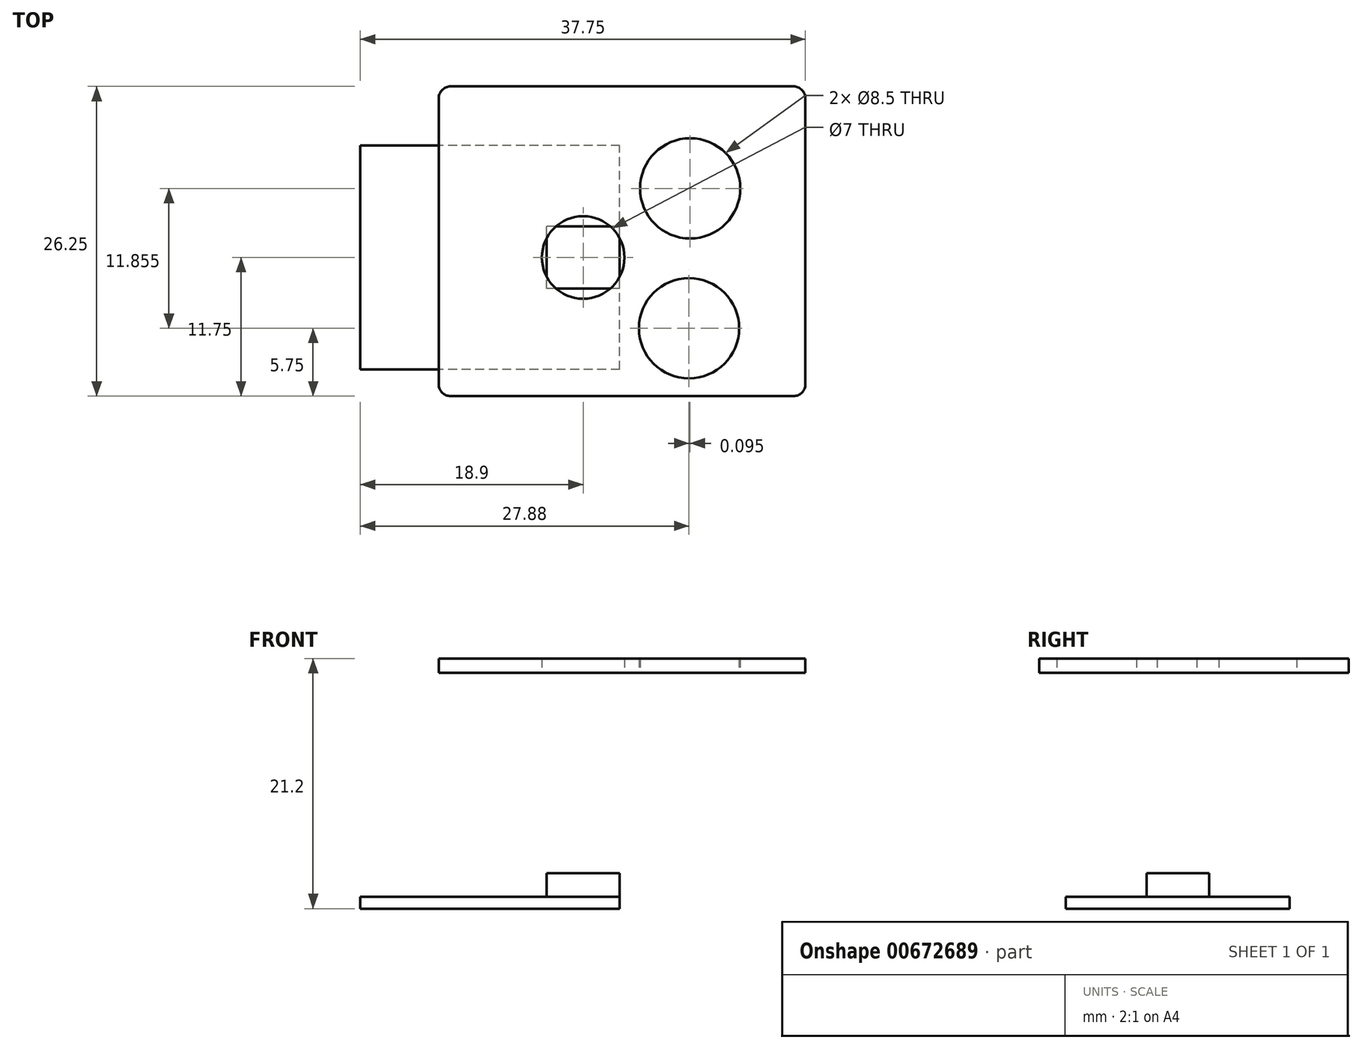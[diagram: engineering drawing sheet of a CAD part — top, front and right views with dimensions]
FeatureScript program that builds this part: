
annotation { "Feature Type Name" : "Feature", "Feature Type Description" : "" }
export const myFeature = defineFeature(function(context is Context, id is Id, definition is map)
    precondition{}
    {
        {
            var Q0;
            Q0=qCreatedBy(makeId("Top.planeOp"),FACE);
            var sketch = newSketch(context, id + "F0", { "sketchPlane" : qUnion([Q0])});
            skCircle(sketch, "E0", {"center": v(0, 0) * mm, "radius": 12.25 * mm});
            skCircle(sketch, "E1", {"center": v(0, 0) * mm, "radius": 10 * mm});
            skCircle(sketch, "E2", {"center": v(0, 0) * mm, "radius": 9 * mm});
            skCircle(sketch, "E3", {"center": v(0, 0) * mm, "radius": 3.5 * mm});
            skSolve(sketch);
        }
        {
            var Q0;
            Q0=qCreatedBy(makeId("Top.planeOp"),FACE);
            var sketch = newSketch(context, id + "F1", { "sketchPlane" : qUnion([Q0])});
            skLineSegment(sketch, "E4.bottom", {"start": v(3.1, -2.65) * mm, "end": v(-3.1, -2.65) * mm});
            skLineSegment(sketch, "E4.top", {"start": v(3.1, 2.65) * mm, "end": v(-3.1, 2.65) * mm});
            skLineSegment(sketch, "E4.right", {"start": v(-3.1, -2.65) * mm, "end": v(-3.1, 2.65) * mm});
            skPoint(sketch, "E4.middle", {"position": v(0, 0) * mm});
            skLineSegment(sketch, "E5.bottom", {"start": v(3.1, -9.5) * mm, "end": v(-18.9, -9.5) * mm});
            skLineSegment(sketch, "E5.top", {"start": v(3.1, 9.5) * mm, "end": v(-18.9, 9.5) * mm});
            skLineSegment(sketch, "E5.left", {"start": v(3.1, -9.5) * mm, "end": v(3.1, 9.5) * mm});
            skLineSegment(sketch, "E5.right", {"start": v(-18.9, -9.5) * mm, "end": v(-18.9, 9.5) * mm});
            skLineSegment(sketch, "E6.bottom", {"start": v(18.78, 13) * mm, "end": v(-13.22, 13) * mm});
            skLineSegment(sketch, "E6.top", {"start": v(18.78, 14.1) * mm, "end": v(-13.22, 14.1) * mm});
            skLineSegment(sketch, "E6.left", {"start": v(18.78, 13) * mm, "end": v(18.78, 14.1) * mm});
            skLineSegment(sketch, "E6.right", {"start": v(-13.22, 13) * mm, "end": v(-13.22, 14.1) * mm});
            skPoint(sketch, "E6.middle", {"position": v(2.78, 13.54) * mm});
            skLineSegment(sketch, "E7.bottom", {"start": v(12.25, -12.25) * mm, "end": v(-12.25, -12.25) * mm});
            skLineSegment(sketch, "E7.top", {"start": v(12.25, 12.25) * mm, "end": v(-12.25, 12.25) * mm});
            skLineSegment(sketch, "E7.left", {"start": v(12.25, -12.25) * mm, "end": v(12.25, 12.25) * mm});
            skLineSegment(sketch, "E7.right", {"start": v(-12.25, -12.25) * mm, "end": v(-12.25, 12.25) * mm});
            skSolve(sketch);
        }
        {
            var Q0;
            Q0=qCreatedBy(makeId("Top.planeOp"),FACE);
            var sketch = newSketch(context, id + "F2", { "sketchPlane" : qUnion([Q0])});
            skCircle(sketch, "E8", {"center": v(8.98, -6) * mm, "radius": 4.25 * mm});
            skCircle(sketch, "E9", {"center": v(8.98, -6) * mm, "radius": 1.8 * mm});
            skLineSegment(sketch, "E10", {"start": v(-13.47, -10.25) * mm, "end": v(15.3, -10.25) * mm});
            skLineSegment(sketch, "E11", {"start": v(-13.52, -6) * mm, "end": v(15.26, -6) * mm});
            skCircle(sketch, "E12", {"center": v(9.07, 5.86) * mm, "radius": 1.8 * mm});
            skCircle(sketch, "E13", {"center": v(9.07, 5.86) * mm, "radius": 4.25 * mm});
            skLineSegment(sketch, "E14", {"start": v(-12.37, 10.1) * mm, "end": v(16.41, 10.1) * mm});
            skLineSegment(sketch, "E15", {"start": v(-12.37, 5.86) * mm, "end": v(16.4, 5.86) * mm});
            skLineSegment(sketch, "E16", {"start": v(8.98, -6) * mm, "end": v(3.1, 0) * mm});
            skPoint(sketch, "E17", {"position": v(3.1, 0) * mm});
            skLineSegment(sketch, "E18", {"start": v(3.1, 0) * mm, "end": v(9.07, 5.86) * mm});
            skLineSegment(sketch, "E19.bottom", {"start": v(22.5, -11.75) * mm, "end": v(-22.5, -11.75) * mm});
            skPoint(sketch, "E19.middle", {"position": v(0, 0) * mm});
            skLineSegment(sketch, "E20.0", {"start": v(22.5, -12.25) * mm, "end": v(-22.5, -12.25) * mm});
            skLineSegment(sketch, "E21", {"start": v(0, -12.25) * mm, "end": v(-22.5, -11.75) * mm});
            skLineSegment(sketch, "E22", {"start": v(22.5, -11.75) * mm, "end": v(0, -12.25) * mm});
            skSolve(sketch);
        }
        {
            var Q0;
            Q0=qCreatedBy(makeId("Top.planeOp"),FACE);
            var sketch = newSketch(context, id + "F3", { "sketchPlane" : qUnion([Q0])});
            skPoint(sketch, "E23.middle", {"position": v(0, 0.27) * mm});
            skPoint(sketch, "E24.7.0.0", {"position": v(-11.9, 11.25) * mm});
            skLineSegment(sketch, "E24.7.0.1", {"start": v(-11.55, 10.25) * mm, "end": v(-12.25, 10.25) * mm});
            skLineSegment(sketch, "E24.7.0.2", {"start": v(-11.55, 10.25) * mm, "end": v(-11.55, 12.25) * mm});
            skLineSegment(sketch, "E24.7.0.3", {"start": v(-12.25, 10.25) * mm, "end": v(-12.25, 12.25) * mm});
            skLineSegment(sketch, "E24.7.0.4", {"start": v(-11.55, 12.25) * mm, "end": v(-12.25, 12.25) * mm});
            skPoint(sketch, "E24.8.0.0", {"position": v(-10.95, 11.25) * mm});
            skLineSegment(sketch, "E24.8.0.1", {"start": v(-10.6, 10.25) * mm, "end": v(-11.3, 10.25) * mm});
            skLineSegment(sketch, "E24.8.0.2", {"start": v(-10.6, 10.25) * mm, "end": v(-10.6, 12.25) * mm});
            skLineSegment(sketch, "E24.8.0.3", {"start": v(-11.3, 10.25) * mm, "end": v(-11.3, 12.25) * mm});
            skLineSegment(sketch, "E24.8.0.4", {"start": v(-10.6, 12.25) * mm, "end": v(-11.3, 12.25) * mm});
            skPoint(sketch, "E24.9.0.0", {"position": v(-10, 11.25) * mm});
            skLineSegment(sketch, "E24.9.0.1", {"start": v(-9.65, 10.25) * mm, "end": v(-10.35, 10.25) * mm});
            skLineSegment(sketch, "E24.9.0.2", {"start": v(-9.65, 10.25) * mm, "end": v(-9.65, 12.25) * mm});
            skLineSegment(sketch, "E24.9.0.3", {"start": v(-10.35, 10.25) * mm, "end": v(-10.35, 12.25) * mm});
            skLineSegment(sketch, "E24.9.0.4", {"start": v(-9.65, 12.25) * mm, "end": v(-10.35, 12.25) * mm});
            skPoint(sketch, "E24.10.0.0", {"position": v(-9.05, 11.25) * mm});
            skLineSegment(sketch, "E24.10.0.1", {"start": v(-8.7, 10.25) * mm, "end": v(-9.4, 10.25) * mm});
            skLineSegment(sketch, "E24.10.0.2", {"start": v(-8.7, 10.25) * mm, "end": v(-8.7, 12.25) * mm});
            skLineSegment(sketch, "E24.10.0.3", {"start": v(-9.4, 10.25) * mm, "end": v(-9.4, 12.25) * mm});
            skLineSegment(sketch, "E24.10.0.4", {"start": v(-8.7, 12.25) * mm, "end": v(-9.4, 12.25) * mm});
            skPoint(sketch, "E24.11.0.0", {"position": v(-8.1, 11.25) * mm});
            skLineSegment(sketch, "E24.11.0.1", {"start": v(-7.75, 10.25) * mm, "end": v(-8.45, 10.25) * mm});
            skLineSegment(sketch, "E24.11.0.2", {"start": v(-7.75, 10.25) * mm, "end": v(-7.75, 12.25) * mm});
            skLineSegment(sketch, "E24.11.0.3", {"start": v(-8.45, 10.25) * mm, "end": v(-8.45, 12.25) * mm});
            skLineSegment(sketch, "E24.11.0.4", {"start": v(-7.75, 12.25) * mm, "end": v(-8.45, 12.25) * mm});
            skPoint(sketch, "E24.12.0.0", {"position": v(-7.15, 11.25) * mm});
            skLineSegment(sketch, "E24.12.0.1", {"start": v(-6.8, 10.25) * mm, "end": v(-7.5, 10.25) * mm});
            skLineSegment(sketch, "E24.12.0.2", {"start": v(-6.8, 10.25) * mm, "end": v(-6.8, 12.25) * mm});
            skLineSegment(sketch, "E24.12.0.3", {"start": v(-7.5, 10.25) * mm, "end": v(-7.5, 12.25) * mm});
            skLineSegment(sketch, "E24.12.0.4", {"start": v(-6.8, 12.25) * mm, "end": v(-7.5, 12.25) * mm});
            skPoint(sketch, "E24.13.0.0", {"position": v(-6.2, 11.25) * mm});
            skLineSegment(sketch, "E24.13.0.1", {"start": v(-5.85, 10.25) * mm, "end": v(-6.55, 10.25) * mm});
            skLineSegment(sketch, "E24.13.0.2", {"start": v(-5.85, 10.25) * mm, "end": v(-5.85, 12.25) * mm});
            skLineSegment(sketch, "E24.13.0.3", {"start": v(-6.55, 10.25) * mm, "end": v(-6.55, 12.25) * mm});
            skLineSegment(sketch, "E24.13.0.4", {"start": v(-5.85, 12.25) * mm, "end": v(-6.55, 12.25) * mm});
            skPoint(sketch, "E24.14.0.0", {"position": v(-5.25, 11.25) * mm});
            skLineSegment(sketch, "E24.14.0.1", {"start": v(-4.9, 10.25) * mm, "end": v(-5.6, 10.25) * mm});
            skLineSegment(sketch, "E24.14.0.2", {"start": v(-4.9, 10.25) * mm, "end": v(-4.9, 12.25) * mm});
            skLineSegment(sketch, "E24.14.0.3", {"start": v(-5.6, 10.25) * mm, "end": v(-5.6, 12.25) * mm});
            skLineSegment(sketch, "E24.14.0.4", {"start": v(-4.9, 12.25) * mm, "end": v(-5.6, 12.25) * mm});
            skPoint(sketch, "E24.15.0.0", {"position": v(-4.3, 11.25) * mm});
            skLineSegment(sketch, "E24.15.0.1", {"start": v(-3.95, 10.25) * mm, "end": v(-4.65, 10.25) * mm});
            skLineSegment(sketch, "E24.15.0.2", {"start": v(-3.95, 10.25) * mm, "end": v(-3.95, 12.25) * mm});
            skLineSegment(sketch, "E24.15.0.3", {"start": v(-4.65, 10.25) * mm, "end": v(-4.65, 12.25) * mm});
            skLineSegment(sketch, "E24.15.0.4", {"start": v(-3.95, 12.25) * mm, "end": v(-4.65, 12.25) * mm});
            skPoint(sketch, "E24.16.0.0", {"position": v(-3.35, 11.25) * mm});
            skLineSegment(sketch, "E24.16.0.1", {"start": v(-3, 10.25) * mm, "end": v(-3.7, 10.25) * mm});
            skLineSegment(sketch, "E24.16.0.2", {"start": v(-3, 10.25) * mm, "end": v(-3, 12.25) * mm});
            skLineSegment(sketch, "E24.16.0.3", {"start": v(-3.7, 10.25) * mm, "end": v(-3.7, 12.25) * mm});
            skLineSegment(sketch, "E24.16.0.4", {"start": v(-3, 12.25) * mm, "end": v(-3.7, 12.25) * mm});
            skPoint(sketch, "E24.17.0.0", {"position": v(-2.4, 11.25) * mm});
            skLineSegment(sketch, "E24.17.0.1", {"start": v(-2.05, 10.25) * mm, "end": v(-2.75, 10.25) * mm});
            skLineSegment(sketch, "E24.17.0.2", {"start": v(-2.05, 10.25) * mm, "end": v(-2.05, 12.25) * mm});
            skLineSegment(sketch, "E24.17.0.3", {"start": v(-2.75, 10.25) * mm, "end": v(-2.75, 12.25) * mm});
            skLineSegment(sketch, "E24.17.0.4", {"start": v(-2.05, 12.25) * mm, "end": v(-2.75, 12.25) * mm});
            skPoint(sketch, "E24.18.0.0", {"position": v(-1.45, 11.25) * mm});
            skLineSegment(sketch, "E24.18.0.1", {"start": v(-1.1, 10.25) * mm, "end": v(-1.8, 10.25) * mm});
            skLineSegment(sketch, "E24.18.0.2", {"start": v(-1.1, 10.25) * mm, "end": v(-1.1, 12.25) * mm});
            skLineSegment(sketch, "E24.18.0.3", {"start": v(-1.8, 10.25) * mm, "end": v(-1.8, 12.25) * mm});
            skLineSegment(sketch, "E24.18.0.4", {"start": v(-1.1, 12.25) * mm, "end": v(-1.8, 12.25) * mm});
            skPoint(sketch, "E24.19.0.0", {"position": v(-0.5, 11.25) * mm});
            skLineSegment(sketch, "E24.19.0.1", {"start": v(-0.15, 10.25) * mm, "end": v(-0.85, 10.25) * mm});
            skLineSegment(sketch, "E24.19.0.2", {"start": v(-0.15, 10.25) * mm, "end": v(-0.15, 12.25) * mm});
            skLineSegment(sketch, "E24.19.0.3", {"start": v(-0.85, 10.25) * mm, "end": v(-0.85, 12.25) * mm});
            skLineSegment(sketch, "E24.19.0.4", {"start": v(-0.15, 12.25) * mm, "end": v(-0.85, 12.25) * mm});
            skPoint(sketch, "E24.20.0.0", {"position": v(0.45, 11.25) * mm});
            skLineSegment(sketch, "E24.20.0.1", {"start": v(0.8, 10.25) * mm, "end": v(0.1, 10.25) * mm});
            skLineSegment(sketch, "E24.20.0.2", {"start": v(0.8, 10.25) * mm, "end": v(0.8, 12.25) * mm});
            skLineSegment(sketch, "E24.20.0.3", {"start": v(0.1, 10.25) * mm, "end": v(0.1, 12.25) * mm});
            skLineSegment(sketch, "E24.20.0.4", {"start": v(0.8, 12.25) * mm, "end": v(0.1, 12.25) * mm});
            skPoint(sketch, "E24.21.0.0", {"position": v(1.4, 11.25) * mm});
            skLineSegment(sketch, "E24.21.0.1", {"start": v(1.75, 10.25) * mm, "end": v(1.05, 10.25) * mm});
            skLineSegment(sketch, "E24.21.0.2", {"start": v(1.75, 10.25) * mm, "end": v(1.75, 12.25) * mm});
            skLineSegment(sketch, "E24.21.0.3", {"start": v(1.05, 10.25) * mm, "end": v(1.05, 12.25) * mm});
            skLineSegment(sketch, "E24.21.0.4", {"start": v(1.75, 12.25) * mm, "end": v(1.05, 12.25) * mm});
            skPoint(sketch, "E24.22.0.0", {"position": v(2.35, 11.25) * mm});
            skLineSegment(sketch, "E24.22.0.1", {"start": v(2.7, 10.25) * mm, "end": v(2, 10.25) * mm});
            skLineSegment(sketch, "E24.22.0.2", {"start": v(2.7, 10.25) * mm, "end": v(2.7, 12.25) * mm});
            skLineSegment(sketch, "E24.22.0.3", {"start": v(2, 10.25) * mm, "end": v(2, 12.25) * mm});
            skLineSegment(sketch, "E24.22.0.4", {"start": v(2.7, 12.25) * mm, "end": v(2, 12.25) * mm});
            skPoint(sketch, "E24.23.0.0", {"position": v(3.3, 11.25) * mm});
            skLineSegment(sketch, "E24.23.0.1", {"start": v(3.65, 10.25) * mm, "end": v(2.95, 10.25) * mm});
            skLineSegment(sketch, "E24.23.0.2", {"start": v(3.65, 10.25) * mm, "end": v(3.65, 12.25) * mm});
            skLineSegment(sketch, "E24.23.0.3", {"start": v(2.95, 10.25) * mm, "end": v(2.95, 12.25) * mm});
            skLineSegment(sketch, "E24.23.0.4", {"start": v(3.65, 12.25) * mm, "end": v(2.95, 12.25) * mm});
            skPoint(sketch, "E24.24.0.0", {"position": v(4.25, 11.25) * mm});
            skLineSegment(sketch, "E24.24.0.1", {"start": v(4.6, 10.25) * mm, "end": v(3.9, 10.25) * mm});
            skLineSegment(sketch, "E24.24.0.2", {"start": v(4.6, 10.25) * mm, "end": v(4.6, 12.25) * mm});
            skLineSegment(sketch, "E24.24.0.3", {"start": v(3.9, 10.25) * mm, "end": v(3.9, 12.25) * mm});
            skLineSegment(sketch, "E24.24.0.4", {"start": v(4.6, 12.25) * mm, "end": v(3.9, 12.25) * mm});
            skPoint(sketch, "E24.25.0.0", {"position": v(5.2, 11.25) * mm});
            skLineSegment(sketch, "E24.25.0.1", {"start": v(5.55, 10.25) * mm, "end": v(4.85, 10.25) * mm});
            skLineSegment(sketch, "E24.25.0.2", {"start": v(5.55, 10.25) * mm, "end": v(5.55, 12.25) * mm});
            skLineSegment(sketch, "E24.25.0.3", {"start": v(4.85, 10.25) * mm, "end": v(4.85, 12.25) * mm});
            skLineSegment(sketch, "E24.25.0.4", {"start": v(5.55, 12.25) * mm, "end": v(4.85, 12.25) * mm});
            skPoint(sketch, "E24.26.0.0", {"position": v(6.15, 11.25) * mm});
            skLineSegment(sketch, "E24.26.0.1", {"start": v(6.5, 10.25) * mm, "end": v(5.8, 10.25) * mm});
            skLineSegment(sketch, "E24.26.0.2", {"start": v(6.5, 10.25) * mm, "end": v(6.5, 12.25) * mm});
            skLineSegment(sketch, "E24.26.0.3", {"start": v(5.8, 10.25) * mm, "end": v(5.8, 12.25) * mm});
            skLineSegment(sketch, "E24.26.0.4", {"start": v(6.5, 12.25) * mm, "end": v(5.8, 12.25) * mm});
            skPoint(sketch, "E24.27.0.0", {"position": v(7.1, 11.25) * mm});
            skLineSegment(sketch, "E24.27.0.1", {"start": v(7.45, 10.25) * mm, "end": v(6.75, 10.25) * mm});
            skLineSegment(sketch, "E24.27.0.2", {"start": v(7.45, 10.25) * mm, "end": v(7.45, 12.25) * mm});
            skLineSegment(sketch, "E24.27.0.3", {"start": v(6.75, 10.25) * mm, "end": v(6.75, 12.25) * mm});
            skLineSegment(sketch, "E24.27.0.4", {"start": v(7.45, 12.25) * mm, "end": v(6.75, 12.25) * mm});
            skPoint(sketch, "E24.28.0.0", {"position": v(8.05, 11.25) * mm});
            skLineSegment(sketch, "E24.28.0.1", {"start": v(8.4, 10.25) * mm, "end": v(7.7, 10.25) * mm});
            skLineSegment(sketch, "E24.28.0.2", {"start": v(8.4, 10.25) * mm, "end": v(8.4, 12.25) * mm});
            skLineSegment(sketch, "E24.28.0.3", {"start": v(7.7, 10.25) * mm, "end": v(7.7, 12.25) * mm});
            skLineSegment(sketch, "E24.28.0.4", {"start": v(8.4, 12.25) * mm, "end": v(7.7, 12.25) * mm});
            skPoint(sketch, "E24.29.0.0", {"position": v(9, 11.25) * mm});
            skLineSegment(sketch, "E24.29.0.1", {"start": v(9.35, 10.25) * mm, "end": v(8.65, 10.25) * mm});
            skLineSegment(sketch, "E24.29.0.2", {"start": v(9.35, 10.25) * mm, "end": v(9.35, 12.25) * mm});
            skLineSegment(sketch, "E24.29.0.3", {"start": v(8.65, 10.25) * mm, "end": v(8.65, 12.25) * mm});
            skLineSegment(sketch, "E24.29.0.4", {"start": v(9.35, 12.25) * mm, "end": v(8.65, 12.25) * mm});
            skPoint(sketch, "E24.30.0.0", {"position": v(9.95, 11.25) * mm});
            skLineSegment(sketch, "E24.30.0.1", {"start": v(10.3, 10.25) * mm, "end": v(9.6, 10.25) * mm});
            skLineSegment(sketch, "E24.30.0.2", {"start": v(10.3, 10.25) * mm, "end": v(10.3, 12.25) * mm});
            skLineSegment(sketch, "E24.30.0.3", {"start": v(9.6, 10.25) * mm, "end": v(9.6, 12.25) * mm});
            skLineSegment(sketch, "E24.30.0.4", {"start": v(10.3, 12.25) * mm, "end": v(9.6, 12.25) * mm});
            skPoint(sketch, "E24.31.0.0", {"position": v(10.9, 11.25) * mm});
            skLineSegment(sketch, "E24.31.0.1", {"start": v(11.25, 10.25) * mm, "end": v(10.55, 10.25) * mm});
            skLineSegment(sketch, "E24.31.0.2", {"start": v(11.25, 10.25) * mm, "end": v(11.25, 12.25) * mm});
            skLineSegment(sketch, "E24.31.0.3", {"start": v(10.55, 10.25) * mm, "end": v(10.55, 12.25) * mm});
            skLineSegment(sketch, "E24.31.0.4", {"start": v(11.25, 12.25) * mm, "end": v(10.55, 12.25) * mm});
            skPoint(sketch, "E24.32.0.0", {"position": v(11.85, 11.25) * mm});
            skLineSegment(sketch, "E24.32.0.1", {"start": v(12.2, 10.25) * mm, "end": v(11.5, 10.25) * mm});
            skLineSegment(sketch, "E24.32.0.2", {"start": v(12.2, 10.25) * mm, "end": v(12.2, 12.25) * mm});
            skLineSegment(sketch, "E24.32.0.3", {"start": v(11.5, 10.25) * mm, "end": v(11.5, 12.25) * mm});
            skLineSegment(sketch, "E24.32.0.4", {"start": v(12.2, 12.25) * mm, "end": v(11.5, 12.25) * mm});
            skPoint(sketch, "E24.33.0.0", {"position": v(12.8, 11.25) * mm});
            skLineSegment(sketch, "E24.33.0.1", {"start": v(13.15, 10.25) * mm, "end": v(12.45, 10.25) * mm});
            skLineSegment(sketch, "E24.33.0.2", {"start": v(13.15, 10.25) * mm, "end": v(13.15, 12.25) * mm});
            skLineSegment(sketch, "E24.33.0.3", {"start": v(12.45, 10.25) * mm, "end": v(12.45, 12.25) * mm});
            skLineSegment(sketch, "E24.33.0.4", {"start": v(13.15, 12.25) * mm, "end": v(12.45, 12.25) * mm});
            skPoint(sketch, "E24.34.0.0", {"position": v(13.75, 11.25) * mm});
            skLineSegment(sketch, "E24.34.0.1", {"start": v(14.1, 10.25) * mm, "end": v(13.4, 10.25) * mm});
            skLineSegment(sketch, "E24.34.0.2", {"start": v(14.1, 10.25) * mm, "end": v(14.1, 12.25) * mm});
            skLineSegment(sketch, "E24.34.0.3", {"start": v(13.4, 10.25) * mm, "end": v(13.4, 12.25) * mm});
            skLineSegment(sketch, "E24.34.0.4", {"start": v(14.1, 12.25) * mm, "end": v(13.4, 12.25) * mm});
            skPoint(sketch, "E24.35.0.0", {"position": v(14.7, 11.25) * mm});
            skLineSegment(sketch, "E24.35.0.1", {"start": v(15.05, 10.25) * mm, "end": v(14.35, 10.25) * mm});
            skLineSegment(sketch, "E24.35.0.2", {"start": v(15.05, 10.25) * mm, "end": v(15.05, 12.25) * mm});
            skLineSegment(sketch, "E24.35.0.3", {"start": v(14.35, 10.25) * mm, "end": v(14.35, 12.25) * mm});
            skLineSegment(sketch, "E24.35.0.4", {"start": v(15.05, 12.25) * mm, "end": v(14.35, 12.25) * mm});
            skPoint(sketch, "E24.36.0.0", {"position": v(15.65, 11.25) * mm});
            skLineSegment(sketch, "E24.36.0.1", {"start": v(16, 10.25) * mm, "end": v(15.3, 10.25) * mm});
            skLineSegment(sketch, "E24.36.0.2", {"start": v(16, 10.25) * mm, "end": v(16, 12.25) * mm});
            skLineSegment(sketch, "E24.36.0.3", {"start": v(15.3, 10.25) * mm, "end": v(15.3, 12.25) * mm});
            skLineSegment(sketch, "E24.36.0.4", {"start": v(16, 12.25) * mm, "end": v(15.3, 12.25) * mm});
            skPoint(sketch, "E24.37.0.0", {"position": v(16.6, 11.25) * mm});
            skLineSegment(sketch, "E24.37.0.1", {"start": v(16.95, 10.25) * mm, "end": v(16.25, 10.25) * mm});
            skLineSegment(sketch, "E24.37.0.2", {"start": v(16.95, 10.25) * mm, "end": v(16.95, 12.25) * mm});
            skLineSegment(sketch, "E24.37.0.3", {"start": v(16.25, 10.25) * mm, "end": v(16.25, 12.25) * mm});
            skLineSegment(sketch, "E24.37.0.4", {"start": v(16.95, 12.25) * mm, "end": v(16.25, 12.25) * mm});
            skPoint(sketch, "E24.38.0.0", {"position": v(17.55, 11.25) * mm});
            skLineSegment(sketch, "E24.38.0.1", {"start": v(17.9, 10.25) * mm, "end": v(17.2, 10.25) * mm});
            skLineSegment(sketch, "E24.38.0.2", {"start": v(17.9, 10.25) * mm, "end": v(17.9, 12.25) * mm});
            skLineSegment(sketch, "E24.38.0.3", {"start": v(17.2, 10.25) * mm, "end": v(17.2, 12.25) * mm});
            skLineSegment(sketch, "E24.38.0.4", {"start": v(17.9, 12.25) * mm, "end": v(17.2, 12.25) * mm});
            skPoint(sketch, "E24.39.0.0", {"position": v(18.5, 11.25) * mm});
            skLineSegment(sketch, "E24.39.0.1", {"start": v(18.85, 10.25) * mm, "end": v(18.15, 10.25) * mm});
            skLineSegment(sketch, "E24.39.0.2", {"start": v(18.85, 10.25) * mm, "end": v(18.85, 12.25) * mm});
            skLineSegment(sketch, "E24.39.0.3", {"start": v(18.15, 10.25) * mm, "end": v(18.15, 12.25) * mm});
            skLineSegment(sketch, "E24.39.0.4", {"start": v(18.85, 12.25) * mm, "end": v(18.15, 12.25) * mm});
            skPoint(sketch, "E25.0.1.0", {"position": v(-4.3, 9) * mm});
            skPoint(sketch, "E25.0.1.1", {"position": v(10.9, 9) * mm});
            skPoint(sketch, "E25.0.1.2", {"position": v(11.85, 9) * mm});
            skPoint(sketch, "E25.0.1.3", {"position": v(-3.35, 9) * mm});
            skPoint(sketch, "E25.0.1.4", {"position": v(12.8, 9) * mm});
            skPoint(sketch, "E25.0.1.5", {"position": v(-2.4, 9) * mm});
            skPoint(sketch, "E25.0.1.6", {"position": v(13.75, 9) * mm});
            skPoint(sketch, "E25.0.1.7", {"position": v(-1.45, 9) * mm});
            skPoint(sketch, "E25.0.1.8", {"position": v(14.7, 9) * mm});
            skPoint(sketch, "E25.0.1.9", {"position": v(-0.5, 9) * mm});
            skPoint(sketch, "E25.0.1.11", {"position": v(15.65, 9) * mm});
            skPoint(sketch, "E25.0.1.12", {"position": v(0.45, 9) * mm});
            skPoint(sketch, "E25.0.1.14", {"position": v(16.6, 9) * mm});
            skPoint(sketch, "E25.0.1.15", {"position": v(1.4, 9) * mm});
            skPoint(sketch, "E25.0.1.17", {"position": v(17.55, 9) * mm});
            skPoint(sketch, "E25.0.1.18", {"position": v(2.35, 9) * mm});
            skPoint(sketch, "E25.0.1.19", {"position": v(-11.9, 9) * mm});
            skPoint(sketch, "E25.0.1.20", {"position": v(18.5, 9) * mm});
            skPoint(sketch, "E25.0.1.21", {"position": v(3.3, 9) * mm});
            skPoint(sketch, "E25.0.1.23", {"position": v(-10.95, 9) * mm});
            skPoint(sketch, "E25.0.1.25", {"position": v(4.25, 9) * mm});
            skPoint(sketch, "E25.0.1.26", {"position": v(9.95, 9) * mm});
            skPoint(sketch, "E25.0.1.27", {"position": v(6.15, 9) * mm});
            skPoint(sketch, "E25.0.1.28", {"position": v(-9.05, 9) * mm});
            skPoint(sketch, "E25.0.1.30", {"position": v(-5.25, 9) * mm});
            skPoint(sketch, "E25.0.1.31", {"position": v(-6.2, 9) * mm});
            skPoint(sketch, "E25.0.1.32", {"position": v(9, 9) * mm});
            skPoint(sketch, "E25.0.1.38", {"position": v(8.05, 9) * mm});
            skPoint(sketch, "E25.0.1.39", {"position": v(-7.15, 9) * mm});
            skPoint(sketch, "E25.0.1.40", {"position": v(5.2, 9) * mm});
            skPoint(sketch, "E25.0.1.41", {"position": v(-10, 9) * mm});
            skPoint(sketch, "E25.0.1.44", {"position": v(7.1, 9) * mm});
            skPoint(sketch, "E25.0.1.45", {"position": v(-8.1, 9) * mm});
            skLineSegment(sketch, "E25.0.1.54", {"start": v(18.85, 8) * mm, "end": v(18.15, 8) * mm});
            skLineSegment(sketch, "E25.0.1.55", {"start": v(18.85, 8) * mm, "end": v(18.85, 10) * mm});
            skLineSegment(sketch, "E25.0.1.56", {"start": v(18.15, 8) * mm, "end": v(18.15, 10) * mm});
            skLineSegment(sketch, "E25.0.1.67", {"start": v(17.9, 8) * mm, "end": v(17.2, 8) * mm});
            skLineSegment(sketch, "E25.0.1.69", {"start": v(17.9, 8) * mm, "end": v(17.9, 10) * mm});
            skLineSegment(sketch, "E25.0.1.71", {"start": v(17.2, 8) * mm, "end": v(17.2, 10) * mm});
            skLineSegment(sketch, "E25.0.1.72", {"start": v(16.95, 8) * mm, "end": v(16.25, 8) * mm});
            skLineSegment(sketch, "E25.0.1.74", {"start": v(16.95, 8) * mm, "end": v(16.95, 10) * mm});
            skLineSegment(sketch, "E25.0.1.79", {"start": v(16.25, 8) * mm, "end": v(16.25, 10) * mm});
            skLineSegment(sketch, "E25.0.1.80", {"start": v(16, 10) * mm, "end": v(15.3, 10) * mm});
            skLineSegment(sketch, "E25.0.1.81", {"start": v(12.2, 10) * mm, "end": v(11.5, 10) * mm});
            skLineSegment(sketch, "E25.0.1.83", {"start": v(16.95, 10) * mm, "end": v(16.25, 10) * mm});
            skLineSegment(sketch, "E25.0.1.84", {"start": v(13.15, 10) * mm, "end": v(12.45, 10) * mm});
            skLineSegment(sketch, "E25.0.1.85", {"start": v(9.35, 10) * mm, "end": v(8.65, 10) * mm});
            skLineSegment(sketch, "E25.0.1.86", {"start": v(5.55, 10) * mm, "end": v(4.85, 10) * mm});
            skLineSegment(sketch, "E25.0.1.87", {"start": v(8.4, 10) * mm, "end": v(7.7, 10) * mm});
            skLineSegment(sketch, "E25.0.1.90", {"start": v(13.4, 8) * mm, "end": v(13.4, 10) * mm});
            skLineSegment(sketch, "E25.0.1.91", {"start": v(9.6, 8) * mm, "end": v(9.6, 10) * mm});
            skLineSegment(sketch, "E25.0.1.92", {"start": v(5.8, 8) * mm, "end": v(5.8, 10) * mm});
            skLineSegment(sketch, "E25.0.1.94", {"start": v(10.3, 10) * mm, "end": v(9.6, 10) * mm});
            skLineSegment(sketch, "E25.0.1.95", {"start": v(6.5, 10) * mm, "end": v(5.8, 10) * mm});
            skLineSegment(sketch, "E25.0.1.96", {"start": v(17.9, 10) * mm, "end": v(17.2, 10) * mm});
            skLineSegment(sketch, "E25.0.1.97", {"start": v(14.1, 10) * mm, "end": v(13.4, 10) * mm});
            skLineSegment(sketch, "E25.0.1.99", {"start": v(15.05, 8) * mm, "end": v(14.35, 8) * mm});
            skLineSegment(sketch, "E25.0.1.100", {"start": v(11.25, 8) * mm, "end": v(11.25, 10) * mm});
            skLineSegment(sketch, "E25.0.1.101", {"start": v(7.45, 8) * mm, "end": v(7.45, 10) * mm});
            skLineSegment(sketch, "E25.0.1.102", {"start": v(15.05, 8) * mm, "end": v(15.05, 10) * mm});
            skLineSegment(sketch, "E25.0.1.104", {"start": v(10.55, 8) * mm, "end": v(10.55, 10) * mm});
            skLineSegment(sketch, "E25.0.1.105", {"start": v(6.75, 8) * mm, "end": v(6.75, 10) * mm});
            skLineSegment(sketch, "E25.0.1.106", {"start": v(14.35, 8) * mm, "end": v(14.35, 10) * mm});
            skLineSegment(sketch, "E25.0.1.108", {"start": v(11.25, 10) * mm, "end": v(10.55, 10) * mm});
            skLineSegment(sketch, "E25.0.1.109", {"start": v(7.45, 10) * mm, "end": v(6.75, 10) * mm});
            skLineSegment(sketch, "E25.0.1.110", {"start": v(18.85, 10) * mm, "end": v(18.15, 10) * mm});
            skLineSegment(sketch, "E25.0.1.111", {"start": v(15.05, 10) * mm, "end": v(14.35, 10) * mm});
            skLineSegment(sketch, "E25.0.1.113", {"start": v(16, 8) * mm, "end": v(16, 10) * mm});
            skLineSegment(sketch, "E25.0.1.114", {"start": v(12.2, 8) * mm, "end": v(12.2, 10) * mm});
            skLineSegment(sketch, "E25.0.1.115", {"start": v(8.4, 8) * mm, "end": v(8.4, 10) * mm});
            skLineSegment(sketch, "E25.0.1.116", {"start": v(4.6, 8) * mm, "end": v(4.6, 10) * mm});
            skLineSegment(sketch, "E25.0.1.117", {"start": v(13.15, 8) * mm, "end": v(13.15, 10) * mm});
            skLineSegment(sketch, "E25.0.1.118", {"start": v(9.35, 8) * mm, "end": v(9.35, 10) * mm});
            skLineSegment(sketch, "E25.0.1.119", {"start": v(16, 8) * mm, "end": v(15.3, 8) * mm});
            skLineSegment(sketch, "E25.0.1.121", {"start": v(15.3, 8) * mm, "end": v(15.3, 10) * mm});
            skLineSegment(sketch, "E25.0.1.122", {"start": v(11.5, 8) * mm, "end": v(11.5, 10) * mm});
            skLineSegment(sketch, "E25.0.1.123", {"start": v(7.7, 8) * mm, "end": v(7.7, 10) * mm});
            skLineSegment(sketch, "E25.0.1.127", {"start": v(4.85, 8) * mm, "end": v(4.85, 10) * mm});
            skLineSegment(sketch, "E25.0.1.128", {"start": v(12.45, 8) * mm, "end": v(12.45, 10) * mm});
            skLineSegment(sketch, "E25.0.1.129", {"start": v(-10.6, 10) * mm, "end": v(-11.3, 10) * mm});
            skLineSegment(sketch, "E25.0.1.130", {"start": v(-6.8, 10) * mm, "end": v(-7.5, 10) * mm});
            skLineSegment(sketch, "E25.0.1.131", {"start": v(1.75, 10) * mm, "end": v(1.05, 10) * mm});
            skLineSegment(sketch, "E25.0.1.132", {"start": v(-2.05, 10) * mm, "end": v(-2.75, 10) * mm});
            skLineSegment(sketch, "E25.0.1.133", {"start": v(-5.85, 10) * mm, "end": v(-6.55, 10) * mm});
            skLineSegment(sketch, "E25.0.1.134", {"start": v(0.8, 10) * mm, "end": v(0.1, 10) * mm});
            skLineSegment(sketch, "E25.0.1.135", {"start": v(-9.65, 10) * mm, "end": v(-10.35, 10) * mm});
            skLineSegment(sketch, "E25.0.1.136", {"start": v(-3, 10) * mm, "end": v(-3.7, 10) * mm});
            skLineSegment(sketch, "E25.0.1.139", {"start": v(2.7, 8) * mm, "end": v(2, 8) * mm});
            skLineSegment(sketch, "E25.0.1.140", {"start": v(-4.9, 8) * mm, "end": v(-5.6, 8) * mm});
            skLineSegment(sketch, "E25.0.1.141", {"start": v(-1.1, 8) * mm, "end": v(-1.8, 8) * mm});
            skLineSegment(sketch, "E25.0.1.142", {"start": v(-8.7, 8) * mm, "end": v(-9.4, 8) * mm});
            skLineSegment(sketch, "E25.0.1.143", {"start": v(14.1, 8) * mm, "end": v(13.4, 8) * mm});
            skLineSegment(sketch, "E25.0.1.144", {"start": v(10.3, 8) * mm, "end": v(9.6, 8) * mm});
            skLineSegment(sketch, "E25.0.1.145", {"start": v(6.5, 8) * mm, "end": v(5.8, 8) * mm});
            skLineSegment(sketch, "E25.0.1.147", {"start": v(4.6, 10) * mm, "end": v(3.9, 10) * mm});
            skLineSegment(sketch, "E25.0.1.148", {"start": v(2.7, 8) * mm, "end": v(2.7, 10) * mm});
            skLineSegment(sketch, "E25.0.1.149", {"start": v(-1.1, 8) * mm, "end": v(-1.1, 10) * mm});
            skLineSegment(sketch, "E25.0.1.150", {"start": v(-4.9, 8) * mm, "end": v(-4.9, 10) * mm});
            skLineSegment(sketch, "E25.0.1.151", {"start": v(-8.7, 8) * mm, "end": v(-8.7, 10) * mm});
            skLineSegment(sketch, "E25.0.1.152", {"start": v(14.1, 8) * mm, "end": v(14.1, 10) * mm});
            skLineSegment(sketch, "E25.0.1.153", {"start": v(10.3, 8) * mm, "end": v(10.3, 10) * mm});
            skLineSegment(sketch, "E25.0.1.154", {"start": v(6.5, 8) * mm, "end": v(6.5, 10) * mm});
            skLineSegment(sketch, "E25.0.1.157", {"start": v(2, 8) * mm, "end": v(2, 10) * mm});
            skLineSegment(sketch, "E25.0.1.158", {"start": v(-1.8, 8) * mm, "end": v(-1.8, 10) * mm});
            skLineSegment(sketch, "E25.0.1.159", {"start": v(-5.6, 8) * mm, "end": v(-5.6, 10) * mm});
            skLineSegment(sketch, "E25.0.1.160", {"start": v(-9.4, 8) * mm, "end": v(-9.4, 10) * mm});
            skLineSegment(sketch, "E25.0.1.161", {"start": v(1.75, 8) * mm, "end": v(1.05, 8) * mm});
            skLineSegment(sketch, "E25.0.1.162", {"start": v(-2.05, 8) * mm, "end": v(-2.75, 8) * mm});
            skLineSegment(sketch, "E25.0.1.163", {"start": v(-5.85, 8) * mm, "end": v(-6.55, 8) * mm});
            skLineSegment(sketch, "E25.0.1.164", {"start": v(-9.65, 8) * mm, "end": v(-10.35, 8) * mm});
            skLineSegment(sketch, "E25.0.1.165", {"start": v(-4.9, 10) * mm, "end": v(-5.6, 10) * mm});
            skLineSegment(sketch, "E25.0.1.166", {"start": v(-8.7, 10) * mm, "end": v(-9.4, 10) * mm});
            skLineSegment(sketch, "E25.0.1.167", {"start": v(2.7, 10) * mm, "end": v(2, 10) * mm});
            skLineSegment(sketch, "E25.0.1.168", {"start": v(13.15, 8) * mm, "end": v(12.45, 8) * mm});
            skLineSegment(sketch, "E25.0.1.169", {"start": v(9.35, 8) * mm, "end": v(8.65, 8) * mm});
            skLineSegment(sketch, "E25.0.1.170", {"start": v(-1.1, 10) * mm, "end": v(-1.8, 10) * mm});
            skLineSegment(sketch, "E25.0.1.171", {"start": v(5.55, 8) * mm, "end": v(4.85, 8) * mm});
            skLineSegment(sketch, "E25.0.1.172", {"start": v(-3.95, 8) * mm, "end": v(-4.65, 8) * mm});
            skLineSegment(sketch, "E25.0.1.173", {"start": v(-7.75, 8) * mm, "end": v(-8.45, 8) * mm});
            skLineSegment(sketch, "E25.0.1.174", {"start": v(-11.55, 8) * mm, "end": v(-12.25, 8) * mm});
            skLineSegment(sketch, "E25.0.1.176", {"start": v(11.25, 8) * mm, "end": v(10.55, 8) * mm});
            skLineSegment(sketch, "E25.0.1.177", {"start": v(7.45, 8) * mm, "end": v(6.75, 8) * mm});
            skLineSegment(sketch, "E25.0.1.178", {"start": v(3.65, 8) * mm, "end": v(2.95, 8) * mm});
            skLineSegment(sketch, "E25.0.1.179", {"start": v(-0.15, 8) * mm, "end": v(-0.85, 8) * mm});
            skLineSegment(sketch, "E25.0.1.180", {"start": v(-3.95, 8) * mm, "end": v(-3.95, 10) * mm});
            skLineSegment(sketch, "E25.0.1.181", {"start": v(-7.75, 8) * mm, "end": v(-7.75, 10) * mm});
            skLineSegment(sketch, "E25.0.1.182", {"start": v(-11.55, 8) * mm, "end": v(-11.55, 10) * mm});
            skLineSegment(sketch, "E25.0.1.184", {"start": v(3.65, 8) * mm, "end": v(3.65, 10) * mm});
            skLineSegment(sketch, "E25.0.1.185", {"start": v(-0.15, 8) * mm, "end": v(-0.15, 10) * mm});
            skLineSegment(sketch, "E25.0.1.186", {"start": v(-4.65, 8) * mm, "end": v(-4.65, 10) * mm});
            skLineSegment(sketch, "E25.0.1.187", {"start": v(-8.45, 8) * mm, "end": v(-8.45, 10) * mm});
            skLineSegment(sketch, "E25.0.1.188", {"start": v(-12.25, 8) * mm, "end": v(-12.25, 10) * mm});
            skLineSegment(sketch, "E25.0.1.189", {"start": v(2.95, 8) * mm, "end": v(2.95, 10) * mm});
            skLineSegment(sketch, "E25.0.1.190", {"start": v(-0.85, 8) * mm, "end": v(-0.85, 10) * mm});
            skLineSegment(sketch, "E25.0.1.191", {"start": v(-3.95, 10) * mm, "end": v(-4.65, 10) * mm});
            skLineSegment(sketch, "E25.0.1.192", {"start": v(-7.75, 10) * mm, "end": v(-8.45, 10) * mm});
            skLineSegment(sketch, "E25.0.1.193", {"start": v(-11.55, 10) * mm, "end": v(-12.25, 10) * mm});
            skLineSegment(sketch, "E25.0.1.194", {"start": v(3.65, 10) * mm, "end": v(2.95, 10) * mm});
            skLineSegment(sketch, "E25.0.1.195", {"start": v(-0.15, 10) * mm, "end": v(-0.85, 10) * mm});
            skLineSegment(sketch, "E25.0.1.196", {"start": v(0.8, 8) * mm, "end": v(0.8, 10) * mm});
            skLineSegment(sketch, "E25.0.1.197", {"start": v(-3, 8) * mm, "end": v(-3, 10) * mm});
            skLineSegment(sketch, "E25.0.1.198", {"start": v(-6.8, 8) * mm, "end": v(-6.8, 10) * mm});
            skLineSegment(sketch, "E25.0.1.199", {"start": v(-10.6, 8) * mm, "end": v(-10.6, 10) * mm});
            skLineSegment(sketch, "E25.0.1.200", {"start": v(1.75, 8) * mm, "end": v(1.75, 10) * mm});
            skLineSegment(sketch, "E25.0.1.201", {"start": v(-2.05, 8) * mm, "end": v(-2.05, 10) * mm});
            skLineSegment(sketch, "E25.0.1.202", {"start": v(-5.85, 8) * mm, "end": v(-5.85, 10) * mm});
            skLineSegment(sketch, "E25.0.1.204", {"start": v(5.55, 8) * mm, "end": v(5.55, 10) * mm});
            skLineSegment(sketch, "E25.0.1.206", {"start": v(-3, 8) * mm, "end": v(-3.7, 8) * mm});
            skLineSegment(sketch, "E25.0.1.207", {"start": v(-6.8, 8) * mm, "end": v(-7.5, 8) * mm});
            skLineSegment(sketch, "E25.0.1.208", {"start": v(-10.6, 8) * mm, "end": v(-11.3, 8) * mm});
            skLineSegment(sketch, "E25.0.1.210", {"start": v(12.2, 8) * mm, "end": v(11.5, 8) * mm});
            skLineSegment(sketch, "E25.0.1.211", {"start": v(8.4, 8) * mm, "end": v(7.7, 8) * mm});
            skLineSegment(sketch, "E25.0.1.212", {"start": v(4.6, 8) * mm, "end": v(3.9, 8) * mm});
            skLineSegment(sketch, "E25.0.1.213", {"start": v(0.8, 8) * mm, "end": v(0.1, 8) * mm});
            skLineSegment(sketch, "E25.0.1.214", {"start": v(0.1, 8) * mm, "end": v(0.1, 10) * mm});
            skLineSegment(sketch, "E25.0.1.215", {"start": v(-3.7, 8) * mm, "end": v(-3.7, 10) * mm});
            skLineSegment(sketch, "E25.0.1.216", {"start": v(-7.5, 8) * mm, "end": v(-7.5, 10) * mm});
            skLineSegment(sketch, "E25.0.1.217", {"start": v(-11.3, 8) * mm, "end": v(-11.3, 10) * mm});
            skLineSegment(sketch, "E25.0.1.218", {"start": v(3.9, 8) * mm, "end": v(3.9, 10) * mm});
            skLineSegment(sketch, "E25.0.1.219", {"start": v(1.05, 8) * mm, "end": v(1.05, 10) * mm});
            skLineSegment(sketch, "E25.0.1.220", {"start": v(-2.75, 8) * mm, "end": v(-2.75, 10) * mm});
            skLineSegment(sketch, "E25.0.1.221", {"start": v(-6.55, 8) * mm, "end": v(-6.55, 10) * mm});
            skLineSegment(sketch, "E25.0.1.222", {"start": v(-10.35, 8) * mm, "end": v(-10.35, 10) * mm});
            skLineSegment(sketch, "E25.0.1.224", {"start": v(8.65, 8) * mm, "end": v(8.65, 10) * mm});
            skLineSegment(sketch, "E25.0.1.225", {"start": v(-9.65, 8) * mm, "end": v(-9.65, 10) * mm});
            skPoint(sketch, "E25.0.2.0", {"position": v(-4.3, 6.75) * mm});
            skPoint(sketch, "E25.0.2.1", {"position": v(10.9, 6.75) * mm});
            skPoint(sketch, "E25.0.2.2", {"position": v(11.85, 6.75) * mm});
            skPoint(sketch, "E25.0.2.3", {"position": v(-3.35, 6.75) * mm});
            skPoint(sketch, "E25.0.2.4", {"position": v(12.8, 6.75) * mm});
            skPoint(sketch, "E25.0.2.5", {"position": v(-2.4, 6.75) * mm});
            skPoint(sketch, "E25.0.2.6", {"position": v(13.75, 6.75) * mm});
            skPoint(sketch, "E25.0.2.7", {"position": v(-1.45, 6.75) * mm});
            skPoint(sketch, "E25.0.2.8", {"position": v(14.7, 6.75) * mm});
            skPoint(sketch, "E25.0.2.9", {"position": v(-0.5, 6.75) * mm});
            skPoint(sketch, "E25.0.2.11", {"position": v(15.65, 6.75) * mm});
            skPoint(sketch, "E25.0.2.12", {"position": v(0.45, 6.75) * mm});
            skPoint(sketch, "E25.0.2.14", {"position": v(16.6, 6.75) * mm});
            skPoint(sketch, "E25.0.2.15", {"position": v(1.4, 6.75) * mm});
            skPoint(sketch, "E25.0.2.17", {"position": v(17.55, 6.75) * mm});
            skPoint(sketch, "E25.0.2.18", {"position": v(2.35, 6.75) * mm});
            skPoint(sketch, "E25.0.2.19", {"position": v(-11.9, 6.75) * mm});
            skPoint(sketch, "E25.0.2.20", {"position": v(18.5, 6.75) * mm});
            skPoint(sketch, "E25.0.2.21", {"position": v(3.3, 6.75) * mm});
            skPoint(sketch, "E25.0.2.23", {"position": v(-10.95, 6.75) * mm});
            skPoint(sketch, "E25.0.2.25", {"position": v(4.25, 6.75) * mm});
            skPoint(sketch, "E25.0.2.26", {"position": v(9.95, 6.75) * mm});
            skPoint(sketch, "E25.0.2.27", {"position": v(6.15, 6.75) * mm});
            skPoint(sketch, "E25.0.2.28", {"position": v(-9.05, 6.75) * mm});
            skPoint(sketch, "E25.0.2.30", {"position": v(-5.25, 6.75) * mm});
            skPoint(sketch, "E25.0.2.31", {"position": v(-6.2, 6.75) * mm});
            skPoint(sketch, "E25.0.2.32", {"position": v(9, 6.75) * mm});
            skPoint(sketch, "E25.0.2.38", {"position": v(8.05, 6.75) * mm});
            skPoint(sketch, "E25.0.2.39", {"position": v(-7.15, 6.75) * mm});
            skPoint(sketch, "E25.0.2.40", {"position": v(5.2, 6.75) * mm});
            skPoint(sketch, "E25.0.2.41", {"position": v(-10, 6.75) * mm});
            skPoint(sketch, "E25.0.2.44", {"position": v(7.1, 6.75) * mm});
            skPoint(sketch, "E25.0.2.45", {"position": v(-8.1, 6.75) * mm});
            skLineSegment(sketch, "E25.0.2.54", {"start": v(18.85, 5.75) * mm, "end": v(18.15, 5.75) * mm});
            skLineSegment(sketch, "E25.0.2.55", {"start": v(18.85, 5.75) * mm, "end": v(18.85, 7.75) * mm});
            skLineSegment(sketch, "E25.0.2.56", {"start": v(18.15, 5.75) * mm, "end": v(18.15, 7.75) * mm});
            skLineSegment(sketch, "E25.0.2.67", {"start": v(17.9, 5.75) * mm, "end": v(17.2, 5.75) * mm});
            skLineSegment(sketch, "E25.0.2.69", {"start": v(17.9, 5.75) * mm, "end": v(17.9, 7.75) * mm});
            skLineSegment(sketch, "E25.0.2.71", {"start": v(17.2, 5.75) * mm, "end": v(17.2, 7.75) * mm});
            skLineSegment(sketch, "E25.0.2.72", {"start": v(16.95, 5.75) * mm, "end": v(16.25, 5.75) * mm});
            skLineSegment(sketch, "E25.0.2.74", {"start": v(16.95, 5.75) * mm, "end": v(16.95, 7.75) * mm});
            skLineSegment(sketch, "E25.0.2.79", {"start": v(16.25, 5.75) * mm, "end": v(16.25, 7.75) * mm});
            skLineSegment(sketch, "E25.0.2.80", {"start": v(16, 7.75) * mm, "end": v(15.3, 7.75) * mm});
            skLineSegment(sketch, "E25.0.2.81", {"start": v(12.2, 7.75) * mm, "end": v(11.5, 7.75) * mm});
            skLineSegment(sketch, "E25.0.2.83", {"start": v(16.95, 7.75) * mm, "end": v(16.25, 7.75) * mm});
            skLineSegment(sketch, "E25.0.2.84", {"start": v(13.15, 7.75) * mm, "end": v(12.45, 7.75) * mm});
            skLineSegment(sketch, "E25.0.2.85", {"start": v(9.35, 7.75) * mm, "end": v(8.65, 7.75) * mm});
            skLineSegment(sketch, "E25.0.2.86", {"start": v(5.55, 7.75) * mm, "end": v(4.85, 7.75) * mm});
            skLineSegment(sketch, "E25.0.2.87", {"start": v(8.4, 7.75) * mm, "end": v(7.7, 7.75) * mm});
            skLineSegment(sketch, "E25.0.2.90", {"start": v(13.4, 5.75) * mm, "end": v(13.4, 7.75) * mm});
            skLineSegment(sketch, "E25.0.2.91", {"start": v(9.6, 5.75) * mm, "end": v(9.6, 7.75) * mm});
            skLineSegment(sketch, "E25.0.2.92", {"start": v(5.8, 5.75) * mm, "end": v(5.8, 7.75) * mm});
            skLineSegment(sketch, "E25.0.2.94", {"start": v(10.3, 7.75) * mm, "end": v(9.6, 7.75) * mm});
            skLineSegment(sketch, "E25.0.2.95", {"start": v(6.5, 7.75) * mm, "end": v(5.8, 7.75) * mm});
            skLineSegment(sketch, "E25.0.2.96", {"start": v(17.9, 7.75) * mm, "end": v(17.2, 7.75) * mm});
            skLineSegment(sketch, "E25.0.2.97", {"start": v(14.1, 7.75) * mm, "end": v(13.4, 7.75) * mm});
            skLineSegment(sketch, "E25.0.2.99", {"start": v(15.05, 5.75) * mm, "end": v(14.35, 5.75) * mm});
            skLineSegment(sketch, "E25.0.2.100", {"start": v(11.25, 5.75) * mm, "end": v(11.25, 7.75) * mm});
            skLineSegment(sketch, "E25.0.2.101", {"start": v(7.45, 5.75) * mm, "end": v(7.45, 7.75) * mm});
            skLineSegment(sketch, "E25.0.2.102", {"start": v(15.05, 5.75) * mm, "end": v(15.05, 7.75) * mm});
            skLineSegment(sketch, "E25.0.2.104", {"start": v(10.55, 5.75) * mm, "end": v(10.55, 7.75) * mm});
            skLineSegment(sketch, "E25.0.2.105", {"start": v(6.75, 5.75) * mm, "end": v(6.75, 7.75) * mm});
            skLineSegment(sketch, "E25.0.2.106", {"start": v(14.35, 5.75) * mm, "end": v(14.35, 7.75) * mm});
            skLineSegment(sketch, "E25.0.2.108", {"start": v(11.25, 7.75) * mm, "end": v(10.55, 7.75) * mm});
            skLineSegment(sketch, "E25.0.2.109", {"start": v(7.45, 7.75) * mm, "end": v(6.75, 7.75) * mm});
            skLineSegment(sketch, "E25.0.2.110", {"start": v(18.85, 7.75) * mm, "end": v(18.15, 7.75) * mm});
            skLineSegment(sketch, "E25.0.2.111", {"start": v(15.05, 7.75) * mm, "end": v(14.35, 7.75) * mm});
            skLineSegment(sketch, "E25.0.2.113", {"start": v(16, 5.75) * mm, "end": v(16, 7.75) * mm});
            skLineSegment(sketch, "E25.0.2.114", {"start": v(12.2, 5.75) * mm, "end": v(12.2, 7.75) * mm});
            skLineSegment(sketch, "E25.0.2.115", {"start": v(8.4, 5.75) * mm, "end": v(8.4, 7.75) * mm});
            skLineSegment(sketch, "E25.0.2.116", {"start": v(4.6, 5.75) * mm, "end": v(4.6, 7.75) * mm});
            skLineSegment(sketch, "E25.0.2.117", {"start": v(13.15, 5.75) * mm, "end": v(13.15, 7.75) * mm});
            skLineSegment(sketch, "E25.0.2.118", {"start": v(9.35, 5.75) * mm, "end": v(9.35, 7.75) * mm});
            skLineSegment(sketch, "E25.0.2.119", {"start": v(16, 5.75) * mm, "end": v(15.3, 5.75) * mm});
            skLineSegment(sketch, "E25.0.2.121", {"start": v(15.3, 5.75) * mm, "end": v(15.3, 7.75) * mm});
            skLineSegment(sketch, "E25.0.2.122", {"start": v(11.5, 5.75) * mm, "end": v(11.5, 7.75) * mm});
            skLineSegment(sketch, "E25.0.2.123", {"start": v(7.7, 5.75) * mm, "end": v(7.7, 7.75) * mm});
            skLineSegment(sketch, "E25.0.2.127", {"start": v(4.85, 5.75) * mm, "end": v(4.85, 7.75) * mm});
            skLineSegment(sketch, "E25.0.2.128", {"start": v(12.45, 5.75) * mm, "end": v(12.45, 7.75) * mm});
            skLineSegment(sketch, "E25.0.2.129", {"start": v(-10.6, 7.75) * mm, "end": v(-11.3, 7.75) * mm});
            skLineSegment(sketch, "E25.0.2.130", {"start": v(-6.8, 7.75) * mm, "end": v(-7.5, 7.75) * mm});
            skLineSegment(sketch, "E25.0.2.131", {"start": v(1.75, 7.75) * mm, "end": v(1.05, 7.75) * mm});
            skLineSegment(sketch, "E25.0.2.132", {"start": v(-2.05, 7.75) * mm, "end": v(-2.75, 7.75) * mm});
            skLineSegment(sketch, "E25.0.2.133", {"start": v(-5.85, 7.75) * mm, "end": v(-6.55, 7.75) * mm});
            skLineSegment(sketch, "E25.0.2.134", {"start": v(0.8, 7.75) * mm, "end": v(0.1, 7.75) * mm});
            skLineSegment(sketch, "E25.0.2.135", {"start": v(-9.65, 7.75) * mm, "end": v(-10.35, 7.75) * mm});
            skLineSegment(sketch, "E25.0.2.136", {"start": v(-3, 7.75) * mm, "end": v(-3.7, 7.75) * mm});
            skLineSegment(sketch, "E25.0.2.139", {"start": v(2.7, 5.75) * mm, "end": v(2, 5.75) * mm});
            skLineSegment(sketch, "E25.0.2.140", {"start": v(-4.9, 5.75) * mm, "end": v(-5.6, 5.75) * mm});
            skLineSegment(sketch, "E25.0.2.141", {"start": v(-1.1, 5.75) * mm, "end": v(-1.8, 5.75) * mm});
            skLineSegment(sketch, "E25.0.2.142", {"start": v(-8.7, 5.75) * mm, "end": v(-9.4, 5.75) * mm});
            skLineSegment(sketch, "E25.0.2.143", {"start": v(14.1, 5.75) * mm, "end": v(13.4, 5.75) * mm});
            skLineSegment(sketch, "E25.0.2.144", {"start": v(10.3, 5.75) * mm, "end": v(9.6, 5.75) * mm});
            skLineSegment(sketch, "E25.0.2.145", {"start": v(6.5, 5.75) * mm, "end": v(5.8, 5.75) * mm});
            skLineSegment(sketch, "E25.0.2.147", {"start": v(4.6, 7.75) * mm, "end": v(3.9, 7.75) * mm});
            skLineSegment(sketch, "E25.0.2.148", {"start": v(2.7, 5.75) * mm, "end": v(2.7, 7.75) * mm});
            skLineSegment(sketch, "E25.0.2.149", {"start": v(-1.1, 5.75) * mm, "end": v(-1.1, 7.75) * mm});
            skLineSegment(sketch, "E25.0.2.150", {"start": v(-4.9, 5.75) * mm, "end": v(-4.9, 7.75) * mm});
            skLineSegment(sketch, "E25.0.2.151", {"start": v(-8.7, 5.75) * mm, "end": v(-8.7, 7.75) * mm});
            skLineSegment(sketch, "E25.0.2.152", {"start": v(14.1, 5.75) * mm, "end": v(14.1, 7.75) * mm});
            skLineSegment(sketch, "E25.0.2.153", {"start": v(10.3, 5.75) * mm, "end": v(10.3, 7.75) * mm});
            skLineSegment(sketch, "E25.0.2.154", {"start": v(6.5, 5.75) * mm, "end": v(6.5, 7.75) * mm});
            skLineSegment(sketch, "E25.0.2.157", {"start": v(2, 5.75) * mm, "end": v(2, 7.75) * mm});
            skLineSegment(sketch, "E25.0.2.158", {"start": v(-1.8, 5.75) * mm, "end": v(-1.8, 7.75) * mm});
            skLineSegment(sketch, "E25.0.2.159", {"start": v(-5.6, 5.75) * mm, "end": v(-5.6, 7.75) * mm});
            skLineSegment(sketch, "E25.0.2.160", {"start": v(-9.4, 5.75) * mm, "end": v(-9.4, 7.75) * mm});
            skLineSegment(sketch, "E25.0.2.161", {"start": v(1.75, 5.75) * mm, "end": v(1.05, 5.75) * mm});
            skLineSegment(sketch, "E25.0.2.162", {"start": v(-2.05, 5.75) * mm, "end": v(-2.75, 5.75) * mm});
            skLineSegment(sketch, "E25.0.2.163", {"start": v(-5.85, 5.75) * mm, "end": v(-6.55, 5.75) * mm});
            skLineSegment(sketch, "E25.0.2.164", {"start": v(-9.65, 5.75) * mm, "end": v(-10.35, 5.75) * mm});
            skLineSegment(sketch, "E25.0.2.165", {"start": v(-4.9, 7.75) * mm, "end": v(-5.6, 7.75) * mm});
            skLineSegment(sketch, "E25.0.2.166", {"start": v(-8.7, 7.75) * mm, "end": v(-9.4, 7.75) * mm});
            skLineSegment(sketch, "E25.0.2.167", {"start": v(2.7, 7.75) * mm, "end": v(2, 7.75) * mm});
            skLineSegment(sketch, "E25.0.2.168", {"start": v(13.15, 5.75) * mm, "end": v(12.45, 5.75) * mm});
            skLineSegment(sketch, "E25.0.2.169", {"start": v(9.35, 5.75) * mm, "end": v(8.65, 5.75) * mm});
            skLineSegment(sketch, "E25.0.2.170", {"start": v(-1.1, 7.75) * mm, "end": v(-1.8, 7.75) * mm});
            skLineSegment(sketch, "E25.0.2.171", {"start": v(5.55, 5.75) * mm, "end": v(4.85, 5.75) * mm});
            skLineSegment(sketch, "E25.0.2.172", {"start": v(-3.95, 5.75) * mm, "end": v(-4.65, 5.75) * mm});
            skLineSegment(sketch, "E25.0.2.173", {"start": v(-7.75, 5.75) * mm, "end": v(-8.45, 5.75) * mm});
            skLineSegment(sketch, "E25.0.2.174", {"start": v(-11.55, 5.75) * mm, "end": v(-12.25, 5.75) * mm});
            skLineSegment(sketch, "E25.0.2.176", {"start": v(11.25, 5.75) * mm, "end": v(10.55, 5.75) * mm});
            skLineSegment(sketch, "E25.0.2.177", {"start": v(7.45, 5.75) * mm, "end": v(6.75, 5.75) * mm});
            skLineSegment(sketch, "E25.0.2.178", {"start": v(3.65, 5.75) * mm, "end": v(2.95, 5.75) * mm});
            skLineSegment(sketch, "E25.0.2.179", {"start": v(-0.15, 5.75) * mm, "end": v(-0.85, 5.75) * mm});
            skLineSegment(sketch, "E25.0.2.180", {"start": v(-3.95, 5.75) * mm, "end": v(-3.95, 7.75) * mm});
            skLineSegment(sketch, "E25.0.2.181", {"start": v(-7.75, 5.75) * mm, "end": v(-7.75, 7.75) * mm});
            skLineSegment(sketch, "E25.0.2.182", {"start": v(-11.55, 5.75) * mm, "end": v(-11.55, 7.75) * mm});
            skLineSegment(sketch, "E25.0.2.184", {"start": v(3.65, 5.75) * mm, "end": v(3.65, 7.75) * mm});
            skLineSegment(sketch, "E25.0.2.185", {"start": v(-0.15, 5.75) * mm, "end": v(-0.15, 7.75) * mm});
            skLineSegment(sketch, "E25.0.2.186", {"start": v(-4.65, 5.75) * mm, "end": v(-4.65, 7.75) * mm});
            skLineSegment(sketch, "E25.0.2.187", {"start": v(-8.45, 5.75) * mm, "end": v(-8.45, 7.75) * mm});
            skLineSegment(sketch, "E25.0.2.188", {"start": v(-12.25, 5.75) * mm, "end": v(-12.25, 7.75) * mm});
            skLineSegment(sketch, "E25.0.2.189", {"start": v(2.95, 5.75) * mm, "end": v(2.95, 7.75) * mm});
            skLineSegment(sketch, "E25.0.2.190", {"start": v(-0.85, 5.75) * mm, "end": v(-0.85, 7.75) * mm});
            skLineSegment(sketch, "E25.0.2.191", {"start": v(-3.95, 7.75) * mm, "end": v(-4.65, 7.75) * mm});
            skLineSegment(sketch, "E25.0.2.192", {"start": v(-7.75, 7.75) * mm, "end": v(-8.45, 7.75) * mm});
            skLineSegment(sketch, "E25.0.2.193", {"start": v(-11.55, 7.75) * mm, "end": v(-12.25, 7.75) * mm});
            skLineSegment(sketch, "E25.0.2.194", {"start": v(3.65, 7.75) * mm, "end": v(2.95, 7.75) * mm});
            skLineSegment(sketch, "E25.0.2.195", {"start": v(-0.15, 7.75) * mm, "end": v(-0.85, 7.75) * mm});
            skLineSegment(sketch, "E25.0.2.196", {"start": v(0.8, 5.75) * mm, "end": v(0.8, 7.75) * mm});
            skLineSegment(sketch, "E25.0.2.197", {"start": v(-3, 5.75) * mm, "end": v(-3, 7.75) * mm});
            skLineSegment(sketch, "E25.0.2.198", {"start": v(-6.8, 5.75) * mm, "end": v(-6.8, 7.75) * mm});
            skLineSegment(sketch, "E25.0.2.199", {"start": v(-10.6, 5.75) * mm, "end": v(-10.6, 7.75) * mm});
            skLineSegment(sketch, "E25.0.2.200", {"start": v(1.75, 5.75) * mm, "end": v(1.75, 7.75) * mm});
            skLineSegment(sketch, "E25.0.2.201", {"start": v(-2.05, 5.75) * mm, "end": v(-2.05, 7.75) * mm});
            skLineSegment(sketch, "E25.0.2.202", {"start": v(-5.85, 5.75) * mm, "end": v(-5.85, 7.75) * mm});
            skLineSegment(sketch, "E25.0.2.204", {"start": v(5.55, 5.75) * mm, "end": v(5.55, 7.75) * mm});
            skLineSegment(sketch, "E25.0.2.206", {"start": v(-3, 5.75) * mm, "end": v(-3.7, 5.75) * mm});
            skLineSegment(sketch, "E25.0.2.207", {"start": v(-6.8, 5.75) * mm, "end": v(-7.5, 5.75) * mm});
            skLineSegment(sketch, "E25.0.2.208", {"start": v(-10.6, 5.75) * mm, "end": v(-11.3, 5.75) * mm});
            skLineSegment(sketch, "E25.0.2.210", {"start": v(12.2, 5.75) * mm, "end": v(11.5, 5.75) * mm});
            skLineSegment(sketch, "E25.0.2.211", {"start": v(8.4, 5.75) * mm, "end": v(7.7, 5.75) * mm});
            skLineSegment(sketch, "E25.0.2.212", {"start": v(4.6, 5.75) * mm, "end": v(3.9, 5.75) * mm});
            skLineSegment(sketch, "E25.0.2.213", {"start": v(0.8, 5.75) * mm, "end": v(0.1, 5.75) * mm});
            skLineSegment(sketch, "E25.0.2.214", {"start": v(0.1, 5.75) * mm, "end": v(0.1, 7.75) * mm});
            skLineSegment(sketch, "E25.0.2.215", {"start": v(-3.7, 5.75) * mm, "end": v(-3.7, 7.75) * mm});
            skLineSegment(sketch, "E25.0.2.216", {"start": v(-7.5, 5.75) * mm, "end": v(-7.5, 7.75) * mm});
            skLineSegment(sketch, "E25.0.2.217", {"start": v(-11.3, 5.75) * mm, "end": v(-11.3, 7.75) * mm});
            skLineSegment(sketch, "E25.0.2.218", {"start": v(3.9, 5.75) * mm, "end": v(3.9, 7.75) * mm});
            skLineSegment(sketch, "E25.0.2.219", {"start": v(1.05, 5.75) * mm, "end": v(1.05, 7.75) * mm});
            skLineSegment(sketch, "E25.0.2.220", {"start": v(-2.75, 5.75) * mm, "end": v(-2.75, 7.75) * mm});
            skLineSegment(sketch, "E25.0.2.221", {"start": v(-6.55, 5.75) * mm, "end": v(-6.55, 7.75) * mm});
            skLineSegment(sketch, "E25.0.2.222", {"start": v(-10.35, 5.75) * mm, "end": v(-10.35, 7.75) * mm});
            skLineSegment(sketch, "E25.0.2.224", {"start": v(8.65, 5.75) * mm, "end": v(8.65, 7.75) * mm});
            skLineSegment(sketch, "E25.0.2.225", {"start": v(-9.65, 5.75) * mm, "end": v(-9.65, 7.75) * mm});
            skPoint(sketch, "E25.0.3.0", {"position": v(-4.3, 4.5) * mm});
            skPoint(sketch, "E25.0.3.1", {"position": v(10.9, 4.5) * mm});
            skPoint(sketch, "E25.0.3.2", {"position": v(11.85, 4.5) * mm});
            skPoint(sketch, "E25.0.3.3", {"position": v(-3.35, 4.5) * mm});
            skPoint(sketch, "E25.0.3.4", {"position": v(12.8, 4.5) * mm});
            skPoint(sketch, "E25.0.3.5", {"position": v(-2.4, 4.5) * mm});
            skPoint(sketch, "E25.0.3.6", {"position": v(13.75, 4.5) * mm});
            skPoint(sketch, "E25.0.3.7", {"position": v(-1.45, 4.5) * mm});
            skPoint(sketch, "E25.0.3.8", {"position": v(14.7, 4.5) * mm});
            skPoint(sketch, "E25.0.3.9", {"position": v(-0.5, 4.5) * mm});
            skPoint(sketch, "E25.0.3.11", {"position": v(15.65, 4.5) * mm});
            skPoint(sketch, "E25.0.3.12", {"position": v(0.45, 4.5) * mm});
            skPoint(sketch, "E25.0.3.14", {"position": v(16.6, 4.5) * mm});
            skPoint(sketch, "E25.0.3.15", {"position": v(1.4, 4.5) * mm});
            skPoint(sketch, "E25.0.3.17", {"position": v(17.55, 4.5) * mm});
            skPoint(sketch, "E25.0.3.18", {"position": v(2.35, 4.5) * mm});
            skPoint(sketch, "E25.0.3.19", {"position": v(-11.9, 4.5) * mm});
            skPoint(sketch, "E25.0.3.20", {"position": v(18.5, 4.5) * mm});
            skPoint(sketch, "E25.0.3.21", {"position": v(3.3, 4.5) * mm});
            skPoint(sketch, "E25.0.3.23", {"position": v(-10.95, 4.5) * mm});
            skPoint(sketch, "E25.0.3.25", {"position": v(4.25, 4.5) * mm});
            skPoint(sketch, "E25.0.3.26", {"position": v(9.95, 4.5) * mm});
            skPoint(sketch, "E25.0.3.27", {"position": v(6.15, 4.5) * mm});
            skPoint(sketch, "E25.0.3.28", {"position": v(-9.05, 4.5) * mm});
            skPoint(sketch, "E25.0.3.30", {"position": v(-5.25, 4.5) * mm});
            skPoint(sketch, "E25.0.3.31", {"position": v(-6.2, 4.5) * mm});
            skPoint(sketch, "E25.0.3.32", {"position": v(9, 4.5) * mm});
            skPoint(sketch, "E25.0.3.38", {"position": v(8.05, 4.5) * mm});
            skPoint(sketch, "E25.0.3.39", {"position": v(-7.15, 4.5) * mm});
            skPoint(sketch, "E25.0.3.40", {"position": v(5.2, 4.5) * mm});
            skPoint(sketch, "E25.0.3.41", {"position": v(-10, 4.5) * mm});
            skPoint(sketch, "E25.0.3.44", {"position": v(7.1, 4.5) * mm});
            skPoint(sketch, "E25.0.3.45", {"position": v(-8.1, 4.5) * mm});
            skLineSegment(sketch, "E25.0.3.54", {"start": v(18.85, 3.5) * mm, "end": v(18.15, 3.5) * mm});
            skLineSegment(sketch, "E25.0.3.55", {"start": v(18.85, 3.5) * mm, "end": v(18.85, 5.5) * mm});
            skLineSegment(sketch, "E25.0.3.56", {"start": v(18.15, 3.5) * mm, "end": v(18.15, 5.5) * mm});
            skLineSegment(sketch, "E25.0.3.67", {"start": v(17.9, 3.5) * mm, "end": v(17.2, 3.5) * mm});
            skLineSegment(sketch, "E25.0.3.69", {"start": v(17.9, 3.5) * mm, "end": v(17.9, 5.5) * mm});
            skLineSegment(sketch, "E25.0.3.71", {"start": v(17.2, 3.5) * mm, "end": v(17.2, 5.5) * mm});
            skLineSegment(sketch, "E25.0.3.72", {"start": v(16.95, 3.5) * mm, "end": v(16.25, 3.5) * mm});
            skLineSegment(sketch, "E25.0.3.74", {"start": v(16.95, 3.5) * mm, "end": v(16.95, 5.5) * mm});
            skLineSegment(sketch, "E25.0.3.79", {"start": v(16.25, 3.5) * mm, "end": v(16.25, 5.5) * mm});
            skLineSegment(sketch, "E25.0.3.80", {"start": v(16, 5.5) * mm, "end": v(15.3, 5.5) * mm});
            skLineSegment(sketch, "E25.0.3.81", {"start": v(12.2, 5.5) * mm, "end": v(11.5, 5.5) * mm});
            skLineSegment(sketch, "E25.0.3.83", {"start": v(16.95, 5.5) * mm, "end": v(16.25, 5.5) * mm});
            skLineSegment(sketch, "E25.0.3.84", {"start": v(13.15, 5.5) * mm, "end": v(12.45, 5.5) * mm});
            skLineSegment(sketch, "E25.0.3.85", {"start": v(9.35, 5.5) * mm, "end": v(8.65, 5.5) * mm});
            skLineSegment(sketch, "E25.0.3.86", {"start": v(5.55, 5.5) * mm, "end": v(4.85, 5.5) * mm});
            skLineSegment(sketch, "E25.0.3.87", {"start": v(8.4, 5.5) * mm, "end": v(7.7, 5.5) * mm});
            skLineSegment(sketch, "E25.0.3.90", {"start": v(13.4, 3.5) * mm, "end": v(13.4, 5.5) * mm});
            skLineSegment(sketch, "E25.0.3.91", {"start": v(9.6, 3.5) * mm, "end": v(9.6, 5.5) * mm});
            skLineSegment(sketch, "E25.0.3.92", {"start": v(5.8, 3.5) * mm, "end": v(5.8, 5.5) * mm});
            skLineSegment(sketch, "E25.0.3.94", {"start": v(10.3, 5.5) * mm, "end": v(9.6, 5.5) * mm});
            skLineSegment(sketch, "E25.0.3.95", {"start": v(6.5, 5.5) * mm, "end": v(5.8, 5.5) * mm});
            skLineSegment(sketch, "E25.0.3.96", {"start": v(17.9, 5.5) * mm, "end": v(17.2, 5.5) * mm});
            skLineSegment(sketch, "E25.0.3.97", {"start": v(14.1, 5.5) * mm, "end": v(13.4, 5.5) * mm});
            skLineSegment(sketch, "E25.0.3.99", {"start": v(15.05, 3.5) * mm, "end": v(14.35, 3.5) * mm});
            skLineSegment(sketch, "E25.0.3.100", {"start": v(11.25, 3.5) * mm, "end": v(11.25, 5.5) * mm});
            skLineSegment(sketch, "E25.0.3.101", {"start": v(7.45, 3.5) * mm, "end": v(7.45, 5.5) * mm});
            skLineSegment(sketch, "E25.0.3.102", {"start": v(15.05, 3.5) * mm, "end": v(15.05, 5.5) * mm});
            skLineSegment(sketch, "E25.0.3.104", {"start": v(10.55, 3.5) * mm, "end": v(10.55, 5.5) * mm});
            skLineSegment(sketch, "E25.0.3.105", {"start": v(6.75, 3.5) * mm, "end": v(6.75, 5.5) * mm});
            skLineSegment(sketch, "E25.0.3.106", {"start": v(14.35, 3.5) * mm, "end": v(14.35, 5.5) * mm});
            skLineSegment(sketch, "E25.0.3.108", {"start": v(11.25, 5.5) * mm, "end": v(10.55, 5.5) * mm});
            skLineSegment(sketch, "E25.0.3.109", {"start": v(7.45, 5.5) * mm, "end": v(6.75, 5.5) * mm});
            skLineSegment(sketch, "E25.0.3.110", {"start": v(18.85, 5.5) * mm, "end": v(18.15, 5.5) * mm});
            skLineSegment(sketch, "E25.0.3.111", {"start": v(15.05, 5.5) * mm, "end": v(14.35, 5.5) * mm});
            skLineSegment(sketch, "E25.0.3.113", {"start": v(16, 3.5) * mm, "end": v(16, 5.5) * mm});
            skLineSegment(sketch, "E25.0.3.114", {"start": v(12.2, 3.5) * mm, "end": v(12.2, 5.5) * mm});
            skLineSegment(sketch, "E25.0.3.115", {"start": v(8.4, 3.5) * mm, "end": v(8.4, 5.5) * mm});
            skLineSegment(sketch, "E25.0.3.116", {"start": v(4.6, 3.5) * mm, "end": v(4.6, 5.5) * mm});
            skLineSegment(sketch, "E25.0.3.117", {"start": v(13.15, 3.5) * mm, "end": v(13.15, 5.5) * mm});
            skLineSegment(sketch, "E25.0.3.118", {"start": v(9.35, 3.5) * mm, "end": v(9.35, 5.5) * mm});
            skLineSegment(sketch, "E25.0.3.119", {"start": v(16, 3.5) * mm, "end": v(15.3, 3.5) * mm});
            skLineSegment(sketch, "E25.0.3.121", {"start": v(15.3, 3.5) * mm, "end": v(15.3, 5.5) * mm});
            skLineSegment(sketch, "E25.0.3.122", {"start": v(11.5, 3.5) * mm, "end": v(11.5, 5.5) * mm});
            skLineSegment(sketch, "E25.0.3.123", {"start": v(7.7, 3.5) * mm, "end": v(7.7, 5.5) * mm});
            skLineSegment(sketch, "E25.0.3.127", {"start": v(4.85, 3.5) * mm, "end": v(4.85, 5.5) * mm});
            skLineSegment(sketch, "E25.0.3.128", {"start": v(12.45, 3.5) * mm, "end": v(12.45, 5.5) * mm});
            skLineSegment(sketch, "E25.0.3.129", {"start": v(-10.6, 5.5) * mm, "end": v(-11.3, 5.5) * mm});
            skLineSegment(sketch, "E25.0.3.130", {"start": v(-6.8, 5.5) * mm, "end": v(-7.5, 5.5) * mm});
            skLineSegment(sketch, "E25.0.3.131", {"start": v(1.75, 5.5) * mm, "end": v(1.05, 5.5) * mm});
            skLineSegment(sketch, "E25.0.3.132", {"start": v(-2.05, 5.5) * mm, "end": v(-2.75, 5.5) * mm});
            skLineSegment(sketch, "E25.0.3.133", {"start": v(-5.85, 5.5) * mm, "end": v(-6.55, 5.5) * mm});
            skLineSegment(sketch, "E25.0.3.134", {"start": v(0.8, 5.5) * mm, "end": v(0.1, 5.5) * mm});
            skLineSegment(sketch, "E25.0.3.135", {"start": v(-9.65, 5.5) * mm, "end": v(-10.35, 5.5) * mm});
            skLineSegment(sketch, "E25.0.3.136", {"start": v(-3, 5.5) * mm, "end": v(-3.7, 5.5) * mm});
            skLineSegment(sketch, "E25.0.3.139", {"start": v(2.7, 3.5) * mm, "end": v(2, 3.5) * mm});
            skLineSegment(sketch, "E25.0.3.140", {"start": v(-4.9, 3.5) * mm, "end": v(-5.6, 3.5) * mm});
            skLineSegment(sketch, "E25.0.3.141", {"start": v(-1.1, 3.5) * mm, "end": v(-1.8, 3.5) * mm});
            skLineSegment(sketch, "E25.0.3.142", {"start": v(-8.7, 3.5) * mm, "end": v(-9.4, 3.5) * mm});
            skLineSegment(sketch, "E25.0.3.143", {"start": v(14.1, 3.5) * mm, "end": v(13.4, 3.5) * mm});
            skLineSegment(sketch, "E25.0.3.144", {"start": v(10.3, 3.5) * mm, "end": v(9.6, 3.5) * mm});
            skLineSegment(sketch, "E25.0.3.145", {"start": v(6.5, 3.5) * mm, "end": v(5.8, 3.5) * mm});
            skLineSegment(sketch, "E25.0.3.147", {"start": v(4.6, 5.5) * mm, "end": v(3.9, 5.5) * mm});
            skLineSegment(sketch, "E25.0.3.148", {"start": v(2.7, 3.5) * mm, "end": v(2.7, 5.5) * mm});
            skLineSegment(sketch, "E25.0.3.149", {"start": v(-1.1, 3.5) * mm, "end": v(-1.1, 5.5) * mm});
            skLineSegment(sketch, "E25.0.3.150", {"start": v(-4.9, 3.5) * mm, "end": v(-4.9, 5.5) * mm});
            skLineSegment(sketch, "E25.0.3.151", {"start": v(-8.7, 3.5) * mm, "end": v(-8.7, 5.5) * mm});
            skLineSegment(sketch, "E25.0.3.152", {"start": v(14.1, 3.5) * mm, "end": v(14.1, 5.5) * mm});
            skLineSegment(sketch, "E25.0.3.153", {"start": v(10.3, 3.5) * mm, "end": v(10.3, 5.5) * mm});
            skLineSegment(sketch, "E25.0.3.154", {"start": v(6.5, 3.5) * mm, "end": v(6.5, 5.5) * mm});
            skLineSegment(sketch, "E25.0.3.157", {"start": v(2, 3.5) * mm, "end": v(2, 5.5) * mm});
            skLineSegment(sketch, "E25.0.3.158", {"start": v(-1.8, 3.5) * mm, "end": v(-1.8, 5.5) * mm});
            skLineSegment(sketch, "E25.0.3.159", {"start": v(-5.6, 3.5) * mm, "end": v(-5.6, 5.5) * mm});
            skLineSegment(sketch, "E25.0.3.160", {"start": v(-9.4, 3.5) * mm, "end": v(-9.4, 5.5) * mm});
            skLineSegment(sketch, "E25.0.3.161", {"start": v(1.75, 3.5) * mm, "end": v(1.05, 3.5) * mm});
            skLineSegment(sketch, "E25.0.3.162", {"start": v(-2.05, 3.5) * mm, "end": v(-2.75, 3.5) * mm});
            skLineSegment(sketch, "E25.0.3.163", {"start": v(-5.85, 3.5) * mm, "end": v(-6.55, 3.5) * mm});
            skLineSegment(sketch, "E25.0.3.164", {"start": v(-9.65, 3.5) * mm, "end": v(-10.35, 3.5) * mm});
            skLineSegment(sketch, "E25.0.3.165", {"start": v(-4.9, 5.5) * mm, "end": v(-5.6, 5.5) * mm});
            skLineSegment(sketch, "E25.0.3.166", {"start": v(-8.7, 5.5) * mm, "end": v(-9.4, 5.5) * mm});
            skLineSegment(sketch, "E25.0.3.167", {"start": v(2.7, 5.5) * mm, "end": v(2, 5.5) * mm});
            skLineSegment(sketch, "E25.0.3.168", {"start": v(13.15, 3.5) * mm, "end": v(12.45, 3.5) * mm});
            skLineSegment(sketch, "E25.0.3.169", {"start": v(9.35, 3.5) * mm, "end": v(8.65, 3.5) * mm});
            skLineSegment(sketch, "E25.0.3.170", {"start": v(-1.1, 5.5) * mm, "end": v(-1.8, 5.5) * mm});
            skLineSegment(sketch, "E25.0.3.171", {"start": v(5.55, 3.5) * mm, "end": v(4.85, 3.5) * mm});
            skLineSegment(sketch, "E25.0.3.172", {"start": v(-3.95, 3.5) * mm, "end": v(-4.65, 3.5) * mm});
            skLineSegment(sketch, "E25.0.3.173", {"start": v(-7.75, 3.5) * mm, "end": v(-8.45, 3.5) * mm});
            skLineSegment(sketch, "E25.0.3.174", {"start": v(-11.55, 3.5) * mm, "end": v(-12.25, 3.5) * mm});
            skLineSegment(sketch, "E25.0.3.176", {"start": v(11.25, 3.5) * mm, "end": v(10.55, 3.5) * mm});
            skLineSegment(sketch, "E25.0.3.177", {"start": v(7.45, 3.5) * mm, "end": v(6.75, 3.5) * mm});
            skLineSegment(sketch, "E25.0.3.178", {"start": v(3.65, 3.5) * mm, "end": v(2.95, 3.5) * mm});
            skLineSegment(sketch, "E25.0.3.179", {"start": v(-0.15, 3.5) * mm, "end": v(-0.85, 3.5) * mm});
            skLineSegment(sketch, "E25.0.3.180", {"start": v(-3.95, 3.5) * mm, "end": v(-3.95, 5.5) * mm});
            skLineSegment(sketch, "E25.0.3.181", {"start": v(-7.75, 3.5) * mm, "end": v(-7.75, 5.5) * mm});
            skLineSegment(sketch, "E25.0.3.182", {"start": v(-11.55, 3.5) * mm, "end": v(-11.55, 5.5) * mm});
            skLineSegment(sketch, "E25.0.3.184", {"start": v(3.65, 3.5) * mm, "end": v(3.65, 5.5) * mm});
            skLineSegment(sketch, "E25.0.3.185", {"start": v(-0.15, 3.5) * mm, "end": v(-0.15, 5.5) * mm});
            skLineSegment(sketch, "E25.0.3.186", {"start": v(-4.65, 3.5) * mm, "end": v(-4.65, 5.5) * mm});
            skLineSegment(sketch, "E25.0.3.187", {"start": v(-8.45, 3.5) * mm, "end": v(-8.45, 5.5) * mm});
            skLineSegment(sketch, "E25.0.3.188", {"start": v(-12.25, 3.5) * mm, "end": v(-12.25, 5.5) * mm});
            skLineSegment(sketch, "E25.0.3.189", {"start": v(2.95, 3.5) * mm, "end": v(2.95, 5.5) * mm});
            skLineSegment(sketch, "E25.0.3.190", {"start": v(-0.85, 3.5) * mm, "end": v(-0.85, 5.5) * mm});
            skLineSegment(sketch, "E25.0.3.191", {"start": v(-3.95, 5.5) * mm, "end": v(-4.65, 5.5) * mm});
            skLineSegment(sketch, "E25.0.3.192", {"start": v(-7.75, 5.5) * mm, "end": v(-8.45, 5.5) * mm});
            skLineSegment(sketch, "E25.0.3.193", {"start": v(-11.55, 5.5) * mm, "end": v(-12.25, 5.5) * mm});
            skLineSegment(sketch, "E25.0.3.194", {"start": v(3.65, 5.5) * mm, "end": v(2.95, 5.5) * mm});
            skLineSegment(sketch, "E25.0.3.195", {"start": v(-0.15, 5.5) * mm, "end": v(-0.85, 5.5) * mm});
            skLineSegment(sketch, "E25.0.3.196", {"start": v(0.8, 3.5) * mm, "end": v(0.8, 5.5) * mm});
            skLineSegment(sketch, "E25.0.3.197", {"start": v(-3, 3.5) * mm, "end": v(-3, 5.5) * mm});
            skLineSegment(sketch, "E25.0.3.198", {"start": v(-6.8, 3.5) * mm, "end": v(-6.8, 5.5) * mm});
            skLineSegment(sketch, "E25.0.3.199", {"start": v(-10.6, 3.5) * mm, "end": v(-10.6, 5.5) * mm});
            skLineSegment(sketch, "E25.0.3.200", {"start": v(1.75, 3.5) * mm, "end": v(1.75, 5.5) * mm});
            skLineSegment(sketch, "E25.0.3.201", {"start": v(-2.05, 3.5) * mm, "end": v(-2.05, 5.5) * mm});
            skLineSegment(sketch, "E25.0.3.202", {"start": v(-5.85, 3.5) * mm, "end": v(-5.85, 5.5) * mm});
            skLineSegment(sketch, "E25.0.3.204", {"start": v(5.55, 3.5) * mm, "end": v(5.55, 5.5) * mm});
            skLineSegment(sketch, "E25.0.3.206", {"start": v(-3, 3.5) * mm, "end": v(-3.7, 3.5) * mm});
            skLineSegment(sketch, "E25.0.3.207", {"start": v(-6.8, 3.5) * mm, "end": v(-7.5, 3.5) * mm});
            skLineSegment(sketch, "E25.0.3.208", {"start": v(-10.6, 3.5) * mm, "end": v(-11.3, 3.5) * mm});
            skLineSegment(sketch, "E25.0.3.210", {"start": v(12.2, 3.5) * mm, "end": v(11.5, 3.5) * mm});
            skLineSegment(sketch, "E25.0.3.211", {"start": v(8.4, 3.5) * mm, "end": v(7.7, 3.5) * mm});
            skLineSegment(sketch, "E25.0.3.212", {"start": v(4.6, 3.5) * mm, "end": v(3.9, 3.5) * mm});
            skLineSegment(sketch, "E25.0.3.213", {"start": v(0.8, 3.5) * mm, "end": v(0.1, 3.5) * mm});
            skLineSegment(sketch, "E25.0.3.214", {"start": v(0.1, 3.5) * mm, "end": v(0.1, 5.5) * mm});
            skLineSegment(sketch, "E25.0.3.215", {"start": v(-3.7, 3.5) * mm, "end": v(-3.7, 5.5) * mm});
            skLineSegment(sketch, "E25.0.3.216", {"start": v(-7.5, 3.5) * mm, "end": v(-7.5, 5.5) * mm});
            skLineSegment(sketch, "E25.0.3.217", {"start": v(-11.3, 3.5) * mm, "end": v(-11.3, 5.5) * mm});
            skLineSegment(sketch, "E25.0.3.218", {"start": v(3.9, 3.5) * mm, "end": v(3.9, 5.5) * mm});
            skLineSegment(sketch, "E25.0.3.219", {"start": v(1.05, 3.5) * mm, "end": v(1.05, 5.5) * mm});
            skLineSegment(sketch, "E25.0.3.220", {"start": v(-2.75, 3.5) * mm, "end": v(-2.75, 5.5) * mm});
            skLineSegment(sketch, "E25.0.3.221", {"start": v(-6.55, 3.5) * mm, "end": v(-6.55, 5.5) * mm});
            skLineSegment(sketch, "E25.0.3.222", {"start": v(-10.35, 3.5) * mm, "end": v(-10.35, 5.5) * mm});
            skLineSegment(sketch, "E25.0.3.224", {"start": v(8.65, 3.5) * mm, "end": v(8.65, 5.5) * mm});
            skLineSegment(sketch, "E25.0.3.225", {"start": v(-9.65, 3.5) * mm, "end": v(-9.65, 5.5) * mm});
            skPoint(sketch, "E25.0.4.0", {"position": v(-4.3, 2.25) * mm});
            skPoint(sketch, "E25.0.4.1", {"position": v(10.9, 2.25) * mm});
            skPoint(sketch, "E25.0.4.2", {"position": v(11.85, 2.25) * mm});
            skPoint(sketch, "E25.0.4.3", {"position": v(-3.35, 2.25) * mm});
            skPoint(sketch, "E25.0.4.4", {"position": v(12.8, 2.25) * mm});
            skPoint(sketch, "E25.0.4.5", {"position": v(-2.4, 2.25) * mm});
            skPoint(sketch, "E25.0.4.6", {"position": v(13.75, 2.25) * mm});
            skPoint(sketch, "E25.0.4.7", {"position": v(-1.45, 2.25) * mm});
            skPoint(sketch, "E25.0.4.8", {"position": v(14.7, 2.25) * mm});
            skPoint(sketch, "E25.0.4.9", {"position": v(-0.5, 2.25) * mm});
            skPoint(sketch, "E25.0.4.11", {"position": v(15.65, 2.25) * mm});
            skPoint(sketch, "E25.0.4.12", {"position": v(0.45, 2.25) * mm});
            skPoint(sketch, "E25.0.4.14", {"position": v(16.6, 2.25) * mm});
            skPoint(sketch, "E25.0.4.15", {"position": v(1.4, 2.25) * mm});
            skPoint(sketch, "E25.0.4.17", {"position": v(17.55, 2.25) * mm});
            skPoint(sketch, "E25.0.4.18", {"position": v(2.35, 2.25) * mm});
            skPoint(sketch, "E25.0.4.19", {"position": v(-11.9, 2.25) * mm});
            skPoint(sketch, "E25.0.4.20", {"position": v(18.5, 2.25) * mm});
            skPoint(sketch, "E25.0.4.21", {"position": v(3.3, 2.25) * mm});
            skPoint(sketch, "E25.0.4.23", {"position": v(-10.95, 2.25) * mm});
            skPoint(sketch, "E25.0.4.25", {"position": v(4.25, 2.25) * mm});
            skPoint(sketch, "E25.0.4.26", {"position": v(9.95, 2.25) * mm});
            skPoint(sketch, "E25.0.4.27", {"position": v(6.15, 2.25) * mm});
            skPoint(sketch, "E25.0.4.28", {"position": v(-9.05, 2.25) * mm});
            skPoint(sketch, "E25.0.4.30", {"position": v(-5.25, 2.25) * mm});
            skPoint(sketch, "E25.0.4.31", {"position": v(-6.2, 2.25) * mm});
            skPoint(sketch, "E25.0.4.32", {"position": v(9, 2.25) * mm});
            skPoint(sketch, "E25.0.4.38", {"position": v(8.05, 2.25) * mm});
            skPoint(sketch, "E25.0.4.39", {"position": v(-7.15, 2.25) * mm});
            skPoint(sketch, "E25.0.4.40", {"position": v(5.2, 2.25) * mm});
            skPoint(sketch, "E25.0.4.41", {"position": v(-10, 2.25) * mm});
            skPoint(sketch, "E25.0.4.44", {"position": v(7.1, 2.25) * mm});
            skPoint(sketch, "E25.0.4.45", {"position": v(-8.1, 2.25) * mm});
            skLineSegment(sketch, "E25.0.4.54", {"start": v(18.85, 1.25) * mm, "end": v(18.15, 1.25) * mm});
            skLineSegment(sketch, "E25.0.4.55", {"start": v(18.85, 1.25) * mm, "end": v(18.85, 3.25) * mm});
            skLineSegment(sketch, "E25.0.4.56", {"start": v(18.15, 1.25) * mm, "end": v(18.15, 3.25) * mm});
            skLineSegment(sketch, "E25.0.4.67", {"start": v(17.9, 1.25) * mm, "end": v(17.2, 1.25) * mm});
            skLineSegment(sketch, "E25.0.4.69", {"start": v(17.9, 1.25) * mm, "end": v(17.9, 3.25) * mm});
            skLineSegment(sketch, "E25.0.4.71", {"start": v(17.2, 1.25) * mm, "end": v(17.2, 3.25) * mm});
            skLineSegment(sketch, "E25.0.4.72", {"start": v(16.95, 1.25) * mm, "end": v(16.25, 1.25) * mm});
            skLineSegment(sketch, "E25.0.4.74", {"start": v(16.95, 1.25) * mm, "end": v(16.95, 3.25) * mm});
            skLineSegment(sketch, "E25.0.4.79", {"start": v(16.25, 1.25) * mm, "end": v(16.25, 3.25) * mm});
            skLineSegment(sketch, "E25.0.4.80", {"start": v(16, 3.25) * mm, "end": v(15.3, 3.25) * mm});
            skLineSegment(sketch, "E25.0.4.81", {"start": v(12.2, 3.25) * mm, "end": v(11.5, 3.25) * mm});
            skLineSegment(sketch, "E25.0.4.83", {"start": v(16.95, 3.25) * mm, "end": v(16.25, 3.25) * mm});
            skLineSegment(sketch, "E25.0.4.84", {"start": v(13.15, 3.25) * mm, "end": v(12.45, 3.25) * mm});
            skLineSegment(sketch, "E25.0.4.85", {"start": v(9.35, 3.25) * mm, "end": v(8.65, 3.25) * mm});
            skLineSegment(sketch, "E25.0.4.86", {"start": v(5.55, 3.25) * mm, "end": v(4.85, 3.25) * mm});
            skLineSegment(sketch, "E25.0.4.87", {"start": v(8.4, 3.25) * mm, "end": v(7.7, 3.25) * mm});
            skLineSegment(sketch, "E25.0.4.90", {"start": v(13.4, 1.25) * mm, "end": v(13.4, 3.25) * mm});
            skLineSegment(sketch, "E25.0.4.91", {"start": v(9.6, 1.25) * mm, "end": v(9.6, 3.25) * mm});
            skLineSegment(sketch, "E25.0.4.92", {"start": v(5.8, 1.25) * mm, "end": v(5.8, 3.25) * mm});
            skLineSegment(sketch, "E25.0.4.94", {"start": v(10.3, 3.25) * mm, "end": v(9.6, 3.25) * mm});
            skLineSegment(sketch, "E25.0.4.95", {"start": v(6.5, 3.25) * mm, "end": v(5.8, 3.25) * mm});
            skLineSegment(sketch, "E25.0.4.96", {"start": v(17.9, 3.25) * mm, "end": v(17.2, 3.25) * mm});
            skLineSegment(sketch, "E25.0.4.97", {"start": v(14.1, 3.25) * mm, "end": v(13.4, 3.25) * mm});
            skLineSegment(sketch, "E25.0.4.99", {"start": v(15.05, 1.25) * mm, "end": v(14.35, 1.25) * mm});
            skLineSegment(sketch, "E25.0.4.100", {"start": v(11.25, 1.25) * mm, "end": v(11.25, 3.25) * mm});
            skLineSegment(sketch, "E25.0.4.101", {"start": v(7.45, 1.25) * mm, "end": v(7.45, 3.25) * mm});
            skLineSegment(sketch, "E25.0.4.102", {"start": v(15.05, 1.25) * mm, "end": v(15.05, 3.25) * mm});
            skLineSegment(sketch, "E25.0.4.104", {"start": v(10.55, 1.25) * mm, "end": v(10.55, 3.25) * mm});
            skLineSegment(sketch, "E25.0.4.105", {"start": v(6.75, 1.25) * mm, "end": v(6.75, 3.25) * mm});
            skLineSegment(sketch, "E25.0.4.106", {"start": v(14.35, 1.25) * mm, "end": v(14.35, 3.25) * mm});
            skLineSegment(sketch, "E25.0.4.108", {"start": v(11.25, 3.25) * mm, "end": v(10.55, 3.25) * mm});
            skLineSegment(sketch, "E25.0.4.109", {"start": v(7.45, 3.25) * mm, "end": v(6.75, 3.25) * mm});
            skLineSegment(sketch, "E25.0.4.110", {"start": v(18.85, 3.25) * mm, "end": v(18.15, 3.25) * mm});
            skLineSegment(sketch, "E25.0.4.111", {"start": v(15.05, 3.25) * mm, "end": v(14.35, 3.25) * mm});
            skLineSegment(sketch, "E25.0.4.113", {"start": v(16, 1.25) * mm, "end": v(16, 3.25) * mm});
            skLineSegment(sketch, "E25.0.4.114", {"start": v(12.2, 1.25) * mm, "end": v(12.2, 3.25) * mm});
            skLineSegment(sketch, "E25.0.4.115", {"start": v(8.4, 1.25) * mm, "end": v(8.4, 3.25) * mm});
            skLineSegment(sketch, "E25.0.4.116", {"start": v(4.6, 1.25) * mm, "end": v(4.6, 3.25) * mm});
            skLineSegment(sketch, "E25.0.4.117", {"start": v(13.15, 1.25) * mm, "end": v(13.15, 3.25) * mm});
            skLineSegment(sketch, "E25.0.4.118", {"start": v(9.35, 1.25) * mm, "end": v(9.35, 3.25) * mm});
            skLineSegment(sketch, "E25.0.4.119", {"start": v(16, 1.25) * mm, "end": v(15.3, 1.25) * mm});
            skLineSegment(sketch, "E25.0.4.121", {"start": v(15.3, 1.25) * mm, "end": v(15.3, 3.25) * mm});
            skLineSegment(sketch, "E25.0.4.122", {"start": v(11.5, 1.25) * mm, "end": v(11.5, 3.25) * mm});
            skLineSegment(sketch, "E25.0.4.123", {"start": v(7.7, 1.25) * mm, "end": v(7.7, 3.25) * mm});
            skLineSegment(sketch, "E25.0.4.127", {"start": v(4.85, 1.25) * mm, "end": v(4.85, 3.25) * mm});
            skLineSegment(sketch, "E25.0.4.128", {"start": v(12.45, 1.25) * mm, "end": v(12.45, 3.25) * mm});
            skLineSegment(sketch, "E25.0.4.129", {"start": v(-10.6, 3.25) * mm, "end": v(-11.3, 3.25) * mm});
            skLineSegment(sketch, "E25.0.4.130", {"start": v(-6.8, 3.25) * mm, "end": v(-7.5, 3.25) * mm});
            skLineSegment(sketch, "E25.0.4.131", {"start": v(1.75, 3.25) * mm, "end": v(1.05, 3.25) * mm});
            skLineSegment(sketch, "E25.0.4.132", {"start": v(-2.05, 3.25) * mm, "end": v(-2.75, 3.25) * mm});
            skLineSegment(sketch, "E25.0.4.133", {"start": v(-5.85, 3.25) * mm, "end": v(-6.55, 3.25) * mm});
            skLineSegment(sketch, "E25.0.4.134", {"start": v(0.8, 3.25) * mm, "end": v(0.1, 3.25) * mm});
            skLineSegment(sketch, "E25.0.4.135", {"start": v(-9.65, 3.25) * mm, "end": v(-10.35, 3.25) * mm});
            skLineSegment(sketch, "E25.0.4.136", {"start": v(-3, 3.25) * mm, "end": v(-3.7, 3.25) * mm});
            skLineSegment(sketch, "E25.0.4.139", {"start": v(2.7, 1.25) * mm, "end": v(2, 1.25) * mm});
            skLineSegment(sketch, "E25.0.4.140", {"start": v(-4.9, 1.25) * mm, "end": v(-5.6, 1.25) * mm});
            skLineSegment(sketch, "E25.0.4.141", {"start": v(-1.1, 1.25) * mm, "end": v(-1.8, 1.25) * mm});
            skLineSegment(sketch, "E25.0.4.142", {"start": v(-8.7, 1.25) * mm, "end": v(-9.4, 1.25) * mm});
            skLineSegment(sketch, "E25.0.4.143", {"start": v(14.1, 1.25) * mm, "end": v(13.4, 1.25) * mm});
            skLineSegment(sketch, "E25.0.4.144", {"start": v(10.3, 1.25) * mm, "end": v(9.6, 1.25) * mm});
            skLineSegment(sketch, "E25.0.4.145", {"start": v(6.5, 1.25) * mm, "end": v(5.8, 1.25) * mm});
            skLineSegment(sketch, "E25.0.4.147", {"start": v(4.6, 3.25) * mm, "end": v(3.9, 3.25) * mm});
            skLineSegment(sketch, "E25.0.4.148", {"start": v(2.7, 1.25) * mm, "end": v(2.7, 3.25) * mm});
            skLineSegment(sketch, "E25.0.4.149", {"start": v(-1.1, 1.25) * mm, "end": v(-1.1, 3.25) * mm});
            skLineSegment(sketch, "E25.0.4.150", {"start": v(-4.9, 1.25) * mm, "end": v(-4.9, 3.25) * mm});
            skLineSegment(sketch, "E25.0.4.151", {"start": v(-8.7, 1.25) * mm, "end": v(-8.7, 3.25) * mm});
            skLineSegment(sketch, "E25.0.4.152", {"start": v(14.1, 1.25) * mm, "end": v(14.1, 3.25) * mm});
            skLineSegment(sketch, "E25.0.4.153", {"start": v(10.3, 1.25) * mm, "end": v(10.3, 3.25) * mm});
            skLineSegment(sketch, "E25.0.4.154", {"start": v(6.5, 1.25) * mm, "end": v(6.5, 3.25) * mm});
            skLineSegment(sketch, "E25.0.4.157", {"start": v(2, 1.25) * mm, "end": v(2, 3.25) * mm});
            skLineSegment(sketch, "E25.0.4.158", {"start": v(-1.8, 1.25) * mm, "end": v(-1.8, 3.25) * mm});
            skLineSegment(sketch, "E25.0.4.159", {"start": v(-5.6, 1.25) * mm, "end": v(-5.6, 3.25) * mm});
            skLineSegment(sketch, "E25.0.4.160", {"start": v(-9.4, 1.25) * mm, "end": v(-9.4, 3.25) * mm});
            skLineSegment(sketch, "E25.0.4.161", {"start": v(1.75, 1.25) * mm, "end": v(1.05, 1.25) * mm});
            skLineSegment(sketch, "E25.0.4.162", {"start": v(-2.05, 1.25) * mm, "end": v(-2.75, 1.25) * mm});
            skLineSegment(sketch, "E25.0.4.163", {"start": v(-5.85, 1.25) * mm, "end": v(-6.55, 1.25) * mm});
            skLineSegment(sketch, "E25.0.4.164", {"start": v(-9.65, 1.25) * mm, "end": v(-10.35, 1.25) * mm});
            skLineSegment(sketch, "E25.0.4.165", {"start": v(-4.9, 3.25) * mm, "end": v(-5.6, 3.25) * mm});
            skLineSegment(sketch, "E25.0.4.166", {"start": v(-8.7, 3.25) * mm, "end": v(-9.4, 3.25) * mm});
            skLineSegment(sketch, "E25.0.4.167", {"start": v(2.7, 3.25) * mm, "end": v(2, 3.25) * mm});
            skLineSegment(sketch, "E25.0.4.168", {"start": v(13.15, 1.25) * mm, "end": v(12.45, 1.25) * mm});
            skLineSegment(sketch, "E25.0.4.169", {"start": v(9.35, 1.25) * mm, "end": v(8.65, 1.25) * mm});
            skLineSegment(sketch, "E25.0.4.170", {"start": v(-1.1, 3.25) * mm, "end": v(-1.8, 3.25) * mm});
            skLineSegment(sketch, "E25.0.4.171", {"start": v(5.55, 1.25) * mm, "end": v(4.85, 1.25) * mm});
            skLineSegment(sketch, "E25.0.4.172", {"start": v(-3.95, 1.25) * mm, "end": v(-4.65, 1.25) * mm});
            skLineSegment(sketch, "E25.0.4.173", {"start": v(-7.75, 1.25) * mm, "end": v(-8.45, 1.25) * mm});
            skLineSegment(sketch, "E25.0.4.174", {"start": v(-11.55, 1.25) * mm, "end": v(-12.25, 1.25) * mm});
            skLineSegment(sketch, "E25.0.4.176", {"start": v(11.25, 1.25) * mm, "end": v(10.55, 1.25) * mm});
            skLineSegment(sketch, "E25.0.4.177", {"start": v(7.45, 1.25) * mm, "end": v(6.75, 1.25) * mm});
            skLineSegment(sketch, "E25.0.4.178", {"start": v(3.65, 1.25) * mm, "end": v(2.95, 1.25) * mm});
            skLineSegment(sketch, "E25.0.4.179", {"start": v(-0.15, 1.25) * mm, "end": v(-0.85, 1.25) * mm});
            skLineSegment(sketch, "E25.0.4.180", {"start": v(-3.95, 1.25) * mm, "end": v(-3.95, 3.25) * mm});
            skLineSegment(sketch, "E25.0.4.181", {"start": v(-7.75, 1.25) * mm, "end": v(-7.75, 3.25) * mm});
            skLineSegment(sketch, "E25.0.4.182", {"start": v(-11.55, 1.25) * mm, "end": v(-11.55, 3.25) * mm});
            skLineSegment(sketch, "E25.0.4.184", {"start": v(3.65, 1.25) * mm, "end": v(3.65, 3.25) * mm});
            skLineSegment(sketch, "E25.0.4.185", {"start": v(-0.15, 1.25) * mm, "end": v(-0.15, 3.25) * mm});
            skLineSegment(sketch, "E25.0.4.186", {"start": v(-4.65, 1.25) * mm, "end": v(-4.65, 3.25) * mm});
            skLineSegment(sketch, "E25.0.4.187", {"start": v(-8.45, 1.25) * mm, "end": v(-8.45, 3.25) * mm});
            skLineSegment(sketch, "E25.0.4.188", {"start": v(-12.25, 1.25) * mm, "end": v(-12.25, 3.25) * mm});
            skLineSegment(sketch, "E25.0.4.189", {"start": v(2.95, 1.25) * mm, "end": v(2.95, 3.25) * mm});
            skLineSegment(sketch, "E25.0.4.190", {"start": v(-0.85, 1.25) * mm, "end": v(-0.85, 3.25) * mm});
            skLineSegment(sketch, "E25.0.4.191", {"start": v(-3.95, 3.25) * mm, "end": v(-4.65, 3.25) * mm});
            skLineSegment(sketch, "E25.0.4.192", {"start": v(-7.75, 3.25) * mm, "end": v(-8.45, 3.25) * mm});
            skLineSegment(sketch, "E25.0.4.193", {"start": v(-11.55, 3.25) * mm, "end": v(-12.25, 3.25) * mm});
            skLineSegment(sketch, "E25.0.4.194", {"start": v(3.65, 3.25) * mm, "end": v(2.95, 3.25) * mm});
            skLineSegment(sketch, "E25.0.4.195", {"start": v(-0.15, 3.25) * mm, "end": v(-0.85, 3.25) * mm});
            skLineSegment(sketch, "E25.0.4.196", {"start": v(0.8, 1.25) * mm, "end": v(0.8, 3.25) * mm});
            skLineSegment(sketch, "E25.0.4.197", {"start": v(-3, 1.25) * mm, "end": v(-3, 3.25) * mm});
            skLineSegment(sketch, "E25.0.4.198", {"start": v(-6.8, 1.25) * mm, "end": v(-6.8, 3.25) * mm});
            skLineSegment(sketch, "E25.0.4.199", {"start": v(-10.6, 1.25) * mm, "end": v(-10.6, 3.25) * mm});
            skLineSegment(sketch, "E25.0.4.200", {"start": v(1.75, 1.25) * mm, "end": v(1.75, 3.25) * mm});
            skLineSegment(sketch, "E25.0.4.201", {"start": v(-2.05, 1.25) * mm, "end": v(-2.05, 3.25) * mm});
            skLineSegment(sketch, "E25.0.4.202", {"start": v(-5.85, 1.25) * mm, "end": v(-5.85, 3.25) * mm});
            skLineSegment(sketch, "E25.0.4.204", {"start": v(5.55, 1.25) * mm, "end": v(5.55, 3.25) * mm});
            skLineSegment(sketch, "E25.0.4.206", {"start": v(-3, 1.25) * mm, "end": v(-3.7, 1.25) * mm});
            skLineSegment(sketch, "E25.0.4.207", {"start": v(-6.8, 1.25) * mm, "end": v(-7.5, 1.25) * mm});
            skLineSegment(sketch, "E25.0.4.208", {"start": v(-10.6, 1.25) * mm, "end": v(-11.3, 1.25) * mm});
            skLineSegment(sketch, "E25.0.4.210", {"start": v(12.2, 1.25) * mm, "end": v(11.5, 1.25) * mm});
            skLineSegment(sketch, "E25.0.4.211", {"start": v(8.4, 1.25) * mm, "end": v(7.7, 1.25) * mm});
            skLineSegment(sketch, "E25.0.4.212", {"start": v(4.6, 1.25) * mm, "end": v(3.9, 1.25) * mm});
            skLineSegment(sketch, "E25.0.4.213", {"start": v(0.8, 1.25) * mm, "end": v(0.1, 1.25) * mm});
            skLineSegment(sketch, "E25.0.4.214", {"start": v(0.1, 1.25) * mm, "end": v(0.1, 3.25) * mm});
            skLineSegment(sketch, "E25.0.4.215", {"start": v(-3.7, 1.25) * mm, "end": v(-3.7, 3.25) * mm});
            skLineSegment(sketch, "E25.0.4.216", {"start": v(-7.5, 1.25) * mm, "end": v(-7.5, 3.25) * mm});
            skLineSegment(sketch, "E25.0.4.217", {"start": v(-11.3, 1.25) * mm, "end": v(-11.3, 3.25) * mm});
            skLineSegment(sketch, "E25.0.4.218", {"start": v(3.9, 1.25) * mm, "end": v(3.9, 3.25) * mm});
            skLineSegment(sketch, "E25.0.4.219", {"start": v(1.05, 1.25) * mm, "end": v(1.05, 3.25) * mm});
            skLineSegment(sketch, "E25.0.4.220", {"start": v(-2.75, 1.25) * mm, "end": v(-2.75, 3.25) * mm});
            skLineSegment(sketch, "E25.0.4.221", {"start": v(-6.55, 1.25) * mm, "end": v(-6.55, 3.25) * mm});
            skLineSegment(sketch, "E25.0.4.222", {"start": v(-10.35, 1.25) * mm, "end": v(-10.35, 3.25) * mm});
            skLineSegment(sketch, "E25.0.4.224", {"start": v(8.65, 1.25) * mm, "end": v(8.65, 3.25) * mm});
            skLineSegment(sketch, "E25.0.4.225", {"start": v(-9.65, 1.25) * mm, "end": v(-9.65, 3.25) * mm});
            skPoint(sketch, "E25.0.5.0", {"position": v(-4.3, 0) * mm});
            skPoint(sketch, "E25.0.5.1", {"position": v(10.9, 0) * mm});
            skPoint(sketch, "E25.0.5.2", {"position": v(11.85, 0) * mm});
            skPoint(sketch, "E25.0.5.3", {"position": v(-3.35, 0) * mm});
            skPoint(sketch, "E25.0.5.4", {"position": v(12.8, 0) * mm});
            skPoint(sketch, "E25.0.5.5", {"position": v(-2.4, 0) * mm});
            skPoint(sketch, "E25.0.5.6", {"position": v(13.75, 0) * mm});
            skPoint(sketch, "E25.0.5.7", {"position": v(-1.45, 0) * mm});
            skPoint(sketch, "E25.0.5.8", {"position": v(14.7, 0) * mm});
            skPoint(sketch, "E25.0.5.9", {"position": v(-0.5, 0) * mm});
            skPoint(sketch, "E25.0.5.11", {"position": v(15.65, 0) * mm});
            skPoint(sketch, "E25.0.5.12", {"position": v(0.45, 0) * mm});
            skPoint(sketch, "E25.0.5.14", {"position": v(16.6, 0) * mm});
            skPoint(sketch, "E25.0.5.15", {"position": v(1.4, 0) * mm});
            skPoint(sketch, "E25.0.5.17", {"position": v(17.55, 0) * mm});
            skPoint(sketch, "E25.0.5.18", {"position": v(2.35, 0) * mm});
            skPoint(sketch, "E25.0.5.19", {"position": v(-11.9, 0) * mm});
            skPoint(sketch, "E25.0.5.20", {"position": v(18.5, 0) * mm});
            skPoint(sketch, "E25.0.5.21", {"position": v(3.3, 0) * mm});
            skPoint(sketch, "E25.0.5.23", {"position": v(-10.95, 0) * mm});
            skPoint(sketch, "E25.0.5.25", {"position": v(4.25, 0) * mm});
            skPoint(sketch, "E25.0.5.26", {"position": v(9.95, 0) * mm});
            skPoint(sketch, "E25.0.5.27", {"position": v(6.15, 0) * mm});
            skPoint(sketch, "E25.0.5.28", {"position": v(-9.05, 0) * mm});
            skPoint(sketch, "E25.0.5.30", {"position": v(-5.25, 0) * mm});
            skPoint(sketch, "E25.0.5.31", {"position": v(-6.2, 0) * mm});
            skPoint(sketch, "E25.0.5.32", {"position": v(9, 0) * mm});
            skPoint(sketch, "E25.0.5.38", {"position": v(8.05, 0) * mm});
            skPoint(sketch, "E25.0.5.39", {"position": v(-7.15, 0) * mm});
            skPoint(sketch, "E25.0.5.40", {"position": v(5.2, 0) * mm});
            skPoint(sketch, "E25.0.5.41", {"position": v(-10, 0) * mm});
            skPoint(sketch, "E25.0.5.44", {"position": v(7.1, 0) * mm});
            skPoint(sketch, "E25.0.5.45", {"position": v(-8.1, 0) * mm});
            skLineSegment(sketch, "E25.0.5.54", {"start": v(18.85, -1) * mm, "end": v(18.15, -1) * mm});
            skLineSegment(sketch, "E25.0.5.55", {"start": v(18.85, -1) * mm, "end": v(18.85, 1) * mm});
            skLineSegment(sketch, "E25.0.5.56", {"start": v(18.15, -1) * mm, "end": v(18.15, 1) * mm});
            skLineSegment(sketch, "E25.0.5.67", {"start": v(17.9, -1) * mm, "end": v(17.2, -1) * mm});
            skLineSegment(sketch, "E25.0.5.69", {"start": v(17.9, -1) * mm, "end": v(17.9, 1) * mm});
            skLineSegment(sketch, "E25.0.5.71", {"start": v(17.2, -1) * mm, "end": v(17.2, 1) * mm});
            skLineSegment(sketch, "E25.0.5.72", {"start": v(16.95, -1) * mm, "end": v(16.25, -1) * mm});
            skLineSegment(sketch, "E25.0.5.74", {"start": v(16.95, -1) * mm, "end": v(16.95, 1) * mm});
            skLineSegment(sketch, "E25.0.5.79", {"start": v(16.25, -1) * mm, "end": v(16.25, 1) * mm});
            skLineSegment(sketch, "E25.0.5.80", {"start": v(16, 1) * mm, "end": v(15.3, 1) * mm});
            skLineSegment(sketch, "E25.0.5.81", {"start": v(12.2, 1) * mm, "end": v(11.5, 1) * mm});
            skLineSegment(sketch, "E25.0.5.83", {"start": v(16.95, 1) * mm, "end": v(16.25, 1) * mm});
            skLineSegment(sketch, "E25.0.5.84", {"start": v(13.15, 1) * mm, "end": v(12.45, 1) * mm});
            skLineSegment(sketch, "E25.0.5.85", {"start": v(9.35, 1) * mm, "end": v(8.65, 1) * mm});
            skLineSegment(sketch, "E25.0.5.86", {"start": v(5.55, 1) * mm, "end": v(4.85, 1) * mm});
            skLineSegment(sketch, "E25.0.5.87", {"start": v(8.4, 1) * mm, "end": v(7.7, 1) * mm});
            skLineSegment(sketch, "E25.0.5.90", {"start": v(13.4, -1) * mm, "end": v(13.4, 1) * mm});
            skLineSegment(sketch, "E25.0.5.91", {"start": v(9.6, -1) * mm, "end": v(9.6, 1) * mm});
            skLineSegment(sketch, "E25.0.5.92", {"start": v(5.8, -1) * mm, "end": v(5.8, 1) * mm});
            skLineSegment(sketch, "E25.0.5.94", {"start": v(10.3, 1) * mm, "end": v(9.6, 1) * mm});
            skLineSegment(sketch, "E25.0.5.95", {"start": v(6.5, 1) * mm, "end": v(5.8, 1) * mm});
            skLineSegment(sketch, "E25.0.5.96", {"start": v(17.9, 1) * mm, "end": v(17.2, 1) * mm});
            skLineSegment(sketch, "E25.0.5.97", {"start": v(14.1, 1) * mm, "end": v(13.4, 1) * mm});
            skLineSegment(sketch, "E25.0.5.99", {"start": v(15.05, -1) * mm, "end": v(14.35, -1) * mm});
            skLineSegment(sketch, "E25.0.5.100", {"start": v(11.25, -1) * mm, "end": v(11.25, 1) * mm});
            skLineSegment(sketch, "E25.0.5.101", {"start": v(7.45, -1) * mm, "end": v(7.45, 1) * mm});
            skLineSegment(sketch, "E25.0.5.102", {"start": v(15.05, -1) * mm, "end": v(15.05, 1) * mm});
            skLineSegment(sketch, "E25.0.5.104", {"start": v(10.55, -1) * mm, "end": v(10.55, 1) * mm});
            skLineSegment(sketch, "E25.0.5.105", {"start": v(6.75, -1) * mm, "end": v(6.75, 1) * mm});
            skLineSegment(sketch, "E25.0.5.106", {"start": v(14.35, -1) * mm, "end": v(14.35, 1) * mm});
            skLineSegment(sketch, "E25.0.5.108", {"start": v(11.25, 1) * mm, "end": v(10.55, 1) * mm});
            skLineSegment(sketch, "E25.0.5.109", {"start": v(7.45, 1) * mm, "end": v(6.75, 1) * mm});
            skLineSegment(sketch, "E25.0.5.110", {"start": v(18.85, 1) * mm, "end": v(18.15, 1) * mm});
            skLineSegment(sketch, "E25.0.5.111", {"start": v(15.05, 1) * mm, "end": v(14.35, 1) * mm});
            skLineSegment(sketch, "E25.0.5.113", {"start": v(16, -1) * mm, "end": v(16, 1) * mm});
            skLineSegment(sketch, "E25.0.5.114", {"start": v(12.2, -1) * mm, "end": v(12.2, 1) * mm});
            skLineSegment(sketch, "E25.0.5.115", {"start": v(8.4, -1) * mm, "end": v(8.4, 1) * mm});
            skLineSegment(sketch, "E25.0.5.116", {"start": v(4.6, -1) * mm, "end": v(4.6, 1) * mm});
            skLineSegment(sketch, "E25.0.5.117", {"start": v(13.15, -1) * mm, "end": v(13.15, 1) * mm});
            skLineSegment(sketch, "E25.0.5.118", {"start": v(9.35, -1) * mm, "end": v(9.35, 1) * mm});
            skLineSegment(sketch, "E25.0.5.119", {"start": v(16, -1) * mm, "end": v(15.3, -1) * mm});
            skLineSegment(sketch, "E25.0.5.121", {"start": v(15.3, -1) * mm, "end": v(15.3, 1) * mm});
            skLineSegment(sketch, "E25.0.5.122", {"start": v(11.5, -1) * mm, "end": v(11.5, 1) * mm});
            skLineSegment(sketch, "E25.0.5.123", {"start": v(7.7, -1) * mm, "end": v(7.7, 1) * mm});
            skLineSegment(sketch, "E25.0.5.127", {"start": v(4.85, -1) * mm, "end": v(4.85, 1) * mm});
            skLineSegment(sketch, "E25.0.5.128", {"start": v(12.45, -1) * mm, "end": v(12.45, 1) * mm});
            skLineSegment(sketch, "E25.0.5.129", {"start": v(-10.6, 1) * mm, "end": v(-11.3, 1) * mm});
            skLineSegment(sketch, "E25.0.5.130", {"start": v(-6.8, 1) * mm, "end": v(-7.5, 1) * mm});
            skLineSegment(sketch, "E25.0.5.131", {"start": v(1.75, 1) * mm, "end": v(1.05, 1) * mm});
            skLineSegment(sketch, "E25.0.5.132", {"start": v(-2.05, 1) * mm, "end": v(-2.75, 1) * mm});
            skLineSegment(sketch, "E25.0.5.133", {"start": v(-5.85, 1) * mm, "end": v(-6.55, 1) * mm});
            skLineSegment(sketch, "E25.0.5.135", {"start": v(-9.65, 1) * mm, "end": v(-10.35, 1) * mm});
            skLineSegment(sketch, "E25.0.5.136", {"start": v(-3, 1) * mm, "end": v(-3.7, 1) * mm});
            skLineSegment(sketch, "E25.0.5.140", {"start": v(-4.9, -1) * mm, "end": v(-5.6, -1) * mm});
            skLineSegment(sketch, "E25.0.5.141", {"start": v(-1.1, -1) * mm, "end": v(-1.8, -1) * mm});
            skLineSegment(sketch, "E25.0.5.142", {"start": v(-8.7, -1) * mm, "end": v(-9.4, -1) * mm});
            skLineSegment(sketch, "E25.0.5.143", {"start": v(14.1, -1) * mm, "end": v(13.4, -1) * mm});
            skLineSegment(sketch, "E25.0.5.144", {"start": v(10.3, -1) * mm, "end": v(9.6, -1) * mm});
            skLineSegment(sketch, "E25.0.5.145", {"start": v(6.5, -1) * mm, "end": v(5.8, -1) * mm});
            skLineSegment(sketch, "E25.0.5.147", {"start": v(4.6, 1) * mm, "end": v(3.9, 1) * mm});
            skLineSegment(sketch, "E25.0.5.148", {"start": v(2.7, -1) * mm, "end": v(2.7, 1) * mm});
            skLineSegment(sketch, "E25.0.5.149", {"start": v(-1.1, -1) * mm, "end": v(-1.1, 1) * mm});
            skLineSegment(sketch, "E25.0.5.150", {"start": v(-4.9, -1) * mm, "end": v(-4.9, 1) * mm});
            skLineSegment(sketch, "E25.0.5.151", {"start": v(-8.7, -1) * mm, "end": v(-8.7, 1) * mm});
            skLineSegment(sketch, "E25.0.5.152", {"start": v(14.1, -1) * mm, "end": v(14.1, 1) * mm});
            skLineSegment(sketch, "E25.0.5.153", {"start": v(10.3, -1) * mm, "end": v(10.3, 1) * mm});
            skLineSegment(sketch, "E25.0.5.154", {"start": v(6.5, -1) * mm, "end": v(6.5, 1) * mm});
            skLineSegment(sketch, "E25.0.5.159", {"start": v(-5.6, -1) * mm, "end": v(-5.6, 1) * mm});
            skLineSegment(sketch, "E25.0.5.160", {"start": v(-9.4, -1) * mm, "end": v(-9.4, 1) * mm});
            skLineSegment(sketch, "E25.0.5.161", {"start": v(1.75, -1) * mm, "end": v(1.05, -1) * mm});
            skLineSegment(sketch, "E25.0.5.162", {"start": v(-2.05, -1) * mm, "end": v(-2.75, -1) * mm});
            skLineSegment(sketch, "E25.0.5.163", {"start": v(-5.85, -1) * mm, "end": v(-6.55, -1) * mm});
            skLineSegment(sketch, "E25.0.5.164", {"start": v(-9.65, -1) * mm, "end": v(-10.35, -1) * mm});
            skLineSegment(sketch, "E25.0.5.165", {"start": v(-4.9, 1) * mm, "end": v(-5.6, 1) * mm});
            skLineSegment(sketch, "E25.0.5.166", {"start": v(-8.7, 1) * mm, "end": v(-9.4, 1) * mm});
            skLineSegment(sketch, "E25.0.5.167", {"start": v(2.7, 1) * mm, "end": v(2, 1) * mm});
            skLineSegment(sketch, "E25.0.5.168", {"start": v(13.15, -1) * mm, "end": v(12.45, -1) * mm});
            skLineSegment(sketch, "E25.0.5.169", {"start": v(9.35, -1) * mm, "end": v(8.65, -1) * mm});
            skLineSegment(sketch, "E25.0.5.171", {"start": v(5.55, -1) * mm, "end": v(4.85, -1) * mm});
            skLineSegment(sketch, "E25.0.5.172", {"start": v(-3.95, -1) * mm, "end": v(-4.65, -1) * mm});
            skLineSegment(sketch, "E25.0.5.173", {"start": v(-7.75, -1) * mm, "end": v(-8.45, -1) * mm});
            skLineSegment(sketch, "E25.0.5.174", {"start": v(-11.55, -1) * mm, "end": v(-12.25, -1) * mm});
            skLineSegment(sketch, "E25.0.5.176", {"start": v(11.25, -1) * mm, "end": v(10.55, -1) * mm});
            skLineSegment(sketch, "E25.0.5.177", {"start": v(7.45, -1) * mm, "end": v(6.75, -1) * mm});
            skLineSegment(sketch, "E25.0.5.178", {"start": v(3.65, -1) * mm, "end": v(2.95, -1) * mm});
            skLineSegment(sketch, "E25.0.5.179", {"start": v(-0.15, -1) * mm, "end": v(-0.85, -1) * mm});
            skLineSegment(sketch, "E25.0.5.180", {"start": v(-3.95, -1) * mm, "end": v(-3.95, 1) * mm});
            skLineSegment(sketch, "E25.0.5.181", {"start": v(-7.75, -1) * mm, "end": v(-7.75, 1) * mm});
            skLineSegment(sketch, "E25.0.5.182", {"start": v(-11.55, -1) * mm, "end": v(-11.55, 1) * mm});
            skLineSegment(sketch, "E25.0.5.184", {"start": v(3.65, -1) * mm, "end": v(3.65, 1) * mm});
            skLineSegment(sketch, "E25.0.5.185", {"start": v(-0.15, -1) * mm, "end": v(-0.15, 1) * mm});
            skLineSegment(sketch, "E25.0.5.186", {"start": v(-4.65, -1) * mm, "end": v(-4.65, 1) * mm});
            skLineSegment(sketch, "E25.0.5.187", {"start": v(-8.45, -1) * mm, "end": v(-8.45, 1) * mm});
            skLineSegment(sketch, "E25.0.5.188", {"start": v(-12.25, -1) * mm, "end": v(-12.25, 1) * mm});
            skLineSegment(sketch, "E25.0.5.189", {"start": v(2.95, -1) * mm, "end": v(2.95, 1) * mm});
            skLineSegment(sketch, "E25.0.5.190", {"start": v(-0.85, -1) * mm, "end": v(-0.85, 1) * mm});
            skLineSegment(sketch, "E25.0.5.191", {"start": v(-3.95, 1) * mm, "end": v(-4.65, 1) * mm});
            skLineSegment(sketch, "E25.0.5.192", {"start": v(-7.75, 1) * mm, "end": v(-8.45, 1) * mm});
            skLineSegment(sketch, "E25.0.5.193", {"start": v(-11.55, 1) * mm, "end": v(-12.25, 1) * mm});
            skLineSegment(sketch, "E25.0.5.194", {"start": v(3.65, 1) * mm, "end": v(2.95, 1) * mm});
            skLineSegment(sketch, "E25.0.5.195", {"start": v(-0.15, 1) * mm, "end": v(-0.85, 1) * mm});
            skLineSegment(sketch, "E25.0.5.196", {"start": v(0.8, -1) * mm, "end": v(0.8, 1) * mm});
            skLineSegment(sketch, "E25.0.5.197", {"start": v(-3, -1) * mm, "end": v(-3, 1) * mm});
            skLineSegment(sketch, "E25.0.5.198", {"start": v(-6.8, -1) * mm, "end": v(-6.8, 1) * mm});
            skLineSegment(sketch, "E25.0.5.199", {"start": v(-10.6, -1) * mm, "end": v(-10.6, 1) * mm});
            skLineSegment(sketch, "E25.0.5.200", {"start": v(1.75, -1) * mm, "end": v(1.75, 1) * mm});
            skLineSegment(sketch, "E25.0.5.201", {"start": v(-2.05, -1) * mm, "end": v(-2.05, 1) * mm});
            skLineSegment(sketch, "E25.0.5.202", {"start": v(-5.85, -1) * mm, "end": v(-5.85, 1) * mm});
            skLineSegment(sketch, "E25.0.5.204", {"start": v(5.55, -1) * mm, "end": v(5.55, 1) * mm});
            skLineSegment(sketch, "E25.0.5.206", {"start": v(-3, -1) * mm, "end": v(-3.7, -1) * mm});
            skLineSegment(sketch, "E25.0.5.207", {"start": v(-6.8, -1) * mm, "end": v(-7.5, -1) * mm});
            skLineSegment(sketch, "E25.0.5.208", {"start": v(-10.6, -1) * mm, "end": v(-11.3, -1) * mm});
            skLineSegment(sketch, "E25.0.5.210", {"start": v(12.2, -1) * mm, "end": v(11.5, -1) * mm});
            skLineSegment(sketch, "E25.0.5.211", {"start": v(8.4, -1) * mm, "end": v(7.7, -1) * mm});
            skLineSegment(sketch, "E25.0.5.212", {"start": v(4.6, -1) * mm, "end": v(3.9, -1) * mm});
            skLineSegment(sketch, "E25.0.5.213", {"start": v(0.8, -1) * mm, "end": v(0.1, -1) * mm});
            skLineSegment(sketch, "E25.0.5.215", {"start": v(-3.7, -1) * mm, "end": v(-3.7, 1) * mm});
            skLineSegment(sketch, "E25.0.5.216", {"start": v(-7.5, -1) * mm, "end": v(-7.5, 1) * mm});
            skLineSegment(sketch, "E25.0.5.217", {"start": v(-11.3, -1) * mm, "end": v(-11.3, 1) * mm});
            skLineSegment(sketch, "E25.0.5.218", {"start": v(3.9, -1) * mm, "end": v(3.9, 1) * mm});
            skLineSegment(sketch, "E25.0.5.219", {"start": v(1.05, -1) * mm, "end": v(1.05, 1) * mm});
            skLineSegment(sketch, "E25.0.5.220", {"start": v(-2.75, -1) * mm, "end": v(-2.75, 1) * mm});
            skLineSegment(sketch, "E25.0.5.221", {"start": v(-6.55, -1) * mm, "end": v(-6.55, 1) * mm});
            skLineSegment(sketch, "E25.0.5.222", {"start": v(-10.35, -1) * mm, "end": v(-10.35, 1) * mm});
            skLineSegment(sketch, "E25.0.5.224", {"start": v(8.65, -1) * mm, "end": v(8.65, 1) * mm});
            skLineSegment(sketch, "E25.0.5.225", {"start": v(-9.65, -1) * mm, "end": v(-9.65, 1) * mm});
            skPoint(sketch, "E25.0.6.0", {"position": v(-4.3, -2.25) * mm});
            skPoint(sketch, "E25.0.6.1", {"position": v(10.9, -2.25) * mm});
            skPoint(sketch, "E25.0.6.2", {"position": v(11.85, -2.25) * mm});
            skPoint(sketch, "E25.0.6.3", {"position": v(-3.35, -2.25) * mm});
            skPoint(sketch, "E25.0.6.4", {"position": v(12.8, -2.25) * mm});
            skPoint(sketch, "E25.0.6.5", {"position": v(-2.4, -2.25) * mm});
            skPoint(sketch, "E25.0.6.6", {"position": v(13.75, -2.25) * mm});
            skPoint(sketch, "E25.0.6.7", {"position": v(-1.45, -2.25) * mm});
            skPoint(sketch, "E25.0.6.8", {"position": v(14.7, -2.25) * mm});
            skPoint(sketch, "E25.0.6.9", {"position": v(-0.5, -2.25) * mm});
            skPoint(sketch, "E25.0.6.11", {"position": v(15.65, -2.25) * mm});
            skPoint(sketch, "E25.0.6.12", {"position": v(0.45, -2.25) * mm});
            skPoint(sketch, "E25.0.6.14", {"position": v(16.6, -2.25) * mm});
            skPoint(sketch, "E25.0.6.15", {"position": v(1.4, -2.25) * mm});
            skPoint(sketch, "E25.0.6.17", {"position": v(17.55, -2.25) * mm});
            skPoint(sketch, "E25.0.6.18", {"position": v(2.35, -2.25) * mm});
            skPoint(sketch, "E25.0.6.19", {"position": v(-11.9, -2.25) * mm});
            skPoint(sketch, "E25.0.6.20", {"position": v(18.5, -2.25) * mm});
            skPoint(sketch, "E25.0.6.21", {"position": v(3.3, -2.25) * mm});
            skPoint(sketch, "E25.0.6.23", {"position": v(-10.95, -2.25) * mm});
            skPoint(sketch, "E25.0.6.25", {"position": v(4.25, -2.25) * mm});
            skPoint(sketch, "E25.0.6.26", {"position": v(9.95, -2.25) * mm});
            skPoint(sketch, "E25.0.6.27", {"position": v(6.15, -2.25) * mm});
            skPoint(sketch, "E25.0.6.28", {"position": v(-9.05, -2.25) * mm});
            skPoint(sketch, "E25.0.6.30", {"position": v(-5.25, -2.25) * mm});
            skPoint(sketch, "E25.0.6.31", {"position": v(-6.2, -2.25) * mm});
            skPoint(sketch, "E25.0.6.32", {"position": v(9, -2.25) * mm});
            skPoint(sketch, "E25.0.6.38", {"position": v(8.05, -2.25) * mm});
            skPoint(sketch, "E25.0.6.39", {"position": v(-7.15, -2.25) * mm});
            skPoint(sketch, "E25.0.6.40", {"position": v(5.2, -2.25) * mm});
            skPoint(sketch, "E25.0.6.41", {"position": v(-10, -2.25) * mm});
            skPoint(sketch, "E25.0.6.44", {"position": v(7.1, -2.25) * mm});
            skPoint(sketch, "E25.0.6.45", {"position": v(-8.1, -2.25) * mm});
            skLineSegment(sketch, "E25.0.6.54", {"start": v(18.85, -3.25) * mm, "end": v(18.15, -3.25) * mm});
            skLineSegment(sketch, "E25.0.6.55", {"start": v(18.85, -3.25) * mm, "end": v(18.85, -1.25) * mm});
            skLineSegment(sketch, "E25.0.6.56", {"start": v(18.15, -3.25) * mm, "end": v(18.15, -1.25) * mm});
            skLineSegment(sketch, "E25.0.6.67", {"start": v(17.9, -3.25) * mm, "end": v(17.2, -3.25) * mm});
            skLineSegment(sketch, "E25.0.6.69", {"start": v(17.9, -3.25) * mm, "end": v(17.9, -1.25) * mm});
            skLineSegment(sketch, "E25.0.6.71", {"start": v(17.2, -3.25) * mm, "end": v(17.2, -1.25) * mm});
            skLineSegment(sketch, "E25.0.6.72", {"start": v(16.95, -3.25) * mm, "end": v(16.25, -3.25) * mm});
            skLineSegment(sketch, "E25.0.6.74", {"start": v(16.95, -3.25) * mm, "end": v(16.95, -1.25) * mm});
            skLineSegment(sketch, "E25.0.6.79", {"start": v(16.25, -3.25) * mm, "end": v(16.25, -1.25) * mm});
            skLineSegment(sketch, "E25.0.6.80", {"start": v(16, -1.25) * mm, "end": v(15.3, -1.25) * mm});
            skLineSegment(sketch, "E25.0.6.81", {"start": v(12.2, -1.25) * mm, "end": v(11.5, -1.25) * mm});
            skLineSegment(sketch, "E25.0.6.83", {"start": v(16.95, -1.25) * mm, "end": v(16.25, -1.25) * mm});
            skLineSegment(sketch, "E25.0.6.84", {"start": v(13.15, -1.25) * mm, "end": v(12.45, -1.25) * mm});
            skLineSegment(sketch, "E25.0.6.85", {"start": v(9.35, -1.25) * mm, "end": v(8.65, -1.25) * mm});
            skLineSegment(sketch, "E25.0.6.86", {"start": v(5.55, -1.25) * mm, "end": v(4.85, -1.25) * mm});
            skLineSegment(sketch, "E25.0.6.87", {"start": v(8.4, -1.25) * mm, "end": v(7.7, -1.25) * mm});
            skLineSegment(sketch, "E25.0.6.90", {"start": v(13.4, -3.25) * mm, "end": v(13.4, -1.25) * mm});
            skLineSegment(sketch, "E25.0.6.91", {"start": v(9.6, -3.25) * mm, "end": v(9.6, -1.25) * mm});
            skLineSegment(sketch, "E25.0.6.92", {"start": v(5.8, -3.25) * mm, "end": v(5.8, -1.25) * mm});
            skLineSegment(sketch, "E25.0.6.94", {"start": v(10.3, -1.25) * mm, "end": v(9.6, -1.25) * mm});
            skLineSegment(sketch, "E25.0.6.95", {"start": v(6.5, -1.25) * mm, "end": v(5.8, -1.25) * mm});
            skLineSegment(sketch, "E25.0.6.96", {"start": v(17.9, -1.25) * mm, "end": v(17.2, -1.25) * mm});
            skLineSegment(sketch, "E25.0.6.97", {"start": v(14.1, -1.25) * mm, "end": v(13.4, -1.25) * mm});
            skLineSegment(sketch, "E25.0.6.99", {"start": v(15.05, -3.25) * mm, "end": v(14.35, -3.25) * mm});
            skLineSegment(sketch, "E25.0.6.100", {"start": v(11.25, -3.25) * mm, "end": v(11.25, -1.25) * mm});
            skLineSegment(sketch, "E25.0.6.101", {"start": v(7.45, -3.25) * mm, "end": v(7.45, -1.25) * mm});
            skLineSegment(sketch, "E25.0.6.102", {"start": v(15.05, -3.25) * mm, "end": v(15.05, -1.25) * mm});
            skLineSegment(sketch, "E25.0.6.104", {"start": v(10.55, -3.25) * mm, "end": v(10.55, -1.25) * mm});
            skLineSegment(sketch, "E25.0.6.105", {"start": v(6.75, -3.25) * mm, "end": v(6.75, -1.25) * mm});
            skLineSegment(sketch, "E25.0.6.106", {"start": v(14.35, -3.25) * mm, "end": v(14.35, -1.25) * mm});
            skLineSegment(sketch, "E25.0.6.108", {"start": v(11.25, -1.25) * mm, "end": v(10.55, -1.25) * mm});
            skLineSegment(sketch, "E25.0.6.109", {"start": v(7.45, -1.25) * mm, "end": v(6.75, -1.25) * mm});
            skLineSegment(sketch, "E25.0.6.110", {"start": v(18.85, -1.25) * mm, "end": v(18.15, -1.25) * mm});
            skLineSegment(sketch, "E25.0.6.111", {"start": v(15.05, -1.25) * mm, "end": v(14.35, -1.25) * mm});
            skLineSegment(sketch, "E25.0.6.113", {"start": v(16, -3.25) * mm, "end": v(16, -1.25) * mm});
            skLineSegment(sketch, "E25.0.6.114", {"start": v(12.2, -3.25) * mm, "end": v(12.2, -1.25) * mm});
            skLineSegment(sketch, "E25.0.6.115", {"start": v(8.4, -3.25) * mm, "end": v(8.4, -1.25) * mm});
            skLineSegment(sketch, "E25.0.6.116", {"start": v(4.6, -3.25) * mm, "end": v(4.6, -1.25) * mm});
            skLineSegment(sketch, "E25.0.6.117", {"start": v(13.15, -3.25) * mm, "end": v(13.15, -1.25) * mm});
            skLineSegment(sketch, "E25.0.6.118", {"start": v(9.35, -3.25) * mm, "end": v(9.35, -1.25) * mm});
            skLineSegment(sketch, "E25.0.6.119", {"start": v(16, -3.25) * mm, "end": v(15.3, -3.25) * mm});
            skLineSegment(sketch, "E25.0.6.121", {"start": v(15.3, -3.25) * mm, "end": v(15.3, -1.25) * mm});
            skLineSegment(sketch, "E25.0.6.122", {"start": v(11.5, -3.25) * mm, "end": v(11.5, -1.25) * mm});
            skLineSegment(sketch, "E25.0.6.123", {"start": v(7.7, -3.25) * mm, "end": v(7.7, -1.25) * mm});
            skLineSegment(sketch, "E25.0.6.127", {"start": v(4.85, -3.25) * mm, "end": v(4.85, -1.25) * mm});
            skLineSegment(sketch, "E25.0.6.128", {"start": v(12.45, -3.25) * mm, "end": v(12.45, -1.25) * mm});
            skLineSegment(sketch, "E25.0.6.129", {"start": v(-10.6, -1.25) * mm, "end": v(-11.3, -1.25) * mm});
            skLineSegment(sketch, "E25.0.6.130", {"start": v(-6.8, -1.25) * mm, "end": v(-7.5, -1.25) * mm});
            skLineSegment(sketch, "E25.0.6.131", {"start": v(1.75, -1.25) * mm, "end": v(1.05, -1.25) * mm});
            skLineSegment(sketch, "E25.0.6.132", {"start": v(-2.05, -1.25) * mm, "end": v(-2.75, -1.25) * mm});
            skLineSegment(sketch, "E25.0.6.133", {"start": v(-5.85, -1.25) * mm, "end": v(-6.55, -1.25) * mm});
            skLineSegment(sketch, "E25.0.6.134", {"start": v(0.8, -1.25) * mm, "end": v(0.1, -1.25) * mm});
            skLineSegment(sketch, "E25.0.6.135", {"start": v(-9.65, -1.25) * mm, "end": v(-10.35, -1.25) * mm});
            skLineSegment(sketch, "E25.0.6.136", {"start": v(-3, -1.25) * mm, "end": v(-3.7, -1.25) * mm});
            skLineSegment(sketch, "E25.0.6.139", {"start": v(2.7, -3.25) * mm, "end": v(2, -3.25) * mm});
            skLineSegment(sketch, "E25.0.6.140", {"start": v(-4.9, -3.25) * mm, "end": v(-5.6, -3.25) * mm});
            skLineSegment(sketch, "E25.0.6.141", {"start": v(-1.1, -3.25) * mm, "end": v(-1.8, -3.25) * mm});
            skLineSegment(sketch, "E25.0.6.142", {"start": v(-8.7, -3.25) * mm, "end": v(-9.4, -3.25) * mm});
            skLineSegment(sketch, "E25.0.6.143", {"start": v(14.1, -3.25) * mm, "end": v(13.4, -3.25) * mm});
            skLineSegment(sketch, "E25.0.6.144", {"start": v(10.3, -3.25) * mm, "end": v(9.6, -3.25) * mm});
            skLineSegment(sketch, "E25.0.6.145", {"start": v(6.5, -3.25) * mm, "end": v(5.8, -3.25) * mm});
            skLineSegment(sketch, "E25.0.6.147", {"start": v(4.6, -1.25) * mm, "end": v(3.9, -1.25) * mm});
            skLineSegment(sketch, "E25.0.6.148", {"start": v(2.7, -3.25) * mm, "end": v(2.7, -1.25) * mm});
            skLineSegment(sketch, "E25.0.6.149", {"start": v(-1.1, -3.25) * mm, "end": v(-1.1, -1.25) * mm});
            skLineSegment(sketch, "E25.0.6.150", {"start": v(-4.9, -3.25) * mm, "end": v(-4.9, -1.25) * mm});
            skLineSegment(sketch, "E25.0.6.151", {"start": v(-8.7, -3.25) * mm, "end": v(-8.7, -1.25) * mm});
            skLineSegment(sketch, "E25.0.6.152", {"start": v(14.1, -3.25) * mm, "end": v(14.1, -1.25) * mm});
            skLineSegment(sketch, "E25.0.6.153", {"start": v(10.3, -3.25) * mm, "end": v(10.3, -1.25) * mm});
            skLineSegment(sketch, "E25.0.6.154", {"start": v(6.5, -3.25) * mm, "end": v(6.5, -1.25) * mm});
            skLineSegment(sketch, "E25.0.6.157", {"start": v(2, -3.25) * mm, "end": v(2, -1.25) * mm});
            skLineSegment(sketch, "E25.0.6.158", {"start": v(-1.8, -3.25) * mm, "end": v(-1.8, -1.25) * mm});
            skLineSegment(sketch, "E25.0.6.159", {"start": v(-5.6, -3.25) * mm, "end": v(-5.6, -1.25) * mm});
            skLineSegment(sketch, "E25.0.6.160", {"start": v(-9.4, -3.25) * mm, "end": v(-9.4, -1.25) * mm});
            skLineSegment(sketch, "E25.0.6.161", {"start": v(1.75, -3.25) * mm, "end": v(1.05, -3.25) * mm});
            skLineSegment(sketch, "E25.0.6.162", {"start": v(-2.05, -3.25) * mm, "end": v(-2.75, -3.25) * mm});
            skLineSegment(sketch, "E25.0.6.163", {"start": v(-5.85, -3.25) * mm, "end": v(-6.55, -3.25) * mm});
            skLineSegment(sketch, "E25.0.6.164", {"start": v(-9.65, -3.25) * mm, "end": v(-10.35, -3.25) * mm});
            skLineSegment(sketch, "E25.0.6.165", {"start": v(-4.9, -1.25) * mm, "end": v(-5.6, -1.25) * mm});
            skLineSegment(sketch, "E25.0.6.166", {"start": v(-8.7, -1.25) * mm, "end": v(-9.4, -1.25) * mm});
            skLineSegment(sketch, "E25.0.6.167", {"start": v(2.7, -1.25) * mm, "end": v(2, -1.25) * mm});
            skLineSegment(sketch, "E25.0.6.168", {"start": v(13.15, -3.25) * mm, "end": v(12.45, -3.25) * mm});
            skLineSegment(sketch, "E25.0.6.169", {"start": v(9.35, -3.25) * mm, "end": v(8.65, -3.25) * mm});
            skLineSegment(sketch, "E25.0.6.170", {"start": v(-1.1, -1.25) * mm, "end": v(-1.8, -1.25) * mm});
            skLineSegment(sketch, "E25.0.6.171", {"start": v(5.55, -3.25) * mm, "end": v(4.85, -3.25) * mm});
            skLineSegment(sketch, "E25.0.6.172", {"start": v(-3.95, -3.25) * mm, "end": v(-4.65, -3.25) * mm});
            skLineSegment(sketch, "E25.0.6.173", {"start": v(-7.75, -3.25) * mm, "end": v(-8.45, -3.25) * mm});
            skLineSegment(sketch, "E25.0.6.174", {"start": v(-11.55, -3.25) * mm, "end": v(-12.25, -3.25) * mm});
            skLineSegment(sketch, "E25.0.6.176", {"start": v(11.25, -3.25) * mm, "end": v(10.55, -3.25) * mm});
            skLineSegment(sketch, "E25.0.6.177", {"start": v(7.45, -3.25) * mm, "end": v(6.75, -3.25) * mm});
            skLineSegment(sketch, "E25.0.6.178", {"start": v(3.65, -3.25) * mm, "end": v(2.95, -3.25) * mm});
            skLineSegment(sketch, "E25.0.6.179", {"start": v(-0.15, -3.25) * mm, "end": v(-0.85, -3.25) * mm});
            skLineSegment(sketch, "E25.0.6.180", {"start": v(-3.95, -3.25) * mm, "end": v(-3.95, -1.25) * mm});
            skLineSegment(sketch, "E25.0.6.181", {"start": v(-7.75, -3.25) * mm, "end": v(-7.75, -1.25) * mm});
            skLineSegment(sketch, "E25.0.6.182", {"start": v(-11.55, -3.25) * mm, "end": v(-11.55, -1.25) * mm});
            skLineSegment(sketch, "E25.0.6.184", {"start": v(3.65, -3.25) * mm, "end": v(3.65, -1.25) * mm});
            skLineSegment(sketch, "E25.0.6.185", {"start": v(-0.15, -3.25) * mm, "end": v(-0.15, -1.25) * mm});
            skLineSegment(sketch, "E25.0.6.186", {"start": v(-4.65, -3.25) * mm, "end": v(-4.65, -1.25) * mm});
            skLineSegment(sketch, "E25.0.6.187", {"start": v(-8.45, -3.25) * mm, "end": v(-8.45, -1.25) * mm});
            skLineSegment(sketch, "E25.0.6.188", {"start": v(-12.25, -3.25) * mm, "end": v(-12.25, -1.25) * mm});
            skLineSegment(sketch, "E25.0.6.189", {"start": v(2.95, -3.25) * mm, "end": v(2.95, -1.25) * mm});
            skLineSegment(sketch, "E25.0.6.190", {"start": v(-0.85, -3.25) * mm, "end": v(-0.85, -1.25) * mm});
            skLineSegment(sketch, "E25.0.6.191", {"start": v(-3.95, -1.25) * mm, "end": v(-4.65, -1.25) * mm});
            skLineSegment(sketch, "E25.0.6.192", {"start": v(-7.75, -1.25) * mm, "end": v(-8.45, -1.25) * mm});
            skLineSegment(sketch, "E25.0.6.193", {"start": v(-11.55, -1.25) * mm, "end": v(-12.25, -1.25) * mm});
            skLineSegment(sketch, "E25.0.6.194", {"start": v(3.65, -1.25) * mm, "end": v(3.15, -1.25) * mm});
            skLineSegment(sketch, "E25.0.6.196", {"start": v(0.8, -3.25) * mm, "end": v(0.8, -1.25) * mm});
            skLineSegment(sketch, "E25.0.6.197", {"start": v(-3, -3.25) * mm, "end": v(-3, -1.25) * mm});
            skLineSegment(sketch, "E25.0.6.198", {"start": v(-6.8, -3.25) * mm, "end": v(-6.8, -1.25) * mm});
            skLineSegment(sketch, "E25.0.6.199", {"start": v(-10.6, -3.25) * mm, "end": v(-10.6, -1.25) * mm});
            skLineSegment(sketch, "E25.0.6.200", {"start": v(1.75, -3.25) * mm, "end": v(1.75, -1.25) * mm});
            skLineSegment(sketch, "E25.0.6.201", {"start": v(-2.05, -3.25) * mm, "end": v(-2.05, -1.25) * mm});
            skLineSegment(sketch, "E25.0.6.202", {"start": v(-5.85, -3.25) * mm, "end": v(-5.85, -1.25) * mm});
            skLineSegment(sketch, "E25.0.6.204", {"start": v(5.55, -3.25) * mm, "end": v(5.55, -1.25) * mm});
            skLineSegment(sketch, "E25.0.6.206", {"start": v(-3, -3.25) * mm, "end": v(-3.7, -3.25) * mm});
            skLineSegment(sketch, "E25.0.6.207", {"start": v(-6.8, -3.25) * mm, "end": v(-7.5, -3.25) * mm});
            skLineSegment(sketch, "E25.0.6.208", {"start": v(-10.6, -3.25) * mm, "end": v(-11.3, -3.25) * mm});
            skLineSegment(sketch, "E25.0.6.210", {"start": v(12.2, -3.25) * mm, "end": v(11.5, -3.25) * mm});
            skLineSegment(sketch, "E25.0.6.211", {"start": v(8.4, -3.25) * mm, "end": v(7.7, -3.25) * mm});
            skLineSegment(sketch, "E25.0.6.212", {"start": v(4.6, -3.25) * mm, "end": v(3.9, -3.25) * mm});
            skLineSegment(sketch, "E25.0.6.213", {"start": v(0.8, -3.25) * mm, "end": v(0.1, -3.25) * mm});
            skLineSegment(sketch, "E25.0.6.214", {"start": v(0.1, -3.25) * mm, "end": v(0.1, -1.25) * mm});
            skLineSegment(sketch, "E25.0.6.215", {"start": v(-3.7, -3.25) * mm, "end": v(-3.7, -1.25) * mm});
            skLineSegment(sketch, "E25.0.6.216", {"start": v(-7.5, -3.25) * mm, "end": v(-7.5, -1.25) * mm});
            skLineSegment(sketch, "E25.0.6.217", {"start": v(-11.3, -3.25) * mm, "end": v(-11.3, -1.25) * mm});
            skLineSegment(sketch, "E25.0.6.218", {"start": v(3.9, -3.25) * mm, "end": v(3.9, -1.25) * mm});
            skLineSegment(sketch, "E25.0.6.219", {"start": v(1.05, -3.25) * mm, "end": v(1.05, -1.25) * mm});
            skLineSegment(sketch, "E25.0.6.220", {"start": v(-2.75, -3.25) * mm, "end": v(-2.75, -1.25) * mm});
            skLineSegment(sketch, "E25.0.6.221", {"start": v(-6.55, -3.25) * mm, "end": v(-6.55, -1.25) * mm});
            skLineSegment(sketch, "E25.0.6.222", {"start": v(-10.35, -3.25) * mm, "end": v(-10.35, -1.25) * mm});
            skLineSegment(sketch, "E25.0.6.224", {"start": v(8.65, -3.25) * mm, "end": v(8.65, -1.25) * mm});
            skLineSegment(sketch, "E25.0.6.225", {"start": v(-9.65, -3.25) * mm, "end": v(-9.65, -1.25) * mm});
            skPoint(sketch, "E25.0.7.0", {"position": v(-4.3, -4.5) * mm});
            skPoint(sketch, "E25.0.7.1", {"position": v(10.9, -4.5) * mm});
            skPoint(sketch, "E25.0.7.2", {"position": v(11.85, -4.5) * mm});
            skPoint(sketch, "E25.0.7.3", {"position": v(-3.35, -4.5) * mm});
            skPoint(sketch, "E25.0.7.4", {"position": v(12.8, -4.5) * mm});
            skPoint(sketch, "E25.0.7.5", {"position": v(-2.4, -4.5) * mm});
            skPoint(sketch, "E25.0.7.6", {"position": v(13.75, -4.5) * mm});
            skPoint(sketch, "E25.0.7.7", {"position": v(-1.45, -4.5) * mm});
            skPoint(sketch, "E25.0.7.8", {"position": v(14.7, -4.5) * mm});
            skPoint(sketch, "E25.0.7.9", {"position": v(-0.5, -4.5) * mm});
            skPoint(sketch, "E25.0.7.11", {"position": v(15.65, -4.5) * mm});
            skPoint(sketch, "E25.0.7.12", {"position": v(0.45, -4.5) * mm});
            skPoint(sketch, "E25.0.7.14", {"position": v(16.6, -4.5) * mm});
            skPoint(sketch, "E25.0.7.15", {"position": v(1.4, -4.5) * mm});
            skPoint(sketch, "E25.0.7.17", {"position": v(17.55, -4.5) * mm});
            skPoint(sketch, "E25.0.7.18", {"position": v(2.35, -4.5) * mm});
            skPoint(sketch, "E25.0.7.19", {"position": v(-11.9, -4.5) * mm});
            skPoint(sketch, "E25.0.7.20", {"position": v(18.5, -4.5) * mm});
            skPoint(sketch, "E25.0.7.21", {"position": v(3.3, -4.5) * mm});
            skPoint(sketch, "E25.0.7.23", {"position": v(-10.95, -4.5) * mm});
            skPoint(sketch, "E25.0.7.25", {"position": v(4.25, -4.5) * mm});
            skPoint(sketch, "E25.0.7.26", {"position": v(9.95, -4.5) * mm});
            skPoint(sketch, "E25.0.7.27", {"position": v(6.15, -4.5) * mm});
            skPoint(sketch, "E25.0.7.28", {"position": v(-9.05, -4.5) * mm});
            skPoint(sketch, "E25.0.7.30", {"position": v(-5.25, -4.5) * mm});
            skPoint(sketch, "E25.0.7.31", {"position": v(-6.2, -4.5) * mm});
            skPoint(sketch, "E25.0.7.32", {"position": v(9, -4.5) * mm});
            skPoint(sketch, "E25.0.7.38", {"position": v(8.05, -4.5) * mm});
            skPoint(sketch, "E25.0.7.39", {"position": v(-7.15, -4.5) * mm});
            skPoint(sketch, "E25.0.7.40", {"position": v(5.2, -4.5) * mm});
            skPoint(sketch, "E25.0.7.41", {"position": v(-10, -4.5) * mm});
            skPoint(sketch, "E25.0.7.44", {"position": v(7.1, -4.5) * mm});
            skPoint(sketch, "E25.0.7.45", {"position": v(-8.1, -4.5) * mm});
            skLineSegment(sketch, "E25.0.7.54", {"start": v(18.85, -5.5) * mm, "end": v(18.15, -5.5) * mm});
            skLineSegment(sketch, "E25.0.7.55", {"start": v(18.85, -5.5) * mm, "end": v(18.85, -3.5) * mm});
            skLineSegment(sketch, "E25.0.7.56", {"start": v(18.15, -5.5) * mm, "end": v(18.15, -3.5) * mm});
            skLineSegment(sketch, "E25.0.7.67", {"start": v(17.9, -5.5) * mm, "end": v(17.2, -5.5) * mm});
            skLineSegment(sketch, "E25.0.7.69", {"start": v(17.9, -5.5) * mm, "end": v(17.9, -3.5) * mm});
            skLineSegment(sketch, "E25.0.7.71", {"start": v(17.2, -5.5) * mm, "end": v(17.2, -3.5) * mm});
            skLineSegment(sketch, "E25.0.7.72", {"start": v(16.95, -5.5) * mm, "end": v(16.25, -5.5) * mm});
            skLineSegment(sketch, "E25.0.7.74", {"start": v(16.95, -5.5) * mm, "end": v(16.95, -3.5) * mm});
            skLineSegment(sketch, "E25.0.7.79", {"start": v(16.25, -5.5) * mm, "end": v(16.25, -3.5) * mm});
            skLineSegment(sketch, "E25.0.7.80", {"start": v(16, -3.5) * mm, "end": v(15.3, -3.5) * mm});
            skLineSegment(sketch, "E25.0.7.81", {"start": v(12.2, -3.5) * mm, "end": v(11.5, -3.5) * mm});
            skLineSegment(sketch, "E25.0.7.83", {"start": v(16.95, -3.5) * mm, "end": v(16.25, -3.5) * mm});
            skLineSegment(sketch, "E25.0.7.84", {"start": v(13.15, -3.5) * mm, "end": v(12.45, -3.5) * mm});
            skLineSegment(sketch, "E25.0.7.85", {"start": v(9.35, -3.5) * mm, "end": v(8.65, -3.5) * mm});
            skLineSegment(sketch, "E25.0.7.86", {"start": v(5.55, -3.5) * mm, "end": v(4.85, -3.5) * mm});
            skLineSegment(sketch, "E25.0.7.87", {"start": v(8.4, -3.5) * mm, "end": v(7.7, -3.5) * mm});
            skLineSegment(sketch, "E25.0.7.90", {"start": v(13.4, -5.5) * mm, "end": v(13.4, -3.5) * mm});
            skLineSegment(sketch, "E25.0.7.91", {"start": v(9.6, -5.5) * mm, "end": v(9.6, -3.5) * mm});
            skLineSegment(sketch, "E25.0.7.92", {"start": v(5.8, -5.5) * mm, "end": v(5.8, -3.5) * mm});
            skLineSegment(sketch, "E25.0.7.94", {"start": v(10.3, -3.5) * mm, "end": v(9.6, -3.5) * mm});
            skLineSegment(sketch, "E25.0.7.95", {"start": v(6.5, -3.5) * mm, "end": v(5.8, -3.5) * mm});
            skLineSegment(sketch, "E25.0.7.96", {"start": v(17.9, -3.5) * mm, "end": v(17.2, -3.5) * mm});
            skLineSegment(sketch, "E25.0.7.97", {"start": v(14.1, -3.5) * mm, "end": v(13.4, -3.5) * mm});
            skLineSegment(sketch, "E25.0.7.99", {"start": v(15.05, -5.5) * mm, "end": v(14.35, -5.5) * mm});
            skLineSegment(sketch, "E25.0.7.100", {"start": v(11.25, -5.5) * mm, "end": v(11.25, -3.5) * mm});
            skLineSegment(sketch, "E25.0.7.101", {"start": v(7.45, -5.5) * mm, "end": v(7.45, -3.5) * mm});
            skLineSegment(sketch, "E25.0.7.102", {"start": v(15.05, -5.5) * mm, "end": v(15.05, -3.5) * mm});
            skLineSegment(sketch, "E25.0.7.104", {"start": v(10.55, -5.5) * mm, "end": v(10.55, -3.5) * mm});
            skLineSegment(sketch, "E25.0.7.105", {"start": v(6.75, -5.5) * mm, "end": v(6.75, -3.5) * mm});
            skLineSegment(sketch, "E25.0.7.106", {"start": v(14.35, -5.5) * mm, "end": v(14.35, -3.5) * mm});
            skLineSegment(sketch, "E25.0.7.108", {"start": v(11.25, -3.5) * mm, "end": v(10.55, -3.5) * mm});
            skLineSegment(sketch, "E25.0.7.109", {"start": v(7.45, -3.5) * mm, "end": v(6.75, -3.5) * mm});
            skLineSegment(sketch, "E25.0.7.110", {"start": v(18.85, -3.5) * mm, "end": v(18.15, -3.5) * mm});
            skLineSegment(sketch, "E25.0.7.111", {"start": v(15.05, -3.5) * mm, "end": v(14.35, -3.5) * mm});
            skLineSegment(sketch, "E25.0.7.113", {"start": v(16, -5.5) * mm, "end": v(16, -3.5) * mm});
            skLineSegment(sketch, "E25.0.7.114", {"start": v(12.2, -5.5) * mm, "end": v(12.2, -3.5) * mm});
            skLineSegment(sketch, "E25.0.7.115", {"start": v(8.4, -5.5) * mm, "end": v(8.4, -3.5) * mm});
            skLineSegment(sketch, "E25.0.7.116", {"start": v(4.6, -5.5) * mm, "end": v(4.6, -3.5) * mm});
            skLineSegment(sketch, "E25.0.7.117", {"start": v(13.15, -5.5) * mm, "end": v(13.15, -3.5) * mm});
            skLineSegment(sketch, "E25.0.7.118", {"start": v(9.35, -5.5) * mm, "end": v(9.35, -3.5) * mm});
            skLineSegment(sketch, "E25.0.7.119", {"start": v(16, -5.5) * mm, "end": v(15.3, -5.5) * mm});
            skLineSegment(sketch, "E25.0.7.121", {"start": v(15.3, -5.5) * mm, "end": v(15.3, -3.5) * mm});
            skLineSegment(sketch, "E25.0.7.122", {"start": v(11.5, -5.5) * mm, "end": v(11.5, -3.5) * mm});
            skLineSegment(sketch, "E25.0.7.123", {"start": v(7.7, -5.5) * mm, "end": v(7.7, -3.5) * mm});
            skLineSegment(sketch, "E25.0.7.127", {"start": v(4.85, -5.5) * mm, "end": v(4.85, -3.5) * mm});
            skLineSegment(sketch, "E25.0.7.128", {"start": v(12.45, -5.5) * mm, "end": v(12.45, -3.5) * mm});
            skLineSegment(sketch, "E25.0.7.129", {"start": v(-10.6, -3.5) * mm, "end": v(-11.3, -3.5) * mm});
            skLineSegment(sketch, "E25.0.7.130", {"start": v(-6.8, -3.5) * mm, "end": v(-7.5, -3.5) * mm});
            skLineSegment(sketch, "E25.0.7.131", {"start": v(1.75, -3.5) * mm, "end": v(1.05, -3.5) * mm});
            skLineSegment(sketch, "E25.0.7.132", {"start": v(-2.05, -3.5) * mm, "end": v(-2.75, -3.5) * mm});
            skLineSegment(sketch, "E25.0.7.133", {"start": v(-5.85, -3.5) * mm, "end": v(-6.55, -3.5) * mm});
            skLineSegment(sketch, "E25.0.7.134", {"start": v(0.8, -3.5) * mm, "end": v(0.1, -3.5) * mm});
            skLineSegment(sketch, "E25.0.7.135", {"start": v(-9.65, -3.5) * mm, "end": v(-10.35, -3.5) * mm});
            skLineSegment(sketch, "E25.0.7.136", {"start": v(-3, -3.5) * mm, "end": v(-3.7, -3.5) * mm});
            skLineSegment(sketch, "E25.0.7.139", {"start": v(2.7, -5.5) * mm, "end": v(2, -5.5) * mm});
            skLineSegment(sketch, "E25.0.7.140", {"start": v(-4.9, -5.5) * mm, "end": v(-5.6, -5.5) * mm});
            skLineSegment(sketch, "E25.0.7.141", {"start": v(-1.1, -5.5) * mm, "end": v(-1.8, -5.5) * mm});
            skLineSegment(sketch, "E25.0.7.142", {"start": v(-8.7, -5.5) * mm, "end": v(-9.4, -5.5) * mm});
            skLineSegment(sketch, "E25.0.7.143", {"start": v(14.1, -5.5) * mm, "end": v(13.4, -5.5) * mm});
            skLineSegment(sketch, "E25.0.7.144", {"start": v(10.3, -5.5) * mm, "end": v(9.6, -5.5) * mm});
            skLineSegment(sketch, "E25.0.7.145", {"start": v(6.5, -5.5) * mm, "end": v(5.8, -5.5) * mm});
            skLineSegment(sketch, "E25.0.7.147", {"start": v(4.6, -3.5) * mm, "end": v(3.9, -3.5) * mm});
            skLineSegment(sketch, "E25.0.7.148", {"start": v(2.7, -5.5) * mm, "end": v(2.7, -3.5) * mm});
            skLineSegment(sketch, "E25.0.7.149", {"start": v(-1.1, -5.5) * mm, "end": v(-1.1, -3.5) * mm});
            skLineSegment(sketch, "E25.0.7.150", {"start": v(-4.9, -5.5) * mm, "end": v(-4.9, -3.5) * mm});
            skLineSegment(sketch, "E25.0.7.151", {"start": v(-8.7, -5.5) * mm, "end": v(-8.7, -3.5) * mm});
            skLineSegment(sketch, "E25.0.7.152", {"start": v(14.1, -5.5) * mm, "end": v(14.1, -3.5) * mm});
            skLineSegment(sketch, "E25.0.7.153", {"start": v(10.3, -5.5) * mm, "end": v(10.3, -3.5) * mm});
            skLineSegment(sketch, "E25.0.7.154", {"start": v(6.5, -5.5) * mm, "end": v(6.5, -3.5) * mm});
            skLineSegment(sketch, "E25.0.7.157", {"start": v(2, -5.5) * mm, "end": v(2, -3.5) * mm});
            skLineSegment(sketch, "E25.0.7.158", {"start": v(-1.8, -5.5) * mm, "end": v(-1.8, -3.5) * mm});
            skLineSegment(sketch, "E25.0.7.159", {"start": v(-5.6, -5.5) * mm, "end": v(-5.6, -3.5) * mm});
            skLineSegment(sketch, "E25.0.7.160", {"start": v(-9.4, -5.5) * mm, "end": v(-9.4, -3.5) * mm});
            skLineSegment(sketch, "E25.0.7.161", {"start": v(1.75, -5.5) * mm, "end": v(1.05, -5.5) * mm});
            skLineSegment(sketch, "E25.0.7.162", {"start": v(-2.05, -5.5) * mm, "end": v(-2.75, -5.5) * mm});
            skLineSegment(sketch, "E25.0.7.163", {"start": v(-5.85, -5.5) * mm, "end": v(-6.55, -5.5) * mm});
            skLineSegment(sketch, "E25.0.7.164", {"start": v(-9.65, -5.5) * mm, "end": v(-10.35, -5.5) * mm});
            skLineSegment(sketch, "E25.0.7.165", {"start": v(-4.9, -3.5) * mm, "end": v(-5.6, -3.5) * mm});
            skLineSegment(sketch, "E25.0.7.166", {"start": v(-8.7, -3.5) * mm, "end": v(-9.4, -3.5) * mm});
            skLineSegment(sketch, "E25.0.7.167", {"start": v(2.7, -3.5) * mm, "end": v(2, -3.5) * mm});
            skLineSegment(sketch, "E25.0.7.168", {"start": v(13.15, -5.5) * mm, "end": v(12.45, -5.5) * mm});
            skLineSegment(sketch, "E25.0.7.169", {"start": v(9.35, -5.5) * mm, "end": v(8.65, -5.5) * mm});
            skLineSegment(sketch, "E25.0.7.170", {"start": v(-1.1, -3.5) * mm, "end": v(-1.8, -3.5) * mm});
            skLineSegment(sketch, "E25.0.7.171", {"start": v(5.55, -5.5) * mm, "end": v(4.85, -5.5) * mm});
            skLineSegment(sketch, "E25.0.7.172", {"start": v(-3.95, -5.5) * mm, "end": v(-4.65, -5.5) * mm});
            skLineSegment(sketch, "E25.0.7.173", {"start": v(-7.75, -5.5) * mm, "end": v(-8.45, -5.5) * mm});
            skLineSegment(sketch, "E25.0.7.174", {"start": v(-11.55, -5.5) * mm, "end": v(-12.25, -5.5) * mm});
            skLineSegment(sketch, "E25.0.7.176", {"start": v(11.25, -5.5) * mm, "end": v(10.55, -5.5) * mm});
            skLineSegment(sketch, "E25.0.7.177", {"start": v(7.45, -5.5) * mm, "end": v(6.75, -5.5) * mm});
            skLineSegment(sketch, "E25.0.7.178", {"start": v(3.65, -5.5) * mm, "end": v(2.95, -5.5) * mm});
            skLineSegment(sketch, "E25.0.7.179", {"start": v(-0.15, -5.5) * mm, "end": v(-0.85, -5.5) * mm});
            skLineSegment(sketch, "E25.0.7.180", {"start": v(-3.95, -5.5) * mm, "end": v(-3.95, -3.5) * mm});
            skLineSegment(sketch, "E25.0.7.181", {"start": v(-7.75, -5.5) * mm, "end": v(-7.75, -3.5) * mm});
            skLineSegment(sketch, "E25.0.7.182", {"start": v(-11.55, -5.5) * mm, "end": v(-11.55, -3.5) * mm});
            skLineSegment(sketch, "E25.0.7.184", {"start": v(3.65, -5.5) * mm, "end": v(3.65, -3.5) * mm});
            skLineSegment(sketch, "E25.0.7.185", {"start": v(-0.15, -5.5) * mm, "end": v(-0.15, -3.5) * mm});
            skLineSegment(sketch, "E25.0.7.186", {"start": v(-4.65, -5.5) * mm, "end": v(-4.65, -3.5) * mm});
            skLineSegment(sketch, "E25.0.7.187", {"start": v(-8.45, -5.5) * mm, "end": v(-8.45, -3.5) * mm});
            skLineSegment(sketch, "E25.0.7.188", {"start": v(-12.25, -5.5) * mm, "end": v(-12.25, -3.5) * mm});
            skLineSegment(sketch, "E25.0.7.189", {"start": v(2.95, -5.5) * mm, "end": v(2.95, -3.5) * mm});
            skLineSegment(sketch, "E25.0.7.190", {"start": v(-0.85, -5.5) * mm, "end": v(-0.85, -3.5) * mm});
            skLineSegment(sketch, "E25.0.7.191", {"start": v(-3.95, -3.5) * mm, "end": v(-4.65, -3.5) * mm});
            skLineSegment(sketch, "E25.0.7.192", {"start": v(-7.75, -3.5) * mm, "end": v(-8.45, -3.5) * mm});
            skLineSegment(sketch, "E25.0.7.193", {"start": v(-11.55, -3.5) * mm, "end": v(-12.25, -3.5) * mm});
            skLineSegment(sketch, "E25.0.7.194", {"start": v(3.65, -3.5) * mm, "end": v(2.95, -3.5) * mm});
            skLineSegment(sketch, "E25.0.7.195", {"start": v(-0.15, -3.5) * mm, "end": v(-0.85, -3.5) * mm});
            skLineSegment(sketch, "E25.0.7.196", {"start": v(0.8, -5.5) * mm, "end": v(0.8, -3.5) * mm});
            skLineSegment(sketch, "E25.0.7.197", {"start": v(-3, -5.5) * mm, "end": v(-3, -3.5) * mm});
            skLineSegment(sketch, "E25.0.7.198", {"start": v(-6.8, -5.5) * mm, "end": v(-6.8, -3.5) * mm});
            skLineSegment(sketch, "E25.0.7.199", {"start": v(-10.6, -5.5) * mm, "end": v(-10.6, -3.5) * mm});
            skLineSegment(sketch, "E25.0.7.200", {"start": v(1.75, -5.5) * mm, "end": v(1.75, -3.5) * mm});
            skLineSegment(sketch, "E25.0.7.201", {"start": v(-2.05, -5.5) * mm, "end": v(-2.05, -3.5) * mm});
            skLineSegment(sketch, "E25.0.7.202", {"start": v(-5.85, -5.5) * mm, "end": v(-5.85, -3.5) * mm});
            skLineSegment(sketch, "E25.0.7.204", {"start": v(5.55, -5.5) * mm, "end": v(5.55, -3.5) * mm});
            skLineSegment(sketch, "E25.0.7.206", {"start": v(-3, -5.5) * mm, "end": v(-3.7, -5.5) * mm});
            skLineSegment(sketch, "E25.0.7.207", {"start": v(-6.8, -5.5) * mm, "end": v(-7.5, -5.5) * mm});
            skLineSegment(sketch, "E25.0.7.208", {"start": v(-10.6, -5.5) * mm, "end": v(-11.3, -5.5) * mm});
            skLineSegment(sketch, "E25.0.7.210", {"start": v(12.2, -5.5) * mm, "end": v(11.5, -5.5) * mm});
            skLineSegment(sketch, "E25.0.7.211", {"start": v(8.4, -5.5) * mm, "end": v(7.7, -5.5) * mm});
            skLineSegment(sketch, "E25.0.7.212", {"start": v(4.6, -5.5) * mm, "end": v(3.9, -5.5) * mm});
            skLineSegment(sketch, "E25.0.7.213", {"start": v(0.8, -5.5) * mm, "end": v(0.1, -5.5) * mm});
            skLineSegment(sketch, "E25.0.7.214", {"start": v(0.1, -5.5) * mm, "end": v(0.1, -3.5) * mm});
            skLineSegment(sketch, "E25.0.7.215", {"start": v(-3.7, -5.5) * mm, "end": v(-3.7, -3.5) * mm});
            skLineSegment(sketch, "E25.0.7.216", {"start": v(-7.5, -5.5) * mm, "end": v(-7.5, -3.5) * mm});
            skLineSegment(sketch, "E25.0.7.217", {"start": v(-11.3, -5.5) * mm, "end": v(-11.3, -3.5) * mm});
            skLineSegment(sketch, "E25.0.7.218", {"start": v(3.9, -5.5) * mm, "end": v(3.9, -3.5) * mm});
            skLineSegment(sketch, "E25.0.7.219", {"start": v(1.05, -5.5) * mm, "end": v(1.05, -3.5) * mm});
            skLineSegment(sketch, "E25.0.7.220", {"start": v(-2.75, -5.5) * mm, "end": v(-2.75, -3.5) * mm});
            skLineSegment(sketch, "E25.0.7.221", {"start": v(-6.55, -5.5) * mm, "end": v(-6.55, -3.5) * mm});
            skLineSegment(sketch, "E25.0.7.222", {"start": v(-10.35, -5.5) * mm, "end": v(-10.35, -3.5) * mm});
            skLineSegment(sketch, "E25.0.7.224", {"start": v(8.65, -5.5) * mm, "end": v(8.65, -3.5) * mm});
            skLineSegment(sketch, "E25.0.7.225", {"start": v(-9.65, -5.5) * mm, "end": v(-9.65, -3.5) * mm});
            skPoint(sketch, "E25.0.8.0", {"position": v(-4.3, -6.75) * mm});
            skPoint(sketch, "E25.0.8.1", {"position": v(10.9, -6.75) * mm});
            skPoint(sketch, "E25.0.8.2", {"position": v(11.85, -6.75) * mm});
            skPoint(sketch, "E25.0.8.3", {"position": v(-3.35, -6.75) * mm});
            skPoint(sketch, "E25.0.8.4", {"position": v(12.8, -6.75) * mm});
            skPoint(sketch, "E25.0.8.5", {"position": v(-2.4, -6.75) * mm});
            skPoint(sketch, "E25.0.8.6", {"position": v(13.75, -6.75) * mm});
            skPoint(sketch, "E25.0.8.7", {"position": v(-1.45, -6.75) * mm});
            skPoint(sketch, "E25.0.8.8", {"position": v(14.7, -6.75) * mm});
            skPoint(sketch, "E25.0.8.9", {"position": v(-0.5, -6.75) * mm});
            skPoint(sketch, "E25.0.8.11", {"position": v(15.65, -6.75) * mm});
            skPoint(sketch, "E25.0.8.12", {"position": v(0.45, -6.75) * mm});
            skPoint(sketch, "E25.0.8.14", {"position": v(16.6, -6.75) * mm});
            skPoint(sketch, "E25.0.8.15", {"position": v(1.4, -6.75) * mm});
            skPoint(sketch, "E25.0.8.17", {"position": v(17.55, -6.75) * mm});
            skPoint(sketch, "E25.0.8.18", {"position": v(2.35, -6.75) * mm});
            skPoint(sketch, "E25.0.8.19", {"position": v(-11.9, -6.75) * mm});
            skPoint(sketch, "E25.0.8.20", {"position": v(18.5, -6.75) * mm});
            skPoint(sketch, "E25.0.8.21", {"position": v(3.3, -6.75) * mm});
            skPoint(sketch, "E25.0.8.23", {"position": v(-10.95, -6.75) * mm});
            skPoint(sketch, "E25.0.8.25", {"position": v(4.25, -6.75) * mm});
            skPoint(sketch, "E25.0.8.26", {"position": v(9.95, -6.75) * mm});
            skPoint(sketch, "E25.0.8.27", {"position": v(6.15, -6.75) * mm});
            skPoint(sketch, "E25.0.8.28", {"position": v(-9.05, -6.75) * mm});
            skPoint(sketch, "E25.0.8.30", {"position": v(-5.25, -6.75) * mm});
            skPoint(sketch, "E25.0.8.31", {"position": v(-6.2, -6.75) * mm});
            skPoint(sketch, "E25.0.8.32", {"position": v(9, -6.75) * mm});
            skPoint(sketch, "E25.0.8.38", {"position": v(8.05, -6.75) * mm});
            skPoint(sketch, "E25.0.8.39", {"position": v(-7.15, -6.75) * mm});
            skPoint(sketch, "E25.0.8.40", {"position": v(5.2, -6.75) * mm});
            skPoint(sketch, "E25.0.8.41", {"position": v(-10, -6.75) * mm});
            skPoint(sketch, "E25.0.8.44", {"position": v(7.1, -6.75) * mm});
            skPoint(sketch, "E25.0.8.45", {"position": v(-8.1, -6.75) * mm});
            skLineSegment(sketch, "E25.0.8.54", {"start": v(18.85, -7.75) * mm, "end": v(18.15, -7.75) * mm});
            skLineSegment(sketch, "E25.0.8.55", {"start": v(18.85, -7.75) * mm, "end": v(18.85, -5.75) * mm});
            skLineSegment(sketch, "E25.0.8.56", {"start": v(18.15, -7.75) * mm, "end": v(18.15, -5.75) * mm});
            skLineSegment(sketch, "E25.0.8.67", {"start": v(17.9, -7.75) * mm, "end": v(17.2, -7.75) * mm});
            skLineSegment(sketch, "E25.0.8.69", {"start": v(17.9, -7.75) * mm, "end": v(17.9, -5.75) * mm});
            skLineSegment(sketch, "E25.0.8.71", {"start": v(17.2, -7.75) * mm, "end": v(17.2, -5.75) * mm});
            skLineSegment(sketch, "E25.0.8.72", {"start": v(16.95, -7.75) * mm, "end": v(16.25, -7.75) * mm});
            skLineSegment(sketch, "E25.0.8.74", {"start": v(16.95, -7.75) * mm, "end": v(16.95, -5.75) * mm});
            skLineSegment(sketch, "E25.0.8.79", {"start": v(16.25, -7.75) * mm, "end": v(16.25, -5.75) * mm});
            skLineSegment(sketch, "E25.0.8.80", {"start": v(16, -5.75) * mm, "end": v(15.3, -5.75) * mm});
            skLineSegment(sketch, "E25.0.8.81", {"start": v(12.2, -5.75) * mm, "end": v(11.5, -5.75) * mm});
            skLineSegment(sketch, "E25.0.8.83", {"start": v(16.95, -5.75) * mm, "end": v(16.25, -5.75) * mm});
            skLineSegment(sketch, "E25.0.8.84", {"start": v(13.15, -5.75) * mm, "end": v(12.45, -5.75) * mm});
            skLineSegment(sketch, "E25.0.8.85", {"start": v(9.35, -5.75) * mm, "end": v(8.65, -5.75) * mm});
            skLineSegment(sketch, "E25.0.8.86", {"start": v(5.55, -5.75) * mm, "end": v(4.85, -5.75) * mm});
            skLineSegment(sketch, "E25.0.8.87", {"start": v(8.4, -5.75) * mm, "end": v(7.7, -5.75) * mm});
            skLineSegment(sketch, "E25.0.8.90", {"start": v(13.4, -7.75) * mm, "end": v(13.4, -5.75) * mm});
            skLineSegment(sketch, "E25.0.8.91", {"start": v(9.6, -7.75) * mm, "end": v(9.6, -5.75) * mm});
            skLineSegment(sketch, "E25.0.8.92", {"start": v(5.8, -7.75) * mm, "end": v(5.8, -5.75) * mm});
            skLineSegment(sketch, "E25.0.8.94", {"start": v(10.3, -5.75) * mm, "end": v(9.6, -5.75) * mm});
            skLineSegment(sketch, "E25.0.8.95", {"start": v(6.5, -5.75) * mm, "end": v(5.8, -5.75) * mm});
            skLineSegment(sketch, "E25.0.8.96", {"start": v(17.9, -5.75) * mm, "end": v(17.2, -5.75) * mm});
            skLineSegment(sketch, "E25.0.8.97", {"start": v(14.1, -5.75) * mm, "end": v(13.4, -5.75) * mm});
            skLineSegment(sketch, "E25.0.8.99", {"start": v(15.05, -7.75) * mm, "end": v(14.35, -7.75) * mm});
            skLineSegment(sketch, "E25.0.8.100", {"start": v(11.25, -7.75) * mm, "end": v(11.25, -5.75) * mm});
            skLineSegment(sketch, "E25.0.8.101", {"start": v(7.45, -7.75) * mm, "end": v(7.45, -5.75) * mm});
            skLineSegment(sketch, "E25.0.8.102", {"start": v(15.05, -7.75) * mm, "end": v(15.05, -5.75) * mm});
            skLineSegment(sketch, "E25.0.8.104", {"start": v(10.55, -7.75) * mm, "end": v(10.55, -5.75) * mm});
            skLineSegment(sketch, "E25.0.8.105", {"start": v(6.75, -7.75) * mm, "end": v(6.75, -5.75) * mm});
            skLineSegment(sketch, "E25.0.8.106", {"start": v(14.35, -7.75) * mm, "end": v(14.35, -5.75) * mm});
            skLineSegment(sketch, "E25.0.8.108", {"start": v(11.25, -5.75) * mm, "end": v(10.55, -5.75) * mm});
            skLineSegment(sketch, "E25.0.8.109", {"start": v(7.45, -5.75) * mm, "end": v(6.75, -5.75) * mm});
            skLineSegment(sketch, "E25.0.8.110", {"start": v(18.85, -5.75) * mm, "end": v(18.15, -5.75) * mm});
            skLineSegment(sketch, "E25.0.8.111", {"start": v(15.05, -5.75) * mm, "end": v(14.35, -5.75) * mm});
            skLineSegment(sketch, "E25.0.8.113", {"start": v(16, -7.75) * mm, "end": v(16, -5.75) * mm});
            skLineSegment(sketch, "E25.0.8.114", {"start": v(12.2, -7.75) * mm, "end": v(12.2, -5.75) * mm});
            skLineSegment(sketch, "E25.0.8.115", {"start": v(8.4, -7.75) * mm, "end": v(8.4, -5.75) * mm});
            skLineSegment(sketch, "E25.0.8.116", {"start": v(4.6, -7.75) * mm, "end": v(4.6, -5.75) * mm});
            skLineSegment(sketch, "E25.0.8.117", {"start": v(13.15, -7.75) * mm, "end": v(13.15, -5.75) * mm});
            skLineSegment(sketch, "E25.0.8.118", {"start": v(9.35, -7.75) * mm, "end": v(9.35, -5.75) * mm});
            skLineSegment(sketch, "E25.0.8.119", {"start": v(16, -7.75) * mm, "end": v(15.3, -7.75) * mm});
            skLineSegment(sketch, "E25.0.8.121", {"start": v(15.3, -7.75) * mm, "end": v(15.3, -5.75) * mm});
            skLineSegment(sketch, "E25.0.8.122", {"start": v(11.5, -7.75) * mm, "end": v(11.5, -5.75) * mm});
            skLineSegment(sketch, "E25.0.8.123", {"start": v(7.7, -7.75) * mm, "end": v(7.7, -5.75) * mm});
            skLineSegment(sketch, "E25.0.8.127", {"start": v(4.85, -7.75) * mm, "end": v(4.85, -5.75) * mm});
            skLineSegment(sketch, "E25.0.8.128", {"start": v(12.45, -7.75) * mm, "end": v(12.45, -5.75) * mm});
            skLineSegment(sketch, "E25.0.8.129", {"start": v(-10.6, -5.75) * mm, "end": v(-11.3, -5.75) * mm});
            skLineSegment(sketch, "E25.0.8.130", {"start": v(-6.8, -5.75) * mm, "end": v(-7.5, -5.75) * mm});
            skLineSegment(sketch, "E25.0.8.131", {"start": v(1.75, -5.75) * mm, "end": v(1.05, -5.75) * mm});
            skLineSegment(sketch, "E25.0.8.132", {"start": v(-2.05, -5.75) * mm, "end": v(-2.75, -5.75) * mm});
            skLineSegment(sketch, "E25.0.8.133", {"start": v(-5.85, -5.75) * mm, "end": v(-6.55, -5.75) * mm});
            skLineSegment(sketch, "E25.0.8.134", {"start": v(0.8, -5.75) * mm, "end": v(0.1, -5.75) * mm});
            skLineSegment(sketch, "E25.0.8.135", {"start": v(-9.65, -5.75) * mm, "end": v(-10.35, -5.75) * mm});
            skLineSegment(sketch, "E25.0.8.136", {"start": v(-3, -5.75) * mm, "end": v(-3.7, -5.75) * mm});
            skLineSegment(sketch, "E25.0.8.139", {"start": v(2.7, -7.75) * mm, "end": v(2, -7.75) * mm});
            skLineSegment(sketch, "E25.0.8.140", {"start": v(-4.9, -7.75) * mm, "end": v(-5.6, -7.75) * mm});
            skLineSegment(sketch, "E25.0.8.141", {"start": v(-1.1, -7.75) * mm, "end": v(-1.8, -7.75) * mm});
            skLineSegment(sketch, "E25.0.8.142", {"start": v(-8.7, -7.75) * mm, "end": v(-9.4, -7.75) * mm});
            skLineSegment(sketch, "E25.0.8.143", {"start": v(14.1, -7.75) * mm, "end": v(13.4, -7.75) * mm});
            skLineSegment(sketch, "E25.0.8.144", {"start": v(10.3, -7.75) * mm, "end": v(9.6, -7.75) * mm});
            skLineSegment(sketch, "E25.0.8.145", {"start": v(6.5, -7.75) * mm, "end": v(5.8, -7.75) * mm});
            skLineSegment(sketch, "E25.0.8.147", {"start": v(4.6, -5.75) * mm, "end": v(3.9, -5.75) * mm});
            skLineSegment(sketch, "E25.0.8.148", {"start": v(2.7, -7.75) * mm, "end": v(2.7, -5.75) * mm});
            skLineSegment(sketch, "E25.0.8.149", {"start": v(-1.1, -7.75) * mm, "end": v(-1.1, -5.75) * mm});
            skLineSegment(sketch, "E25.0.8.150", {"start": v(-4.9, -7.75) * mm, "end": v(-4.9, -5.75) * mm});
            skLineSegment(sketch, "E25.0.8.151", {"start": v(-8.7, -7.75) * mm, "end": v(-8.7, -5.75) * mm});
            skLineSegment(sketch, "E25.0.8.152", {"start": v(14.1, -7.75) * mm, "end": v(14.1, -5.75) * mm});
            skLineSegment(sketch, "E25.0.8.153", {"start": v(10.3, -7.75) * mm, "end": v(10.3, -5.75) * mm});
            skLineSegment(sketch, "E25.0.8.154", {"start": v(6.5, -7.75) * mm, "end": v(6.5, -5.75) * mm});
            skLineSegment(sketch, "E25.0.8.157", {"start": v(2, -7.75) * mm, "end": v(2, -5.75) * mm});
            skLineSegment(sketch, "E25.0.8.158", {"start": v(-1.8, -7.75) * mm, "end": v(-1.8, -5.75) * mm});
            skLineSegment(sketch, "E25.0.8.159", {"start": v(-5.6, -7.75) * mm, "end": v(-5.6, -5.75) * mm});
            skLineSegment(sketch, "E25.0.8.160", {"start": v(-9.4, -7.75) * mm, "end": v(-9.4, -5.75) * mm});
            skLineSegment(sketch, "E25.0.8.161", {"start": v(1.75, -7.75) * mm, "end": v(1.05, -7.75) * mm});
            skLineSegment(sketch, "E25.0.8.162", {"start": v(-2.05, -7.75) * mm, "end": v(-2.75, -7.75) * mm});
            skLineSegment(sketch, "E25.0.8.163", {"start": v(-5.85, -7.75) * mm, "end": v(-6.55, -7.75) * mm});
            skLineSegment(sketch, "E25.0.8.164", {"start": v(-9.65, -7.75) * mm, "end": v(-10.35, -7.75) * mm});
            skLineSegment(sketch, "E25.0.8.165", {"start": v(-4.9, -5.75) * mm, "end": v(-5.6, -5.75) * mm});
            skLineSegment(sketch, "E25.0.8.166", {"start": v(-8.7, -5.75) * mm, "end": v(-9.4, -5.75) * mm});
            skLineSegment(sketch, "E25.0.8.167", {"start": v(2.7, -5.75) * mm, "end": v(2, -5.75) * mm});
            skLineSegment(sketch, "E25.0.8.168", {"start": v(13.15, -7.75) * mm, "end": v(12.45, -7.75) * mm});
            skLineSegment(sketch, "E25.0.8.169", {"start": v(9.35, -7.75) * mm, "end": v(8.65, -7.75) * mm});
            skLineSegment(sketch, "E25.0.8.170", {"start": v(-1.1, -5.75) * mm, "end": v(-1.8, -5.75) * mm});
            skLineSegment(sketch, "E25.0.8.171", {"start": v(5.55, -7.75) * mm, "end": v(4.85, -7.75) * mm});
            skLineSegment(sketch, "E25.0.8.172", {"start": v(-3.95, -7.75) * mm, "end": v(-4.65, -7.75) * mm});
            skLineSegment(sketch, "E25.0.8.173", {"start": v(-7.75, -7.75) * mm, "end": v(-8.45, -7.75) * mm});
            skLineSegment(sketch, "E25.0.8.174", {"start": v(-11.55, -7.75) * mm, "end": v(-12.25, -7.75) * mm});
            skLineSegment(sketch, "E25.0.8.176", {"start": v(11.25, -7.75) * mm, "end": v(10.55, -7.75) * mm});
            skLineSegment(sketch, "E25.0.8.177", {"start": v(7.45, -7.75) * mm, "end": v(6.75, -7.75) * mm});
            skLineSegment(sketch, "E25.0.8.178", {"start": v(3.65, -7.75) * mm, "end": v(2.95, -7.75) * mm});
            skLineSegment(sketch, "E25.0.8.179", {"start": v(-0.15, -7.75) * mm, "end": v(-0.85, -7.75) * mm});
            skLineSegment(sketch, "E25.0.8.180", {"start": v(-3.95, -7.75) * mm, "end": v(-3.95, -5.75) * mm});
            skLineSegment(sketch, "E25.0.8.181", {"start": v(-7.75, -7.75) * mm, "end": v(-7.75, -5.75) * mm});
            skLineSegment(sketch, "E25.0.8.182", {"start": v(-11.55, -7.75) * mm, "end": v(-11.55, -5.75) * mm});
            skLineSegment(sketch, "E25.0.8.184", {"start": v(3.65, -7.75) * mm, "end": v(3.65, -5.75) * mm});
            skLineSegment(sketch, "E25.0.8.185", {"start": v(-0.15, -7.75) * mm, "end": v(-0.15, -5.75) * mm});
            skLineSegment(sketch, "E25.0.8.186", {"start": v(-4.65, -7.75) * mm, "end": v(-4.65, -5.75) * mm});
            skLineSegment(sketch, "E25.0.8.187", {"start": v(-8.45, -7.75) * mm, "end": v(-8.45, -5.75) * mm});
            skLineSegment(sketch, "E25.0.8.188", {"start": v(-12.25, -7.75) * mm, "end": v(-12.25, -5.75) * mm});
            skLineSegment(sketch, "E25.0.8.189", {"start": v(2.95, -7.75) * mm, "end": v(2.95, -5.75) * mm});
            skLineSegment(sketch, "E25.0.8.190", {"start": v(-0.85, -7.75) * mm, "end": v(-0.85, -5.75) * mm});
            skLineSegment(sketch, "E25.0.8.191", {"start": v(-3.95, -5.75) * mm, "end": v(-4.65, -5.75) * mm});
            skLineSegment(sketch, "E25.0.8.192", {"start": v(-7.75, -5.75) * mm, "end": v(-8.45, -5.75) * mm});
            skLineSegment(sketch, "E25.0.8.193", {"start": v(-11.55, -5.75) * mm, "end": v(-12.25, -5.75) * mm});
            skLineSegment(sketch, "E25.0.8.194", {"start": v(3.65, -5.75) * mm, "end": v(2.95, -5.75) * mm});
            skLineSegment(sketch, "E25.0.8.195", {"start": v(-0.15, -5.75) * mm, "end": v(-0.85, -5.75) * mm});
            skLineSegment(sketch, "E25.0.8.196", {"start": v(0.8, -7.75) * mm, "end": v(0.8, -5.75) * mm});
            skLineSegment(sketch, "E25.0.8.197", {"start": v(-3, -7.75) * mm, "end": v(-3, -5.75) * mm});
            skLineSegment(sketch, "E25.0.8.198", {"start": v(-6.8, -7.75) * mm, "end": v(-6.8, -5.75) * mm});
            skLineSegment(sketch, "E25.0.8.199", {"start": v(-10.6, -7.75) * mm, "end": v(-10.6, -5.75) * mm});
            skLineSegment(sketch, "E25.0.8.200", {"start": v(1.75, -7.75) * mm, "end": v(1.75, -5.75) * mm});
            skLineSegment(sketch, "E25.0.8.201", {"start": v(-2.05, -7.75) * mm, "end": v(-2.05, -5.75) * mm});
            skLineSegment(sketch, "E25.0.8.202", {"start": v(-5.85, -7.75) * mm, "end": v(-5.85, -5.75) * mm});
            skLineSegment(sketch, "E25.0.8.204", {"start": v(5.55, -7.75) * mm, "end": v(5.55, -5.75) * mm});
            skLineSegment(sketch, "E25.0.8.206", {"start": v(-3, -7.75) * mm, "end": v(-3.7, -7.75) * mm});
            skLineSegment(sketch, "E25.0.8.207", {"start": v(-6.8, -7.75) * mm, "end": v(-7.5, -7.75) * mm});
            skLineSegment(sketch, "E25.0.8.208", {"start": v(-10.6, -7.75) * mm, "end": v(-11.3, -7.75) * mm});
            skLineSegment(sketch, "E25.0.8.210", {"start": v(12.2, -7.75) * mm, "end": v(11.5, -7.75) * mm});
            skLineSegment(sketch, "E25.0.8.211", {"start": v(8.4, -7.75) * mm, "end": v(7.7, -7.75) * mm});
            skLineSegment(sketch, "E25.0.8.212", {"start": v(4.6, -7.75) * mm, "end": v(3.9, -7.75) * mm});
            skLineSegment(sketch, "E25.0.8.213", {"start": v(0.8, -7.75) * mm, "end": v(0.1, -7.75) * mm});
            skLineSegment(sketch, "E25.0.8.214", {"start": v(0.1, -7.75) * mm, "end": v(0.1, -5.75) * mm});
            skLineSegment(sketch, "E25.0.8.215", {"start": v(-3.7, -7.75) * mm, "end": v(-3.7, -5.75) * mm});
            skLineSegment(sketch, "E25.0.8.216", {"start": v(-7.5, -7.75) * mm, "end": v(-7.5, -5.75) * mm});
            skLineSegment(sketch, "E25.0.8.217", {"start": v(-11.3, -7.75) * mm, "end": v(-11.3, -5.75) * mm});
            skLineSegment(sketch, "E25.0.8.218", {"start": v(3.9, -7.75) * mm, "end": v(3.9, -5.75) * mm});
            skLineSegment(sketch, "E25.0.8.219", {"start": v(1.05, -7.75) * mm, "end": v(1.05, -5.75) * mm});
            skLineSegment(sketch, "E25.0.8.220", {"start": v(-2.75, -7.75) * mm, "end": v(-2.75, -5.75) * mm});
            skLineSegment(sketch, "E25.0.8.221", {"start": v(-6.55, -7.75) * mm, "end": v(-6.55, -5.75) * mm});
            skLineSegment(sketch, "E25.0.8.222", {"start": v(-10.35, -7.75) * mm, "end": v(-10.35, -5.75) * mm});
            skLineSegment(sketch, "E25.0.8.224", {"start": v(8.65, -7.75) * mm, "end": v(8.65, -5.75) * mm});
            skLineSegment(sketch, "E25.0.8.225", {"start": v(-9.65, -7.75) * mm, "end": v(-9.65, -5.75) * mm});
            skPoint(sketch, "E25.0.9.0", {"position": v(-4.3, -9) * mm});
            skPoint(sketch, "E25.0.9.1", {"position": v(10.9, -9) * mm});
            skPoint(sketch, "E25.0.9.2", {"position": v(11.85, -9) * mm});
            skPoint(sketch, "E25.0.9.3", {"position": v(-3.35, -9) * mm});
            skPoint(sketch, "E25.0.9.4", {"position": v(12.8, -9) * mm});
            skPoint(sketch, "E25.0.9.5", {"position": v(-2.4, -9) * mm});
            skPoint(sketch, "E25.0.9.6", {"position": v(13.75, -9) * mm});
            skPoint(sketch, "E25.0.9.7", {"position": v(-1.45, -9) * mm});
            skPoint(sketch, "E25.0.9.8", {"position": v(14.7, -9) * mm});
            skPoint(sketch, "E25.0.9.9", {"position": v(-0.5, -9) * mm});
            skPoint(sketch, "E25.0.9.11", {"position": v(15.65, -9) * mm});
            skPoint(sketch, "E25.0.9.12", {"position": v(0.45, -9) * mm});
            skPoint(sketch, "E25.0.9.14", {"position": v(16.6, -9) * mm});
            skPoint(sketch, "E25.0.9.15", {"position": v(1.4, -9) * mm});
            skPoint(sketch, "E25.0.9.17", {"position": v(17.55, -9) * mm});
            skPoint(sketch, "E25.0.9.18", {"position": v(2.35, -9) * mm});
            skPoint(sketch, "E25.0.9.19", {"position": v(-11.9, -9) * mm});
            skPoint(sketch, "E25.0.9.20", {"position": v(18.5, -9) * mm});
            skPoint(sketch, "E25.0.9.21", {"position": v(3.3, -9) * mm});
            skPoint(sketch, "E25.0.9.23", {"position": v(-10.95, -9) * mm});
            skPoint(sketch, "E25.0.9.25", {"position": v(4.25, -9) * mm});
            skPoint(sketch, "E25.0.9.26", {"position": v(9.95, -9) * mm});
            skPoint(sketch, "E25.0.9.27", {"position": v(6.15, -9) * mm});
            skPoint(sketch, "E25.0.9.28", {"position": v(-9.05, -9) * mm});
            skPoint(sketch, "E25.0.9.30", {"position": v(-5.25, -9) * mm});
            skPoint(sketch, "E25.0.9.31", {"position": v(-6.2, -9) * mm});
            skPoint(sketch, "E25.0.9.32", {"position": v(9, -9) * mm});
            skPoint(sketch, "E25.0.9.38", {"position": v(8.05, -9) * mm});
            skPoint(sketch, "E25.0.9.39", {"position": v(-7.15, -9) * mm});
            skPoint(sketch, "E25.0.9.40", {"position": v(5.2, -9) * mm});
            skPoint(sketch, "E25.0.9.41", {"position": v(-10, -9) * mm});
            skPoint(sketch, "E25.0.9.44", {"position": v(7.1, -9) * mm});
            skPoint(sketch, "E25.0.9.45", {"position": v(-8.1, -9) * mm});
            skLineSegment(sketch, "E25.0.9.54", {"start": v(18.85, -10) * mm, "end": v(18.15, -10) * mm});
            skLineSegment(sketch, "E25.0.9.55", {"start": v(18.85, -10) * mm, "end": v(18.85, -8) * mm});
            skLineSegment(sketch, "E25.0.9.56", {"start": v(18.15, -10) * mm, "end": v(18.15, -8) * mm});
            skLineSegment(sketch, "E25.0.9.67", {"start": v(17.9, -10) * mm, "end": v(17.2, -10) * mm});
            skLineSegment(sketch, "E25.0.9.69", {"start": v(17.9, -10) * mm, "end": v(17.9, -8) * mm});
            skLineSegment(sketch, "E25.0.9.71", {"start": v(17.2, -10) * mm, "end": v(17.2, -8) * mm});
            skLineSegment(sketch, "E25.0.9.72", {"start": v(16.95, -10) * mm, "end": v(16.25, -10) * mm});
            skLineSegment(sketch, "E25.0.9.74", {"start": v(16.95, -10) * mm, "end": v(16.95, -8) * mm});
            skLineSegment(sketch, "E25.0.9.79", {"start": v(16.25, -10) * mm, "end": v(16.25, -8) * mm});
            skLineSegment(sketch, "E25.0.9.80", {"start": v(16, -8) * mm, "end": v(15.3, -8) * mm});
            skLineSegment(sketch, "E25.0.9.81", {"start": v(12.2, -8) * mm, "end": v(11.5, -8) * mm});
            skLineSegment(sketch, "E25.0.9.83", {"start": v(16.95, -8) * mm, "end": v(16.25, -8) * mm});
            skLineSegment(sketch, "E25.0.9.84", {"start": v(13.15, -8) * mm, "end": v(12.45, -8) * mm});
            skLineSegment(sketch, "E25.0.9.85", {"start": v(9.35, -8) * mm, "end": v(8.65, -8) * mm});
            skLineSegment(sketch, "E25.0.9.86", {"start": v(5.55, -8) * mm, "end": v(4.85, -8) * mm});
            skLineSegment(sketch, "E25.0.9.87", {"start": v(8.4, -8) * mm, "end": v(7.7, -8) * mm});
            skLineSegment(sketch, "E25.0.9.90", {"start": v(13.4, -10) * mm, "end": v(13.4, -8) * mm});
            skLineSegment(sketch, "E25.0.9.91", {"start": v(9.6, -10) * mm, "end": v(9.6, -8) * mm});
            skLineSegment(sketch, "E25.0.9.92", {"start": v(5.8, -10) * mm, "end": v(5.8, -8) * mm});
            skLineSegment(sketch, "E25.0.9.94", {"start": v(10.3, -8) * mm, "end": v(9.6, -8) * mm});
            skLineSegment(sketch, "E25.0.9.95", {"start": v(6.5, -8) * mm, "end": v(5.8, -8) * mm});
            skLineSegment(sketch, "E25.0.9.96", {"start": v(17.9, -8) * mm, "end": v(17.2, -8) * mm});
            skLineSegment(sketch, "E25.0.9.97", {"start": v(14.1, -8) * mm, "end": v(13.4, -8) * mm});
            skLineSegment(sketch, "E25.0.9.99", {"start": v(15.05, -10) * mm, "end": v(14.35, -10) * mm});
            skLineSegment(sketch, "E25.0.9.100", {"start": v(11.25, -10) * mm, "end": v(11.25, -8) * mm});
            skLineSegment(sketch, "E25.0.9.101", {"start": v(7.45, -10) * mm, "end": v(7.45, -8) * mm});
            skLineSegment(sketch, "E25.0.9.102", {"start": v(15.05, -10) * mm, "end": v(15.05, -8) * mm});
            skLineSegment(sketch, "E25.0.9.104", {"start": v(10.55, -10) * mm, "end": v(10.55, -8) * mm});
            skLineSegment(sketch, "E25.0.9.105", {"start": v(6.75, -10) * mm, "end": v(6.75, -8) * mm});
            skLineSegment(sketch, "E25.0.9.106", {"start": v(14.35, -10) * mm, "end": v(14.35, -8) * mm});
            skLineSegment(sketch, "E25.0.9.108", {"start": v(11.25, -8) * mm, "end": v(10.55, -8) * mm});
            skLineSegment(sketch, "E25.0.9.109", {"start": v(7.45, -8) * mm, "end": v(6.75, -8) * mm});
            skLineSegment(sketch, "E25.0.9.110", {"start": v(18.85, -8) * mm, "end": v(18.15, -8) * mm});
            skLineSegment(sketch, "E25.0.9.111", {"start": v(15.05, -8) * mm, "end": v(14.35, -8) * mm});
            skLineSegment(sketch, "E25.0.9.113", {"start": v(16, -10) * mm, "end": v(16, -8) * mm});
            skLineSegment(sketch, "E25.0.9.114", {"start": v(12.2, -10) * mm, "end": v(12.2, -8) * mm});
            skLineSegment(sketch, "E25.0.9.115", {"start": v(8.4, -10) * mm, "end": v(8.4, -8) * mm});
            skLineSegment(sketch, "E25.0.9.116", {"start": v(4.6, -10) * mm, "end": v(4.6, -8) * mm});
            skLineSegment(sketch, "E25.0.9.117", {"start": v(13.15, -10) * mm, "end": v(13.15, -8) * mm});
            skLineSegment(sketch, "E25.0.9.118", {"start": v(9.35, -10) * mm, "end": v(9.35, -8) * mm});
            skLineSegment(sketch, "E25.0.9.119", {"start": v(16, -10) * mm, "end": v(15.3, -10) * mm});
            skLineSegment(sketch, "E25.0.9.121", {"start": v(15.3, -10) * mm, "end": v(15.3, -8) * mm});
            skLineSegment(sketch, "E25.0.9.122", {"start": v(11.5, -10) * mm, "end": v(11.5, -8) * mm});
            skLineSegment(sketch, "E25.0.9.123", {"start": v(7.7, -10) * mm, "end": v(7.7, -8) * mm});
            skLineSegment(sketch, "E25.0.9.127", {"start": v(4.85, -10) * mm, "end": v(4.85, -8) * mm});
            skLineSegment(sketch, "E25.0.9.128", {"start": v(12.45, -10) * mm, "end": v(12.45, -8) * mm});
            skLineSegment(sketch, "E25.0.9.129", {"start": v(-10.6, -8) * mm, "end": v(-11.3, -8) * mm});
            skLineSegment(sketch, "E25.0.9.130", {"start": v(-6.8, -8) * mm, "end": v(-7.5, -8) * mm});
            skLineSegment(sketch, "E25.0.9.131", {"start": v(1.75, -8) * mm, "end": v(1.05, -8) * mm});
            skLineSegment(sketch, "E25.0.9.132", {"start": v(-2.05, -8) * mm, "end": v(-2.75, -8) * mm});
            skLineSegment(sketch, "E25.0.9.133", {"start": v(-5.85, -8) * mm, "end": v(-6.55, -8) * mm});
            skLineSegment(sketch, "E25.0.9.134", {"start": v(0.8, -8) * mm, "end": v(0.1, -8) * mm});
            skLineSegment(sketch, "E25.0.9.135", {"start": v(-9.65, -8) * mm, "end": v(-10.35, -8) * mm});
            skLineSegment(sketch, "E25.0.9.136", {"start": v(-3, -8) * mm, "end": v(-3.7, -8) * mm});
            skLineSegment(sketch, "E25.0.9.139", {"start": v(2.7, -10) * mm, "end": v(2, -10) * mm});
            skLineSegment(sketch, "E25.0.9.140", {"start": v(-4.9, -10) * mm, "end": v(-5.6, -10) * mm});
            skLineSegment(sketch, "E25.0.9.141", {"start": v(-1.1, -10) * mm, "end": v(-1.8, -10) * mm});
            skLineSegment(sketch, "E25.0.9.142", {"start": v(-8.7, -10) * mm, "end": v(-9.4, -10) * mm});
            skLineSegment(sketch, "E25.0.9.143", {"start": v(14.1, -10) * mm, "end": v(13.4, -10) * mm});
            skLineSegment(sketch, "E25.0.9.144", {"start": v(10.3, -10) * mm, "end": v(9.6, -10) * mm});
            skLineSegment(sketch, "E25.0.9.145", {"start": v(6.5, -10) * mm, "end": v(5.8, -10) * mm});
            skLineSegment(sketch, "E25.0.9.147", {"start": v(4.6, -8) * mm, "end": v(3.9, -8) * mm});
            skLineSegment(sketch, "E25.0.9.148", {"start": v(2.7, -10) * mm, "end": v(2.7, -8) * mm});
            skLineSegment(sketch, "E25.0.9.149", {"start": v(-1.1, -10) * mm, "end": v(-1.1, -8) * mm});
            skLineSegment(sketch, "E25.0.9.150", {"start": v(-4.9, -10) * mm, "end": v(-4.9, -8) * mm});
            skLineSegment(sketch, "E25.0.9.151", {"start": v(-8.7, -10) * mm, "end": v(-8.7, -8) * mm});
            skLineSegment(sketch, "E25.0.9.152", {"start": v(14.1, -10) * mm, "end": v(14.1, -8) * mm});
            skLineSegment(sketch, "E25.0.9.153", {"start": v(10.3, -10) * mm, "end": v(10.3, -8) * mm});
            skLineSegment(sketch, "E25.0.9.154", {"start": v(6.5, -10) * mm, "end": v(6.5, -8) * mm});
            skLineSegment(sketch, "E25.0.9.157", {"start": v(2, -10) * mm, "end": v(2, -8) * mm});
            skLineSegment(sketch, "E25.0.9.158", {"start": v(-1.8, -10) * mm, "end": v(-1.8, -8) * mm});
            skLineSegment(sketch, "E25.0.9.159", {"start": v(-5.6, -10) * mm, "end": v(-5.6, -8) * mm});
            skLineSegment(sketch, "E25.0.9.160", {"start": v(-9.4, -10) * mm, "end": v(-9.4, -8) * mm});
            skLineSegment(sketch, "E25.0.9.161", {"start": v(1.75, -10) * mm, "end": v(1.05, -10) * mm});
            skLineSegment(sketch, "E25.0.9.162", {"start": v(-2.05, -10) * mm, "end": v(-2.75, -10) * mm});
            skLineSegment(sketch, "E25.0.9.163", {"start": v(-5.85, -10) * mm, "end": v(-6.55, -10) * mm});
            skLineSegment(sketch, "E25.0.9.164", {"start": v(-9.65, -10) * mm, "end": v(-10.35, -10) * mm});
            skLineSegment(sketch, "E25.0.9.165", {"start": v(-4.9, -8) * mm, "end": v(-5.6, -8) * mm});
            skLineSegment(sketch, "E25.0.9.166", {"start": v(-8.7, -8) * mm, "end": v(-9.4, -8) * mm});
            skLineSegment(sketch, "E25.0.9.167", {"start": v(2.7, -8) * mm, "end": v(2, -8) * mm});
            skLineSegment(sketch, "E25.0.9.168", {"start": v(13.15, -10) * mm, "end": v(12.45, -10) * mm});
            skLineSegment(sketch, "E25.0.9.169", {"start": v(9.35, -10) * mm, "end": v(8.65, -10) * mm});
            skLineSegment(sketch, "E25.0.9.170", {"start": v(-1.1, -8) * mm, "end": v(-1.8, -8) * mm});
            skLineSegment(sketch, "E25.0.9.171", {"start": v(5.55, -10) * mm, "end": v(4.85, -10) * mm});
            skLineSegment(sketch, "E25.0.9.172", {"start": v(-3.95, -10) * mm, "end": v(-4.65, -10) * mm});
            skLineSegment(sketch, "E25.0.9.173", {"start": v(-7.75, -10) * mm, "end": v(-8.45, -10) * mm});
            skLineSegment(sketch, "E25.0.9.174", {"start": v(-11.55, -10) * mm, "end": v(-12.25, -10) * mm});
            skLineSegment(sketch, "E25.0.9.176", {"start": v(11.25, -10) * mm, "end": v(10.55, -10) * mm});
            skLineSegment(sketch, "E25.0.9.177", {"start": v(7.45, -10) * mm, "end": v(6.75, -10) * mm});
            skLineSegment(sketch, "E25.0.9.178", {"start": v(3.65, -10) * mm, "end": v(2.95, -10) * mm});
            skLineSegment(sketch, "E25.0.9.179", {"start": v(-0.15, -10) * mm, "end": v(-0.85, -10) * mm});
            skLineSegment(sketch, "E25.0.9.180", {"start": v(-3.95, -10) * mm, "end": v(-3.95, -8) * mm});
            skLineSegment(sketch, "E25.0.9.181", {"start": v(-7.75, -10) * mm, "end": v(-7.75, -8) * mm});
            skLineSegment(sketch, "E25.0.9.182", {"start": v(-11.55, -10) * mm, "end": v(-11.55, -8) * mm});
            skLineSegment(sketch, "E25.0.9.184", {"start": v(3.65, -10) * mm, "end": v(3.65, -8) * mm});
            skLineSegment(sketch, "E25.0.9.185", {"start": v(-0.15, -10) * mm, "end": v(-0.15, -8) * mm});
            skLineSegment(sketch, "E25.0.9.186", {"start": v(-4.65, -10) * mm, "end": v(-4.65, -8) * mm});
            skLineSegment(sketch, "E25.0.9.187", {"start": v(-8.45, -10) * mm, "end": v(-8.45, -8) * mm});
            skLineSegment(sketch, "E25.0.9.188", {"start": v(-12.25, -10) * mm, "end": v(-12.25, -8) * mm});
            skLineSegment(sketch, "E25.0.9.189", {"start": v(2.95, -10) * mm, "end": v(2.95, -8) * mm});
            skLineSegment(sketch, "E25.0.9.190", {"start": v(-0.85, -10) * mm, "end": v(-0.85, -8) * mm});
            skLineSegment(sketch, "E25.0.9.191", {"start": v(-3.95, -8) * mm, "end": v(-4.65, -8) * mm});
            skLineSegment(sketch, "E25.0.9.192", {"start": v(-7.75, -8) * mm, "end": v(-8.45, -8) * mm});
            skLineSegment(sketch, "E25.0.9.193", {"start": v(-11.55, -8) * mm, "end": v(-12.25, -8) * mm});
            skLineSegment(sketch, "E25.0.9.194", {"start": v(3.65, -8) * mm, "end": v(2.95, -8) * mm});
            skLineSegment(sketch, "E25.0.9.195", {"start": v(-0.15, -8) * mm, "end": v(-0.85, -8) * mm});
            skLineSegment(sketch, "E25.0.9.196", {"start": v(0.8, -10) * mm, "end": v(0.8, -8) * mm});
            skLineSegment(sketch, "E25.0.9.197", {"start": v(-3, -10) * mm, "end": v(-3, -8) * mm});
            skLineSegment(sketch, "E25.0.9.198", {"start": v(-6.8, -10) * mm, "end": v(-6.8, -8) * mm});
            skLineSegment(sketch, "E25.0.9.199", {"start": v(-10.6, -10) * mm, "end": v(-10.6, -8) * mm});
            skLineSegment(sketch, "E25.0.9.200", {"start": v(1.75, -10) * mm, "end": v(1.75, -8) * mm});
            skLineSegment(sketch, "E25.0.9.201", {"start": v(-2.05, -10) * mm, "end": v(-2.05, -8) * mm});
            skLineSegment(sketch, "E25.0.9.202", {"start": v(-5.85, -10) * mm, "end": v(-5.85, -8) * mm});
            skLineSegment(sketch, "E25.0.9.204", {"start": v(5.55, -10) * mm, "end": v(5.55, -8) * mm});
            skLineSegment(sketch, "E25.0.9.206", {"start": v(-3, -10) * mm, "end": v(-3.7, -10) * mm});
            skLineSegment(sketch, "E25.0.9.207", {"start": v(-6.8, -10) * mm, "end": v(-7.5, -10) * mm});
            skLineSegment(sketch, "E25.0.9.208", {"start": v(-10.6, -10) * mm, "end": v(-11.3, -10) * mm});
            skLineSegment(sketch, "E25.0.9.210", {"start": v(12.2, -10) * mm, "end": v(11.5, -10) * mm});
            skLineSegment(sketch, "E25.0.9.211", {"start": v(8.4, -10) * mm, "end": v(7.7, -10) * mm});
            skLineSegment(sketch, "E25.0.9.212", {"start": v(4.6, -10) * mm, "end": v(3.9, -10) * mm});
            skLineSegment(sketch, "E25.0.9.213", {"start": v(0.8, -10) * mm, "end": v(0.1, -10) * mm});
            skLineSegment(sketch, "E25.0.9.214", {"start": v(0.1, -10) * mm, "end": v(0.1, -8) * mm});
            skLineSegment(sketch, "E25.0.9.215", {"start": v(-3.7, -10) * mm, "end": v(-3.7, -8) * mm});
            skLineSegment(sketch, "E25.0.9.216", {"start": v(-7.5, -10) * mm, "end": v(-7.5, -8) * mm});
            skLineSegment(sketch, "E25.0.9.217", {"start": v(-11.3, -10) * mm, "end": v(-11.3, -8) * mm});
            skLineSegment(sketch, "E25.0.9.218", {"start": v(3.9, -10) * mm, "end": v(3.9, -8) * mm});
            skLineSegment(sketch, "E25.0.9.219", {"start": v(1.05, -10) * mm, "end": v(1.05, -8) * mm});
            skLineSegment(sketch, "E25.0.9.220", {"start": v(-2.75, -10) * mm, "end": v(-2.75, -8) * mm});
            skLineSegment(sketch, "E25.0.9.221", {"start": v(-6.55, -10) * mm, "end": v(-6.55, -8) * mm});
            skLineSegment(sketch, "E25.0.9.222", {"start": v(-10.35, -10) * mm, "end": v(-10.35, -8) * mm});
            skLineSegment(sketch, "E25.0.9.224", {"start": v(8.65, -10) * mm, "end": v(8.65, -8) * mm});
            skLineSegment(sketch, "E25.0.9.225", {"start": v(-9.65, -10) * mm, "end": v(-9.65, -8) * mm});
            skLineSegment(sketch, "E26", {"start": v(0.1, -1) * mm, "end": v(0.1, 1) * mm});
            skLineSegment(sketch, "E27", {"start": v(0.1, 1) * mm, "end": v(0.8, 1) * mm});
            skLineSegment(sketch, "E28", {"start": v(-0.15, -1.25) * mm, "end": v(-0.85, -1.25) * mm});
            skLineSegment(sketch, "E29", {"start": v(-1.8, -1) * mm, "end": v(-1.8, 1) * mm});
            skLineSegment(sketch, "E30", {"start": v(-1.8, 1) * mm, "end": v(-1.1, 1) * mm});
            skLineSegment(sketch, "E31", {"start": v(2.7, -1) * mm, "end": v(2, -1) * mm});
            skLineSegment(sketch, "E32", {"start": v(2, -1) * mm, "end": v(2, 1) * mm});
            skPoint(sketch, "E33.0.1.0", {"position": v(-8.1, -11.25) * mm});
            skPoint(sketch, "E33.0.1.1", {"position": v(10.9, -11.25) * mm});
            skPoint(sketch, "E33.0.1.2", {"position": v(17.55, -11.25) * mm});
            skPoint(sketch, "E33.0.1.4", {"position": v(15.65, -11.25) * mm});
            skLineSegment(sketch, "E33.0.1.7", {"start": v(10.3, -10.25) * mm, "end": v(9.6, -10.25) * mm});
            skLineSegment(sketch, "E33.0.1.8", {"start": v(-1.8, -12.25) * mm, "end": v(-1.8, -10.25) * mm});
            skLineSegment(sketch, "E33.0.1.9", {"start": v(-10.35, -12.25) * mm, "end": v(-10.35, -10.25) * mm});
            skLineSegment(sketch, "E33.0.1.10", {"start": v(18.85, -10.25) * mm, "end": v(18.15, -10.25) * mm});
            skPoint(sketch, "E33.0.1.11", {"position": v(6.15, -11.25) * mm});
            skPoint(sketch, "E33.0.1.12", {"position": v(-9.05, -11.25) * mm});
            skLineSegment(sketch, "E33.0.1.14", {"start": v(-3, -10.25) * mm, "end": v(-3.7, -10.25) * mm});
            skPoint(sketch, "E33.0.1.15", {"position": v(12.8, -11.25) * mm});
            skPoint(sketch, "E33.0.1.16", {"position": v(18.5, -11.25) * mm});
            skLineSegment(sketch, "E33.0.1.17", {"start": v(8.4, -10.25) * mm, "end": v(7.7, -10.25) * mm});
            skLineSegment(sketch, "E33.0.1.19", {"start": v(-8.7, -12.25) * mm, "end": v(-8.7, -10.25) * mm});
            skPoint(sketch, "E33.0.1.20", {"position": v(11.85, -11.25) * mm});
            skPoint(sketch, "E33.0.1.21", {"position": v(2.35, -11.25) * mm});
            skLineSegment(sketch, "E33.0.1.23", {"start": v(4.85, -12.25) * mm, "end": v(4.85, -10.25) * mm});
            skLineSegment(sketch, "E33.0.1.24", {"start": v(6.5, -10.25) * mm, "end": v(5.8, -10.25) * mm});
            skLineSegment(sketch, "E33.0.1.25", {"start": v(15.05, -10.25) * mm, "end": v(14.35, -10.25) * mm});
            skLineSegment(sketch, "E33.0.1.26", {"start": v(-3.95, -10.25) * mm, "end": v(-4.65, -10.25) * mm});
            skLineSegment(sketch, "E33.0.1.27", {"start": v(-5.6, -12.25) * mm, "end": v(-5.6, -10.25) * mm});
            skPoint(sketch, "E33.0.1.28", {"position": v(14.7, -11.25) * mm});
            skPoint(sketch, "E33.0.1.29", {"position": v(4.25, -11.25) * mm});
            skPoint(sketch, "E33.0.1.30", {"position": v(3.3, -11.25) * mm});
            skPoint(sketch, "E33.0.1.31", {"position": v(-2.4, -11.25) * mm});
            skPoint(sketch, "E33.0.1.32", {"position": v(8.05, -11.25) * mm});
            skLineSegment(sketch, "E33.0.1.34", {"start": v(12.2, -10.25) * mm, "end": v(11.5, -10.25) * mm});
            skLineSegment(sketch, "E33.0.1.36", {"start": v(-10.6, -10.25) * mm, "end": v(-11.3, -10.25) * mm});
            skPoint(sketch, "E33.0.1.37", {"position": v(-3.35, -11.25) * mm});
            skLineSegment(sketch, "E33.0.1.38", {"start": v(14.1, -10.25) * mm, "end": v(13.4, -10.25) * mm});
            skPoint(sketch, "E33.0.1.39", {"position": v(-11.9, -11.25) * mm});
            skLineSegment(sketch, "E33.0.1.40", {"start": v(-9.65, -12.25) * mm, "end": v(-9.65, -10.25) * mm});
            skLineSegment(sketch, "E33.0.1.41", {"start": v(-11.55, -10.25) * mm, "end": v(-12.25, -10.25) * mm});
            skLineSegment(sketch, "E33.0.1.42", {"start": v(8.65, -12.25) * mm, "end": v(8.65, -10.25) * mm});
            skLineSegment(sketch, "E33.0.1.43", {"start": v(2.7, -10.25) * mm, "end": v(2, -10.25) * mm});
            skLineSegment(sketch, "E33.0.1.48", {"start": v(-6.8, -10.25) * mm, "end": v(-7.5, -10.25) * mm});
            skLineSegment(sketch, "E33.0.1.49", {"start": v(12.2, -12.25) * mm, "end": v(12.2, -10.25) * mm});
            skLineSegment(sketch, "E33.0.1.50", {"start": v(16, -10.25) * mm, "end": v(15.3, -10.25) * mm});
            skLineSegment(sketch, "E33.0.1.52", {"start": v(12.45, -12.25) * mm, "end": v(12.45, -10.25) * mm});
            skLineSegment(sketch, "E33.0.1.53", {"start": v(17.9, -10.25) * mm, "end": v(17.2, -10.25) * mm});
            skLineSegment(sketch, "E33.0.1.55", {"start": v(-7.75, -10.25) * mm, "end": v(-8.45, -10.25) * mm});
            skLineSegment(sketch, "E33.0.1.56", {"start": v(-9.4, -12.25) * mm, "end": v(-9.4, -10.25) * mm});
            skPoint(sketch, "E33.0.1.57", {"position": v(-7.15, -11.25) * mm});
            skPoint(sketch, "E33.0.1.58", {"position": v(13.75, -11.25) * mm});
            skLineSegment(sketch, "E33.0.1.59", {"start": v(3.65, -10.25) * mm, "end": v(2.95, -10.25) * mm});
            skLineSegment(sketch, "E33.0.1.60", {"start": v(16.95, -10.25) * mm, "end": v(16.25, -10.25) * mm});
            skLineSegment(sketch, "E33.0.1.61", {"start": v(4.6, -10.25) * mm, "end": v(3.9, -10.25) * mm});
            skLineSegment(sketch, "E33.0.1.63", {"start": v(1.75, -10.25) * mm, "end": v(1.05, -10.25) * mm});
            skLineSegment(sketch, "E33.0.1.64", {"start": v(8.4, -12.25) * mm, "end": v(8.4, -10.25) * mm});
            skLineSegment(sketch, "E33.0.1.65", {"start": v(-0.15, -10.25) * mm, "end": v(-0.85, -10.25) * mm});
            skPoint(sketch, "E33.0.1.66", {"position": v(5.2, -11.25) * mm});
            skPoint(sketch, "E33.0.1.67", {"position": v(-5.25, -11.25) * mm});
            skPoint(sketch, "E33.0.1.68", {"position": v(-1.45, -11.25) * mm});
            skLineSegment(sketch, "E33.0.1.70", {"start": v(-8.7, -10.25) * mm, "end": v(-9.4, -10.25) * mm});
            skLineSegment(sketch, "E33.0.1.71", {"start": v(5.55, -10.25) * mm, "end": v(4.85, -10.25) * mm});
            skLineSegment(sketch, "E33.0.1.72", {"start": v(-5.85, -10.25) * mm, "end": v(-6.55, -10.25) * mm});
            skLineSegment(sketch, "E33.0.1.73", {"start": v(13.15, -10.25) * mm, "end": v(12.45, -10.25) * mm});
            skLineSegment(sketch, "E33.0.1.74", {"start": v(-2.05, -10.25) * mm, "end": v(-2.75, -10.25) * mm});
            skLineSegment(sketch, "E33.0.1.76", {"start": v(-9.65, -10.25) * mm, "end": v(-10.35, -10.25) * mm});
            skLineSegment(sketch, "E33.0.1.77", {"start": v(9.35, -10.25) * mm, "end": v(8.65, -10.25) * mm});
            skLineSegment(sketch, "E33.0.1.78", {"start": v(-4.9, -10.25) * mm, "end": v(-5.6, -10.25) * mm});
            skLineSegment(sketch, "E33.0.1.79", {"start": v(13.15, -12.25) * mm, "end": v(13.15, -10.25) * mm});
            skPoint(sketch, "E33.0.1.80", {"position": v(9.95, -11.25) * mm});
            skPoint(sketch, "E33.0.1.82", {"position": v(-0.5, -11.25) * mm});
            skLineSegment(sketch, "E33.0.1.84", {"start": v(-4.9, -12.25) * mm, "end": v(-4.9, -10.25) * mm});
            skLineSegment(sketch, "E33.0.1.85", {"start": v(0.8, -10.25) * mm, "end": v(0.1, -10.25) * mm});
            skLineSegment(sketch, "E33.0.1.86", {"start": v(0.1, -12.25) * mm, "end": v(0.1, -10.25) * mm});
            skLineSegment(sketch, "E33.0.1.87", {"start": v(9.35, -12.25) * mm, "end": v(9.35, -10.25) * mm});
            skLineSegment(sketch, "E33.0.1.90", {"start": v(-5.85, -12.25) * mm, "end": v(-5.85, -10.25) * mm});
            skLineSegment(sketch, "E33.0.1.91", {"start": v(-1.1, -10.25) * mm, "end": v(-1.8, -10.25) * mm});
            skPoint(sketch, "E33.0.1.93", {"position": v(16.6, -11.25) * mm});
            skPoint(sketch, "E33.0.1.94", {"position": v(-6.2, -11.25) * mm});
            skPoint(sketch, "E33.0.1.95", {"position": v(0.45, -11.25) * mm});
            skPoint(sketch, "E33.0.1.96", {"position": v(-10.95, -11.25) * mm});
            skPoint(sketch, "E33.0.1.97", {"position": v(7.1, -11.25) * mm});
            skLineSegment(sketch, "E33.0.1.98", {"start": v(-2.05, -12.25) * mm, "end": v(-2.05, -10.25) * mm});
            skPoint(sketch, "E33.0.1.99", {"position": v(1.4, -11.25) * mm});
            skPoint(sketch, "E33.0.1.100", {"position": v(9, -11.25) * mm});
            skLineSegment(sketch, "E33.0.1.103", {"start": v(7.7, -12.25) * mm, "end": v(7.7, -10.25) * mm});
            skLineSegment(sketch, "E33.0.1.104", {"start": v(11.25, -10.25) * mm, "end": v(10.55, -10.25) * mm});
            skLineSegment(sketch, "E33.0.1.105", {"start": v(-2.75, -12.25) * mm, "end": v(-2.75, -10.25) * mm});
            skLineSegment(sketch, "E33.0.1.106", {"start": v(5.55, -12.25) * mm, "end": v(5.55, -10.25) * mm});
            skPoint(sketch, "E33.0.1.108", {"position": v(-4.3, -11.25) * mm});
            skLineSegment(sketch, "E33.0.1.113", {"start": v(2, -12.25) * mm, "end": v(2, -10.25) * mm});
            skLineSegment(sketch, "E33.0.1.115", {"start": v(7.45, -10.25) * mm, "end": v(6.75, -10.25) * mm});
            skLineSegment(sketch, "E33.0.1.116", {"start": v(-6.55, -12.25) * mm, "end": v(-6.55, -10.25) * mm});
            skLineSegment(sketch, "E33.0.1.119", {"start": v(-0.85, -12.25) * mm, "end": v(-0.85, -10.25) * mm});
            skLineSegment(sketch, "E33.0.1.120", {"start": v(17.2, -12.25) * mm, "end": v(17.2, -10.25) * mm});
            skLineSegment(sketch, "E33.0.1.122", {"start": v(18.85, -12.25) * mm, "end": v(18.85, -10.25) * mm});
            skLineSegment(sketch, "E33.0.1.123", {"start": v(14.1, -12.25) * mm, "end": v(14.1, -10.25) * mm});
            skLineSegment(sketch, "E33.0.1.125", {"start": v(-7.5, -12.25) * mm, "end": v(-7.5, -10.25) * mm});
            skLineSegment(sketch, "E33.0.1.126", {"start": v(10.55, -12.25) * mm, "end": v(10.55, -10.25) * mm});
            skLineSegment(sketch, "E33.0.1.127", {"start": v(3.65, -12.25) * mm, "end": v(3.65, -10.25) * mm});
            skLineSegment(sketch, "E33.0.1.128", {"start": v(1.75, -12.25) * mm, "end": v(1.75, -10.25) * mm});
            skLineSegment(sketch, "E33.0.1.130", {"start": v(16.25, -12.25) * mm, "end": v(16.25, -10.25) * mm});
            skLineSegment(sketch, "E33.0.1.131", {"start": v(16, -12.25) * mm, "end": v(16, -10.25) * mm});
            skLineSegment(sketch, "E33.0.1.132", {"start": v(-0.15, -12.25) * mm, "end": v(-0.15, -10.25) * mm});
            skLineSegment(sketch, "E33.0.1.133", {"start": v(-11.3, -12.25) * mm, "end": v(-11.3, -10.25) * mm});
            skLineSegment(sketch, "E33.0.1.134", {"start": v(-6.8, -12.25) * mm, "end": v(-6.8, -10.25) * mm});
            skLineSegment(sketch, "E33.0.1.135", {"start": v(11.25, -12.25) * mm, "end": v(11.25, -10.25) * mm});
            skLineSegment(sketch, "E33.0.1.137", {"start": v(2.7, -12.25) * mm, "end": v(2.7, -10.25) * mm});
            skLineSegment(sketch, "E33.0.1.138", {"start": v(4.6, -12.25) * mm, "end": v(4.6, -10.25) * mm});
            skLineSegment(sketch, "E33.0.1.139", {"start": v(-3.95, -12.25) * mm, "end": v(-3.95, -10.25) * mm});
            skLineSegment(sketch, "E33.0.1.140", {"start": v(0.8, -12.25) * mm, "end": v(0.8, -10.25) * mm});
            skLineSegment(sketch, "E33.0.1.141", {"start": v(-3.7, -12.25) * mm, "end": v(-3.7, -10.25) * mm});
            skPoint(sketch, "E33.0.1.142", {"position": v(-10, -11.25) * mm});
            skLineSegment(sketch, "E33.0.1.144", {"start": v(18.15, -12.25) * mm, "end": v(18.15, -10.25) * mm});
            skLineSegment(sketch, "E33.0.1.145", {"start": v(10.3, -12.25) * mm, "end": v(10.3, -10.25) * mm});
            skLineSegment(sketch, "E33.0.1.146", {"start": v(15.3, -12.25) * mm, "end": v(15.3, -10.25) * mm});
            skLineSegment(sketch, "E33.0.1.147", {"start": v(6.75, -12.25) * mm, "end": v(6.75, -10.25) * mm});
            skLineSegment(sketch, "E33.0.1.148", {"start": v(-10.6, -12.25) * mm, "end": v(-10.6, -10.25) * mm});
            skLineSegment(sketch, "E33.0.1.150", {"start": v(7.45, -12.25) * mm, "end": v(7.45, -10.25) * mm});
            skLineSegment(sketch, "E33.0.1.152", {"start": v(17.9, -12.25) * mm, "end": v(17.9, -10.25) * mm});
            skLineSegment(sketch, "E33.0.1.153", {"start": v(-1.1, -12.25) * mm, "end": v(-1.1, -10.25) * mm});
            skLineSegment(sketch, "E33.0.1.155", {"start": v(-7.75, -12.25) * mm, "end": v(-7.75, -10.25) * mm});
            skLineSegment(sketch, "E33.0.1.156", {"start": v(-3, -12.25) * mm, "end": v(-3, -10.25) * mm});
            skLineSegment(sketch, "E33.0.1.158", {"start": v(15.05, -12.25) * mm, "end": v(15.05, -10.25) * mm});
            skLineSegment(sketch, "E33.0.1.159", {"start": v(-11.55, -12.25) * mm, "end": v(-11.55, -10.25) * mm});
            skLineSegment(sketch, "E33.0.1.160", {"start": v(16.95, -12.25) * mm, "end": v(16.95, -10.25) * mm});
            skLineSegment(sketch, "E33.0.1.161", {"start": v(13.4, -12.25) * mm, "end": v(13.4, -10.25) * mm});
            skLineSegment(sketch, "E33.0.1.162", {"start": v(6.5, -12.25) * mm, "end": v(6.5, -10.25) * mm});
            skLineSegment(sketch, "E33.0.1.163", {"start": v(14.35, -12.25) * mm, "end": v(14.35, -10.25) * mm});
            skLineSegment(sketch, "E33.0.1.164", {"start": v(11.5, -12.25) * mm, "end": v(11.5, -10.25) * mm});
            skLineSegment(sketch, "E33.0.1.165", {"start": v(3.9, -12.25) * mm, "end": v(3.9, -10.25) * mm});
            skLineSegment(sketch, "E33.0.1.166", {"start": v(-4.65, -12.25) * mm, "end": v(-4.65, -10.25) * mm});
            skLineSegment(sketch, "E33.0.1.167", {"start": v(9.6, -12.25) * mm, "end": v(9.6, -10.25) * mm});
            skLineSegment(sketch, "E33.0.1.168", {"start": v(1.05, -12.25) * mm, "end": v(1.05, -10.25) * mm});
            skLineSegment(sketch, "E33.0.1.169", {"start": v(-8.45, -12.25) * mm, "end": v(-8.45, -10.25) * mm});
            skLineSegment(sketch, "E33.0.1.170", {"start": v(5.8, -12.25) * mm, "end": v(5.8, -10.25) * mm});
            skLineSegment(sketch, "E33.0.1.173", {"start": v(-12.25, -12.25) * mm, "end": v(-12.25, -10.25) * mm});
            skLineSegment(sketch, "E33.0.1.175", {"start": v(2.95, -12.25) * mm, "end": v(2.95, -10.25) * mm});
            skLineSegment(sketch, "E33.0.1.180", {"start": v(-8.7, -12.25) * mm, "end": v(-9.4, -12.25) * mm});
            skLineSegment(sketch, "E33.0.1.181", {"start": v(-11.55, -12.25) * mm, "end": v(-12.25, -12.25) * mm});
            skLineSegment(sketch, "E33.0.1.182", {"start": v(16.95, -12.25) * mm, "end": v(16.25, -12.25) * mm});
            skLineSegment(sketch, "E33.0.1.183", {"start": v(13.15, -12.25) * mm, "end": v(12.45, -12.25) * mm});
            skLineSegment(sketch, "E33.0.1.184", {"start": v(18.85, -12.25) * mm, "end": v(18.15, -12.25) * mm});
            skLineSegment(sketch, "E33.0.1.186", {"start": v(6.5, -12.25) * mm, "end": v(5.8, -12.25) * mm});
            skLineSegment(sketch, "E33.0.1.188", {"start": v(16, -12.25) * mm, "end": v(15.3, -12.25) * mm});
            skLineSegment(sketch, "E33.0.1.189", {"start": v(11.25, -12.25) * mm, "end": v(10.55, -12.25) * mm});
            skLineSegment(sketch, "E33.0.1.190", {"start": v(12.2, -12.25) * mm, "end": v(11.5, -12.25) * mm});
            skLineSegment(sketch, "E33.0.1.191", {"start": v(17.9, -12.25) * mm, "end": v(17.2, -12.25) * mm});
            skLineSegment(sketch, "E33.0.1.192", {"start": v(15.05, -12.25) * mm, "end": v(14.35, -12.25) * mm});
            skLineSegment(sketch, "E33.0.1.193", {"start": v(8.4, -12.25) * mm, "end": v(7.7, -12.25) * mm});
            skLineSegment(sketch, "E33.0.1.194", {"start": v(4.6, -12.25) * mm, "end": v(3.9, -12.25) * mm});
            skLineSegment(sketch, "E33.0.1.196", {"start": v(-9.65, -12.25) * mm, "end": v(-10.35, -12.25) * mm});
            skLineSegment(sketch, "E33.0.1.198", {"start": v(9.35, -12.25) * mm, "end": v(8.65, -12.25) * mm});
            skLineSegment(sketch, "E33.0.1.200", {"start": v(5.55, -12.25) * mm, "end": v(4.85, -12.25) * mm});
            skLineSegment(sketch, "E33.0.1.201", {"start": v(-7.75, -12.25) * mm, "end": v(-8.45, -12.25) * mm});
            skLineSegment(sketch, "E33.0.1.202", {"start": v(-3, -12.25) * mm, "end": v(-3.7, -12.25) * mm});
            skLineSegment(sketch, "E33.0.1.203", {"start": v(14.1, -12.25) * mm, "end": v(13.4, -12.25) * mm});
            skLineSegment(sketch, "E33.0.1.204", {"start": v(-6.8, -12.25) * mm, "end": v(-7.5, -12.25) * mm});
            skLineSegment(sketch, "E33.0.1.206", {"start": v(1.75, -12.25) * mm, "end": v(1.05, -12.25) * mm});
            skLineSegment(sketch, "E33.0.1.207", {"start": v(7.45, -12.25) * mm, "end": v(6.75, -12.25) * mm});
            skLineSegment(sketch, "E33.0.1.209", {"start": v(10.3, -12.25) * mm, "end": v(9.6, -12.25) * mm});
            skLineSegment(sketch, "E33.0.1.210", {"start": v(-10.6, -12.25) * mm, "end": v(-11.3, -12.25) * mm});
            skLineSegment(sketch, "E33.0.1.211", {"start": v(-2.05, -12.25) * mm, "end": v(-2.75, -12.25) * mm});
            skLineSegment(sketch, "E33.0.1.212", {"start": v(3.65, -12.25) * mm, "end": v(2.95, -12.25) * mm});
            skLineSegment(sketch, "E33.0.1.213", {"start": v(-5.85, -12.25) * mm, "end": v(-6.55, -12.25) * mm});
            skLineSegment(sketch, "E33.0.1.214", {"start": v(-0.15, -12.25) * mm, "end": v(-0.85, -12.25) * mm});
            skLineSegment(sketch, "E33.0.1.215", {"start": v(0.8, -12.25) * mm, "end": v(0.1, -12.25) * mm});
            skLineSegment(sketch, "E33.0.1.217", {"start": v(2.7, -12.25) * mm, "end": v(2, -12.25) * mm});
            skLineSegment(sketch, "E33.0.1.219", {"start": v(-4.9, -12.25) * mm, "end": v(-5.6, -12.25) * mm});
            skLineSegment(sketch, "E33.0.1.220", {"start": v(-3.95, -12.25) * mm, "end": v(-4.65, -12.25) * mm});
            skLineSegment(sketch, "E33.0.1.221", {"start": v(-1.1, -12.25) * mm, "end": v(-1.8, -12.25) * mm});
            skLineSegment(sketch, "E34", {"start": v(-12.25, -12.25) * mm, "end": v(18.85, -12.25) * mm});
            skLineSegment(sketch, "E35", {"start": v(18.85, -12.25) * mm, "end": v(18.85, 14.5) * mm});
            skLineSegment(sketch, "E36", {"start": v(18.85, 14.5) * mm, "end": v(-12.25, 14.5) * mm});
            skLineSegment(sketch, "E37", {"start": v(-12.25, 14.5) * mm, "end": v(-12.25, -12.25) * mm});
            skCircle(sketch, "E38.0", {"center": v(0, 0) * mm, "radius": 12.25 * mm});
            skSolve(sketch);
        }
        {
            var Q0;
            Q0=qCreatedBy(makeId("Top.planeOp"),FACE);
            cPlane(context, id + "F4", {"entities" : qUnion([Q0]), "cplaneType" : CPlaneType.OFFSET, "offset" : 20 * mm, "width" : 150 * mm, "height" : 150 * mm});
        }
        {
            var Q0;
            Q0=qCreatedBy(id+"F4.planeOp",FACE);
            var sketch = newSketch(context, id + "F5", { "sketchPlane" : qUnion([Q0])});
            skLineSegment(sketch, "E39.0", {"start": v(18.85, 14.5) * mm, "end": v(-12.25, 14.5) * mm});
            skLineSegment(sketch, "E40.0", {"start": v(-12.25, 14.5) * mm, "end": v(-12.25, -11.75) * mm});
            skLineSegment(sketch, "E41.0", {"start": v(18.85, -11.75) * mm, "end": v(18.85, 14.5) * mm});
            skLineSegment(sketch, "E42.0", {"start": v(18.85, -11.75) * mm, "end": v(-12.25, -11.75) * mm});
            skCircle(sketch, "E43.0", {"center": v(8.98, -6) * mm, "radius": 4.25 * mm});
            skCircle(sketch, "E44.0", {"center": v(9.07, 5.86) * mm, "radius": 4.25 * mm});
            skCircle(sketch, "E45.0", {"center": v(0, 0) * mm, "radius": 3.5 * mm});
            skPoint(sketch, "E46.orphan", {"position": v(-12.25, -12.25) * mm});
            skPoint(sketch, "E47.orphan", {"position": v(-22.5, -11.75) * mm});
            skPoint(sketch, "E48.orphan", {"position": v(22.5, -11.75) * mm});
            skPoint(sketch, "E49.orphan", {"position": v(18.85, -12.25) * mm});
            skSolve(sketch);
        }
        {
            var Q0;
            Q0=makeQuery(id+"F5.imprint","IMPRINT",FACE,{"disambiguationData":[TD([[makeQuery(id+"F5.imprint","IMPRINT",EDGE,{"derivedFrom":sQuery(id+"F5.wireOp",EDGE,"E39.0")}),1.0]])]});
            extrude(context, id + "F6", {"entities" : qUnion([Q0]), "depth" : 1.2 * mm, "offsetDistance" : 25 * mm});
        }
        {
            var Q0;
            Q0=makeQuery(id+"F6.opExtrude","SWEPT_EDGE",EDGE,{"disambiguationData":[OSD([sQuery(id+"F5.wireOp",EDGE,"E39.0"),sQuery(id+"F5.wireOp",EDGE,"E40.0")])]});
            var Q1;
            Q1=makeQuery(id+"F6.opExtrude","SWEPT_EDGE",EDGE,{"disambiguationData":[OSD([sQuery(id+"F5.wireOp",EDGE,"E40.0"),sQuery(id+"F5.wireOp",EDGE,"E42.0")])]});
            var Q2;
            Q2=makeQuery(id+"F6.opExtrude","SWEPT_EDGE",EDGE,{"disambiguationData":[OSD([sQuery(id+"F5.wireOp",EDGE,"E39.0"),sQuery(id+"F5.wireOp",EDGE,"E41.0")])]});
            var Q3;
            Q3=makeQuery(id+"F6.opExtrude","SWEPT_EDGE",EDGE,{"disambiguationData":[OSD([sQuery(id+"F5.wireOp",EDGE,"E41.0"),sQuery(id+"F5.wireOp",EDGE,"E42.0")])]});
            fillet(context, id + "F7", {"entities" : qUnion([Q0, Q1, Q2, Q3]), "radius" : 1 * mm, "tangentPropagation" : true, "allowEdgeOverflow" : false});
        }
        {
            var Q0;
            {var subQ0=sQuery(id+"F1.wireOp",EDGE,"E5.right");Q0=makeQuery(id+"F1.imprint","IMPRINT",FACE,{"disambiguationData":[TD([[makeQuery(id+"F1.imprint","IMPRINT",EDGE,{"derivedFrom":subQ0}),-1.0]])]});}
            var Q1;
            {var subQ0=sQuery(id+"F1.wireOp",EDGE,"E4.bottom");Q1=makeQuery(id+"F1.imprint","IMPRINT",FACE,{"disambiguationData":[TD([[makeQuery(id+"F1.imprint","IMPRINT",EDGE,{"derivedFrom":subQ0}),-1.0]])]});}
            var Q2;
            {var subQ6=sQuery(id+"F1.wireOp",EDGE,"E4.bottom");Q2=makeQuery(id+"F1.imprint","IMPRINT",FACE,{"disambiguationData":[TD([[makeQuery(id+"F1.imprint","IMPRINT",EDGE,{"derivedFrom":subQ6}),1.0]])]});}
            extrude(context, id + "F8", {"entities" : qUnion([Q0, Q1, Q2]), "depth" : 1 * mm, "offsetDistance" : 25 * mm});
        }
        {
            var Q0;
            {var subQ0=sQuery(id+"F1.wireOp",EDGE,"E4.bottom");Q0=makeQuery(id+"F1.imprint","IMPRINT",FACE,{"disambiguationData":[TD([[makeQuery(id+"F1.imprint","IMPRINT",EDGE,{"derivedFrom":subQ0}),-1.0]])]});}
            extrude(context, id + "F9", {"entities" : qUnion([Q0]), "depth" : 3 * mm, "offsetDistance" : 25 * mm, "hasSecondDirection" : true, "secondDirectionOppositeDirection" : false, "secondDirectionDepth" : 1 * mm});
        }
    });
